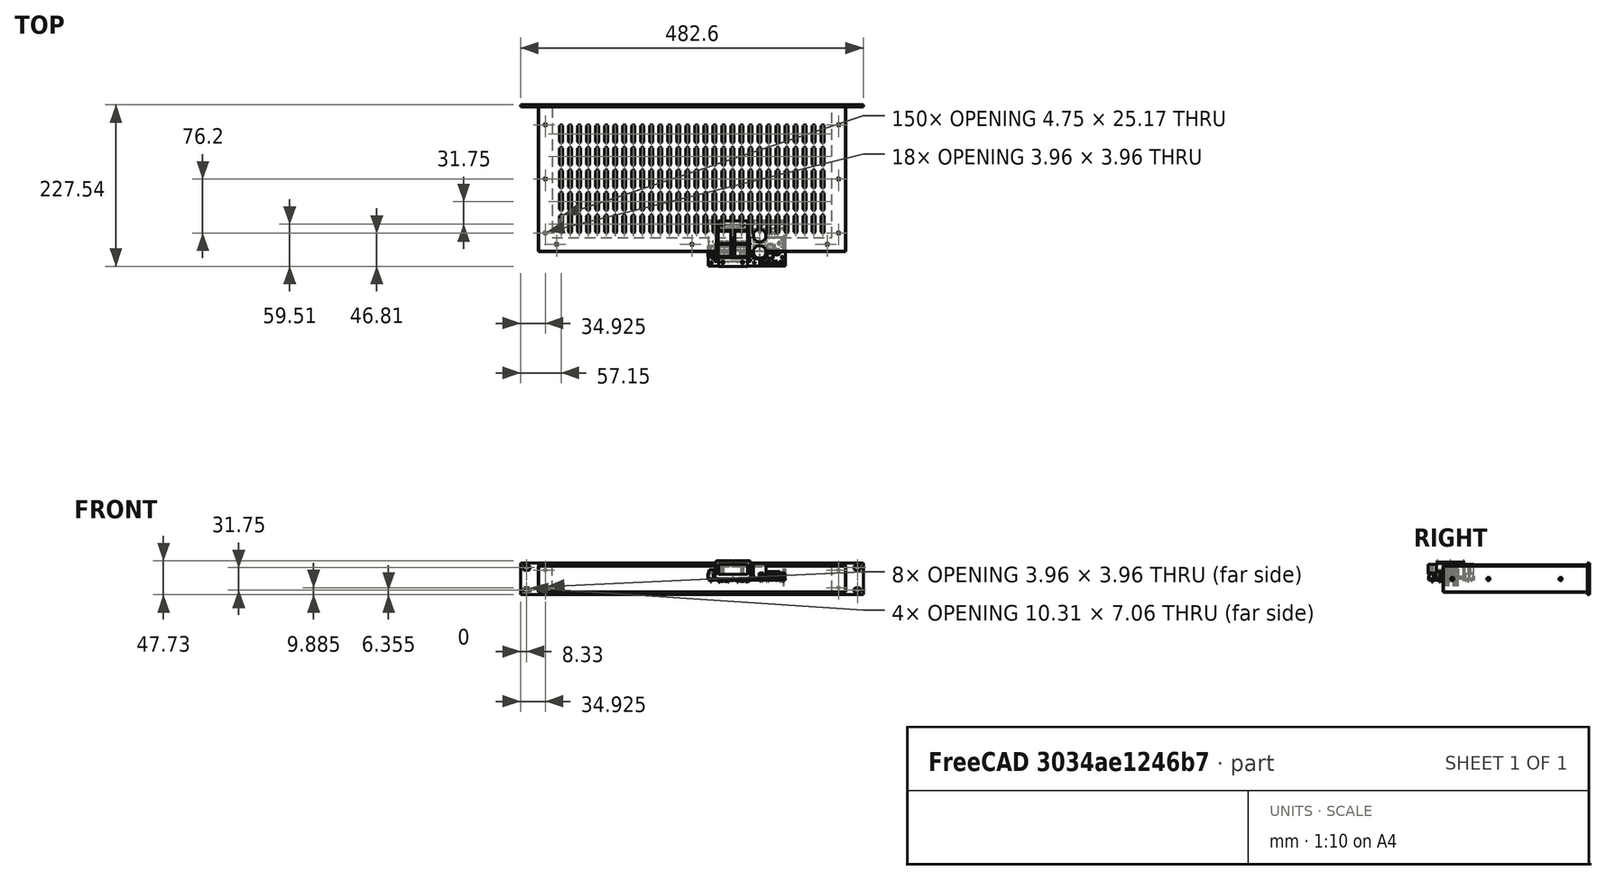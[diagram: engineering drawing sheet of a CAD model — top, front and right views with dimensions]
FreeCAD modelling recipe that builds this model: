
FCSTD DOCUMENT  (FreeCAD 0.19R23074 (Git))
Label: chassis design
License: All rights reserved
LicenseURL: http://en.wikipedia.org/wiki/All_rights_reserved
objects: Part::Prism×340, Part::MultiFuse×164, Part::Box×162, Part::Feature×75, App::Part×5, Part::Cut×3, PartDesign::FeatureBase×3, PartDesign::Body×3, App::DocumentObjectGroup×2, Part::FeaturePython×1, Part::Extrusion×1, Sketcher::SketchObject×1, PartDesign::CoordinateSystem×1
note: 754 computed .brp shape members not serialized (recipe doc carries the construction recipe); baked Part::Feature solids carry a one-line shape summary decoded from their .brp

FEATURE [Part::Box] cube
  AttacherType = Attacher::AttachEngine3D
  Height = 1.27
  Length = 431.8
  Placement = pos=(-215.9,-101.6,-0.635) rot=(0,0,1;0rad)
  Width = 203.2
FEATURE [Part::Prism] prism
  AttacherType = Attacher::AttachEngine3D
  Circumradius = 1.98
  FirstAngle = 0
  Height = 1.29
  Placement = pos=(0,-92.07,-0.645) rot=(0,0,1;0rad)
  Polygon = 20
  SecondAngle = 0
FEATURE [Part::Prism] prism001
  AttacherType = Attacher::AttachEngine3D
  Circumradius = 1.98
  FirstAngle = 0
  Height = 1.29
  Placement = pos=(-190.5,-92.07,-0.645) rot=(0,0,1;0rad)
  Polygon = 20
  SecondAngle = 0
FEATURE [Part::Prism] prism002
  AttacherType = Attacher::AttachEngine3D
  Circumradius = 1.98
  FirstAngle = 0
  Height = 1.29
  Placement = pos=(190.5,-92.07,-0.645) rot=(0,0,1;0rad)
  Polygon = 20
  SecondAngle = 0
FEATURE [Part::Prism] prism003
  AttacherType = Attacher::AttachEngine3D
  Circumradius = 1.98
  FirstAngle = 0
  Height = 1.29
  Placement = pos=(-206.37,0,-0.645) rot=(0,0,1;0rad)
  Polygon = 20
  SecondAngle = 0
FEATURE [Part::Prism] prism004
  AttacherType = Attacher::AttachEngine3D
  Circumradius = 1.98
  FirstAngle = 0
  Height = 1.29
  Placement = pos=(-206.37,-76.2,-0.645) rot=(0,0,1;0rad)
  Polygon = 20
  SecondAngle = 0
FEATURE [Part::Prism] prism005
  AttacherType = Attacher::AttachEngine3D
  Circumradius = 1.98
  FirstAngle = 0
  Height = 1.29
  Placement = pos=(-206.37,76.2,-0.645) rot=(0,0,1;0rad)
  Polygon = 20
  SecondAngle = 0
FEATURE [Part::Prism] prism006
  AttacherType = Attacher::AttachEngine3D
  Circumradius = 1.98
  FirstAngle = 0
  Height = 1.29
  Placement = pos=(206.37,0,-0.645) rot=(0,0,1;0rad)
  Polygon = 20
  SecondAngle = 0
FEATURE [Part::Prism] prism007
  AttacherType = Attacher::AttachEngine3D
  Circumradius = 1.98
  FirstAngle = 0
  Height = 1.29
  Placement = pos=(206.37,-76.2,-0.645) rot=(0,0,1;0rad)
  Polygon = 20
  SecondAngle = 0
FEATURE [Part::Prism] prism008
  AttacherType = Attacher::AttachEngine3D
  Circumradius = 1.98
  FirstAngle = 0
  Height = 1.29
  Placement = pos=(206.37,76.2,-0.645) rot=(0,0,1;0rad)
  Polygon = 20
  SecondAngle = 0
FEATURE [Part::Prism] prism009
  AttacherType = Attacher::AttachEngine3D
  Circumradius = 2.375
  FirstAngle = 0
  Height = 1.29
  Placement = pos=(0,10.325,-0.645) rot=(0,0,1;0rad)
  Polygon = 10
  SecondAngle = 0
FEATURE [Part::Prism] prism010
  AttacherType = Attacher::AttachEngine3D
  Circumradius = 2.375
  FirstAngle = 0
  Height = 1.29
  Placement = pos=(0,-10.325,-0.645) rot=(0,0,1;0rad)
  Polygon = 10
  SecondAngle = 0
FEATURE [Part::Box] cube001
  AttacherType = Attacher::AttachEngine3D
  Height = 1.29
  Length = 4.75
  Placement = pos=(-2.375,-10.325,-0.645) rot=(0,0,1;0rad)
  Width = 20.65
FEATURE [Part::MultiFuse] union
  Placement = pos=(-184.15,63.5,0) rot=(0,0,1;0rad)
  Shapes = -> [prism009,prism010,cube001]
FEATURE [Part::Prism] prism011
  AttacherType = Attacher::AttachEngine3D
  Circumradius = 2.375
  FirstAngle = 0
  Height = 1.29
  Placement = pos=(0,10.325,-0.645) rot=(0,0,1;0rad)
  Polygon = 10
  SecondAngle = 0
FEATURE [Part::Prism] prism012
  AttacherType = Attacher::AttachEngine3D
  Circumradius = 2.375
  FirstAngle = 0
  Height = 1.29
  Placement = pos=(0,-10.325,-0.645) rot=(0,0,1;0rad)
  Polygon = 10
  SecondAngle = 0
FEATURE [Part::Box] cube002
  AttacherType = Attacher::AttachEngine3D
  Height = 1.29
  Length = 4.75
  Placement = pos=(-2.375,-10.325,-0.645) rot=(0,0,1;0rad)
  Width = 20.65
FEATURE [Part::MultiFuse] union001
  Placement = pos=(-171.45,63.5,0) rot=(0,0,1;0rad)
  Shapes = -> [prism011,prism012,cube002]
FEATURE [Part::Prism] prism013
  AttacherType = Attacher::AttachEngine3D
  Circumradius = 2.375
  FirstAngle = 0
  Height = 1.29
  Placement = pos=(0,10.325,-0.645) rot=(0,0,1;0rad)
  Polygon = 10
  SecondAngle = 0
FEATURE [Part::Prism] prism014
  AttacherType = Attacher::AttachEngine3D
  Circumradius = 2.375
  FirstAngle = 0
  Height = 1.29
  Placement = pos=(0,-10.325,-0.645) rot=(0,0,1;0rad)
  Polygon = 10
  SecondAngle = 0
FEATURE [Part::Box] cube003
  AttacherType = Attacher::AttachEngine3D
  Height = 1.29
  Length = 4.75
  Placement = pos=(-2.375,-10.325,-0.645) rot=(0,0,1;0rad)
  Width = 20.65
FEATURE [Part::MultiFuse] union002
  Placement = pos=(-158.75,63.5,0) rot=(0,0,1;0rad)
  Shapes = -> [prism013,prism014,cube003]
FEATURE [Part::Prism] prism015
  AttacherType = Attacher::AttachEngine3D
  Circumradius = 2.375
  FirstAngle = 0
  Height = 1.29
  Placement = pos=(0,10.325,-0.645) rot=(0,0,1;0rad)
  Polygon = 10
  SecondAngle = 0
FEATURE [Part::Prism] prism016
  AttacherType = Attacher::AttachEngine3D
  Circumradius = 2.375
  FirstAngle = 0
  Height = 1.29
  Placement = pos=(0,-10.325,-0.645) rot=(0,0,1;0rad)
  Polygon = 10
  SecondAngle = 0
FEATURE [Part::Box] cube004
  AttacherType = Attacher::AttachEngine3D
  Height = 1.29
  Length = 4.75
  Placement = pos=(-2.375,-10.325,-0.645) rot=(0,0,1;0rad)
  Width = 20.65
FEATURE [Part::MultiFuse] union003
  Placement = pos=(-146.05,63.5,0) rot=(0,0,1;0rad)
  Shapes = -> [prism015,prism016,cube004]
FEATURE [Part::Prism] prism017
  AttacherType = Attacher::AttachEngine3D
  Circumradius = 2.375
  FirstAngle = 0
  Height = 1.29
  Placement = pos=(0,10.325,-0.645) rot=(0,0,1;0rad)
  Polygon = 10
  SecondAngle = 0
FEATURE [Part::Prism] prism018
  AttacherType = Attacher::AttachEngine3D
  Circumradius = 2.375
  FirstAngle = 0
  Height = 1.29
  Placement = pos=(0,-10.325,-0.645) rot=(0,0,1;0rad)
  Polygon = 10
  SecondAngle = 0
FEATURE [Part::Box] cube005
  AttacherType = Attacher::AttachEngine3D
  Height = 1.29
  Length = 4.75
  Placement = pos=(-2.375,-10.325,-0.645) rot=(0,0,1;0rad)
  Width = 20.65
FEATURE [Part::MultiFuse] union004
  Placement = pos=(-133.35,63.5,0) rot=(0,0,1;0rad)
  Shapes = -> [prism017,prism018,cube005]
FEATURE [Part::Prism] prism019
  AttacherType = Attacher::AttachEngine3D
  Circumradius = 2.375
  FirstAngle = 0
  Height = 1.29
  Placement = pos=(0,10.325,-0.645) rot=(0,0,1;0rad)
  Polygon = 10
  SecondAngle = 0
FEATURE [Part::Prism] prism020
  AttacherType = Attacher::AttachEngine3D
  Circumradius = 2.375
  FirstAngle = 0
  Height = 1.29
  Placement = pos=(0,-10.325,-0.645) rot=(0,0,1;0rad)
  Polygon = 10
  SecondAngle = 0
FEATURE [Part::Box] cube006
  AttacherType = Attacher::AttachEngine3D
  Height = 1.29
  Length = 4.75
  Placement = pos=(-2.375,-10.325,-0.645) rot=(0,0,1;0rad)
  Width = 20.65
FEATURE [Part::MultiFuse] union005
  Placement = pos=(-120.65,63.5,0) rot=(0,0,1;0rad)
  Shapes = -> [prism019,prism020,cube006]
FEATURE [Part::Prism] prism021
  AttacherType = Attacher::AttachEngine3D
  Circumradius = 2.375
  FirstAngle = 0
  Height = 1.29
  Placement = pos=(0,10.325,-0.645) rot=(0,0,1;0rad)
  Polygon = 10
  SecondAngle = 0
FEATURE [Part::Prism] prism022
  AttacherType = Attacher::AttachEngine3D
  Circumradius = 2.375
  FirstAngle = 0
  Height = 1.29
  Placement = pos=(0,-10.325,-0.645) rot=(0,0,1;0rad)
  Polygon = 10
  SecondAngle = 0
FEATURE [Part::Box] cube007
  AttacherType = Attacher::AttachEngine3D
  Height = 1.29
  Length = 4.75
  Placement = pos=(-2.375,-10.325,-0.645) rot=(0,0,1;0rad)
  Width = 20.65
FEATURE [Part::MultiFuse] union006
  Placement = pos=(-107.95,63.5,0) rot=(0,0,1;0rad)
  Shapes = -> [prism021,prism022,cube007]
FEATURE [Part::Prism] prism023
  AttacherType = Attacher::AttachEngine3D
  Circumradius = 2.375
  FirstAngle = 0
  Height = 1.29
  Placement = pos=(0,10.325,-0.645) rot=(0,0,1;0rad)
  Polygon = 10
  SecondAngle = 0
FEATURE [Part::Prism] prism024
  AttacherType = Attacher::AttachEngine3D
  Circumradius = 2.375
  FirstAngle = 0
  Height = 1.29
  Placement = pos=(0,-10.325,-0.645) rot=(0,0,1;0rad)
  Polygon = 10
  SecondAngle = 0
FEATURE [Part::Box] cube008
  AttacherType = Attacher::AttachEngine3D
  Height = 1.29
  Length = 4.75
  Placement = pos=(-2.375,-10.325,-0.645) rot=(0,0,1;0rad)
  Width = 20.65
FEATURE [Part::MultiFuse] union007
  Placement = pos=(-95.25,63.5,0) rot=(0,0,1;0rad)
  Shapes = -> [prism023,prism024,cube008]
FEATURE [Part::Prism] prism025
  AttacherType = Attacher::AttachEngine3D
  Circumradius = 2.375
  FirstAngle = 0
  Height = 1.29
  Placement = pos=(0,10.325,-0.645) rot=(0,0,1;0rad)
  Polygon = 10
  SecondAngle = 0
FEATURE [Part::Prism] prism026
  AttacherType = Attacher::AttachEngine3D
  Circumradius = 2.375
  FirstAngle = 0
  Height = 1.29
  Placement = pos=(0,-10.325,-0.645) rot=(0,0,1;0rad)
  Polygon = 10
  SecondAngle = 0
FEATURE [Part::Box] cube009
  AttacherType = Attacher::AttachEngine3D
  Height = 1.29
  Length = 4.75
  Placement = pos=(-2.375,-10.325,-0.645) rot=(0,0,1;0rad)
  Width = 20.65
FEATURE [Part::MultiFuse] union008
  Placement = pos=(-82.55,63.5,0) rot=(0,0,1;0rad)
  Shapes = -> [prism025,prism026,cube009]
FEATURE [Part::Prism] prism027
  AttacherType = Attacher::AttachEngine3D
  Circumradius = 2.375
  FirstAngle = 0
  Height = 1.29
  Placement = pos=(0,10.325,-0.645) rot=(0,0,1;0rad)
  Polygon = 10
  SecondAngle = 0
FEATURE [Part::Prism] prism028
  AttacherType = Attacher::AttachEngine3D
  Circumradius = 2.375
  FirstAngle = 0
  Height = 1.29
  Placement = pos=(0,-10.325,-0.645) rot=(0,0,1;0rad)
  Polygon = 10
  SecondAngle = 0
FEATURE [Part::Box] cube010
  AttacherType = Attacher::AttachEngine3D
  Height = 1.29
  Length = 4.75
  Placement = pos=(-2.375,-10.325,-0.645) rot=(0,0,1;0rad)
  Width = 20.65
FEATURE [Part::MultiFuse] union009
  Placement = pos=(-69.85,63.5,0) rot=(0,0,1;0rad)
  Shapes = -> [prism027,prism028,cube010]
FEATURE [Part::Prism] prism029
  AttacherType = Attacher::AttachEngine3D
  Circumradius = 2.375
  FirstAngle = 0
  Height = 1.29
  Placement = pos=(0,10.325,-0.645) rot=(0,0,1;0rad)
  Polygon = 10
  SecondAngle = 0
FEATURE [Part::Prism] prism030
  AttacherType = Attacher::AttachEngine3D
  Circumradius = 2.375
  FirstAngle = 0
  Height = 1.29
  Placement = pos=(0,-10.325,-0.645) rot=(0,0,1;0rad)
  Polygon = 10
  SecondAngle = 0
FEATURE [Part::Box] cube011
  AttacherType = Attacher::AttachEngine3D
  Height = 1.29
  Length = 4.75
  Placement = pos=(-2.375,-10.325,-0.645) rot=(0,0,1;0rad)
  Width = 20.65
FEATURE [Part::MultiFuse] union010
  Placement = pos=(-57.15,63.5,0) rot=(0,0,1;0rad)
  Shapes = -> [prism029,prism030,cube011]
FEATURE [Part::Prism] prism031
  AttacherType = Attacher::AttachEngine3D
  Circumradius = 2.375
  FirstAngle = 0
  Height = 1.29
  Placement = pos=(0,10.325,-0.645) rot=(0,0,1;0rad)
  Polygon = 10
  SecondAngle = 0
FEATURE [Part::Prism] prism032
  AttacherType = Attacher::AttachEngine3D
  Circumradius = 2.375
  FirstAngle = 0
  Height = 1.29
  Placement = pos=(0,-10.325,-0.645) rot=(0,0,1;0rad)
  Polygon = 10
  SecondAngle = 0
FEATURE [Part::Box] cube012
  AttacherType = Attacher::AttachEngine3D
  Height = 1.29
  Length = 4.75
  Placement = pos=(-2.375,-10.325,-0.645) rot=(0,0,1;0rad)
  Width = 20.65
FEATURE [Part::MultiFuse] union011
  Placement = pos=(-44.45,63.5,0) rot=(0,0,1;0rad)
  Shapes = -> [prism031,prism032,cube012]
FEATURE [Part::Prism] prism033
  AttacherType = Attacher::AttachEngine3D
  Circumradius = 2.375
  FirstAngle = 0
  Height = 1.29
  Placement = pos=(0,10.325,-0.645) rot=(0,0,1;0rad)
  Polygon = 10
  SecondAngle = 0
FEATURE [Part::Prism] prism034
  AttacherType = Attacher::AttachEngine3D
  Circumradius = 2.375
  FirstAngle = 0
  Height = 1.29
  Placement = pos=(0,-10.325,-0.645) rot=(0,0,1;0rad)
  Polygon = 10
  SecondAngle = 0
FEATURE [Part::Box] cube013
  AttacherType = Attacher::AttachEngine3D
  Height = 1.29
  Length = 4.75
  Placement = pos=(-2.375,-10.325,-0.645) rot=(0,0,1;0rad)
  Width = 20.65
FEATURE [Part::MultiFuse] union012
  Placement = pos=(-31.75,63.5,0) rot=(0,0,1;0rad)
  Shapes = -> [prism033,prism034,cube013]
FEATURE [Part::Prism] prism035
  AttacherType = Attacher::AttachEngine3D
  Circumradius = 2.375
  FirstAngle = 0
  Height = 1.29
  Placement = pos=(0,10.325,-0.645) rot=(0,0,1;0rad)
  Polygon = 10
  SecondAngle = 0
FEATURE [Part::Prism] prism036
  AttacherType = Attacher::AttachEngine3D
  Circumradius = 2.375
  FirstAngle = 0
  Height = 1.29
  Placement = pos=(0,-10.325,-0.645) rot=(0,0,1;0rad)
  Polygon = 10
  SecondAngle = 0
FEATURE [Part::Box] cube014
  AttacherType = Attacher::AttachEngine3D
  Height = 1.29
  Length = 4.75
  Placement = pos=(-2.375,-10.325,-0.645) rot=(0,0,1;0rad)
  Width = 20.65
FEATURE [Part::MultiFuse] union013
  Placement = pos=(-19.05,63.5,0) rot=(0,0,1;0rad)
  Shapes = -> [prism035,prism036,cube014]
FEATURE [Part::Prism] prism037
  AttacherType = Attacher::AttachEngine3D
  Circumradius = 2.375
  FirstAngle = 0
  Height = 1.29
  Placement = pos=(0,10.325,-0.645) rot=(0,0,1;0rad)
  Polygon = 10
  SecondAngle = 0
FEATURE [Part::Prism] prism038
  AttacherType = Attacher::AttachEngine3D
  Circumradius = 2.375
  FirstAngle = 0
  Height = 1.29
  Placement = pos=(0,-10.325,-0.645) rot=(0,0,1;0rad)
  Polygon = 10
  SecondAngle = 0
FEATURE [Part::Box] cube015
  AttacherType = Attacher::AttachEngine3D
  Height = 1.29
  Length = 4.75
  Placement = pos=(-2.375,-10.325,-0.645) rot=(0,0,1;0rad)
  Width = 20.65
FEATURE [Part::MultiFuse] union014
  Placement = pos=(-6.35,63.5,0) rot=(0,0,1;0rad)
  Shapes = -> [prism037,prism038,cube015]
FEATURE [Part::Prism] prism039
  AttacherType = Attacher::AttachEngine3D
  Circumradius = 2.375
  FirstAngle = 0
  Height = 1.29
  Placement = pos=(0,10.325,-0.645) rot=(0,0,1;0rad)
  Polygon = 10
  SecondAngle = 0
FEATURE [Part::Prism] prism040
  AttacherType = Attacher::AttachEngine3D
  Circumradius = 2.375
  FirstAngle = 0
  Height = 1.29
  Placement = pos=(0,-10.325,-0.645) rot=(0,0,1;0rad)
  Polygon = 10
  SecondAngle = 0
FEATURE [Part::Box] cube016
  AttacherType = Attacher::AttachEngine3D
  Height = 1.29
  Length = 4.75
  Placement = pos=(-2.375,-10.325,-0.645) rot=(0,0,1;0rad)
  Width = 20.65
FEATURE [Part::MultiFuse] union015
  Placement = pos=(6.35,63.5,0) rot=(0,0,1;0rad)
  Shapes = -> [prism039,prism040,cube016]
FEATURE [Part::Prism] prism041
  AttacherType = Attacher::AttachEngine3D
  Circumradius = 2.375
  FirstAngle = 0
  Height = 1.29
  Placement = pos=(0,10.325,-0.645) rot=(0,0,1;0rad)
  Polygon = 10
  SecondAngle = 0
FEATURE [Part::Prism] prism042
  AttacherType = Attacher::AttachEngine3D
  Circumradius = 2.375
  FirstAngle = 0
  Height = 1.29
  Placement = pos=(0,-10.325,-0.645) rot=(0,0,1;0rad)
  Polygon = 10
  SecondAngle = 0
FEATURE [Part::Box] cube017
  AttacherType = Attacher::AttachEngine3D
  Height = 1.29
  Length = 4.75
  Placement = pos=(-2.375,-10.325,-0.645) rot=(0,0,1;0rad)
  Width = 20.65
FEATURE [Part::MultiFuse] union016
  Placement = pos=(19.05,63.5,0) rot=(0,0,1;0rad)
  Shapes = -> [prism041,prism042,cube017]
FEATURE [Part::Prism] prism043
  AttacherType = Attacher::AttachEngine3D
  Circumradius = 2.375
  FirstAngle = 0
  Height = 1.29
  Placement = pos=(0,10.325,-0.645) rot=(0,0,1;0rad)
  Polygon = 10
  SecondAngle = 0
FEATURE [Part::Prism] prism044
  AttacherType = Attacher::AttachEngine3D
  Circumradius = 2.375
  FirstAngle = 0
  Height = 1.29
  Placement = pos=(0,-10.325,-0.645) rot=(0,0,1;0rad)
  Polygon = 10
  SecondAngle = 0
FEATURE [Part::Box] cube018
  AttacherType = Attacher::AttachEngine3D
  Height = 1.29
  Length = 4.75
  Placement = pos=(-2.375,-10.325,-0.645) rot=(0,0,1;0rad)
  Width = 20.65
FEATURE [Part::MultiFuse] union017
  Placement = pos=(31.75,63.5,0) rot=(0,0,1;0rad)
  Shapes = -> [prism043,prism044,cube018]
FEATURE [Part::Prism] prism045
  AttacherType = Attacher::AttachEngine3D
  Circumradius = 2.375
  FirstAngle = 0
  Height = 1.29
  Placement = pos=(0,10.325,-0.645) rot=(0,0,1;0rad)
  Polygon = 10
  SecondAngle = 0
FEATURE [Part::Prism] prism046
  AttacherType = Attacher::AttachEngine3D
  Circumradius = 2.375
  FirstAngle = 0
  Height = 1.29
  Placement = pos=(0,-10.325,-0.645) rot=(0,0,1;0rad)
  Polygon = 10
  SecondAngle = 0
FEATURE [Part::Box] cube019
  AttacherType = Attacher::AttachEngine3D
  Height = 1.29
  Length = 4.75
  Placement = pos=(-2.375,-10.325,-0.645) rot=(0,0,1;0rad)
  Width = 20.65
FEATURE [Part::MultiFuse] union018
  Placement = pos=(44.45,63.5,0) rot=(0,0,1;0rad)
  Shapes = -> [prism045,prism046,cube019]
FEATURE [Part::Prism] prism047
  AttacherType = Attacher::AttachEngine3D
  Circumradius = 2.375
  FirstAngle = 0
  Height = 1.29
  Placement = pos=(0,10.325,-0.645) rot=(0,0,1;0rad)
  Polygon = 10
  SecondAngle = 0
FEATURE [Part::Prism] prism048
  AttacherType = Attacher::AttachEngine3D
  Circumradius = 2.375
  FirstAngle = 0
  Height = 1.29
  Placement = pos=(0,-10.325,-0.645) rot=(0,0,1;0rad)
  Polygon = 10
  SecondAngle = 0
FEATURE [Part::Box] cube020
  AttacherType = Attacher::AttachEngine3D
  Height = 1.29
  Length = 4.75
  Placement = pos=(-2.375,-10.325,-0.645) rot=(0,0,1;0rad)
  Width = 20.65
FEATURE [Part::MultiFuse] union019
  Placement = pos=(57.15,63.5,0) rot=(0,0,1;0rad)
  Shapes = -> [prism047,prism048,cube020]
FEATURE [Part::Prism] prism049
  AttacherType = Attacher::AttachEngine3D
  Circumradius = 2.375
  FirstAngle = 0
  Height = 1.29
  Placement = pos=(0,10.325,-0.645) rot=(0,0,1;0rad)
  Polygon = 10
  SecondAngle = 0
FEATURE [Part::Prism] prism050
  AttacherType = Attacher::AttachEngine3D
  Circumradius = 2.375
  FirstAngle = 0
  Height = 1.29
  Placement = pos=(0,-10.325,-0.645) rot=(0,0,1;0rad)
  Polygon = 10
  SecondAngle = 0
FEATURE [Part::Box] cube021
  AttacherType = Attacher::AttachEngine3D
  Height = 1.29
  Length = 4.75
  Placement = pos=(-2.375,-10.325,-0.645) rot=(0,0,1;0rad)
  Width = 20.65
FEATURE [Part::MultiFuse] union020
  Placement = pos=(69.85,63.5,0) rot=(0,0,1;0rad)
  Shapes = -> [prism049,prism050,cube021]
FEATURE [Part::Prism] prism051
  AttacherType = Attacher::AttachEngine3D
  Circumradius = 2.375
  FirstAngle = 0
  Height = 1.29
  Placement = pos=(0,10.325,-0.645) rot=(0,0,1;0rad)
  Polygon = 10
  SecondAngle = 0
FEATURE [Part::Prism] prism052
  AttacherType = Attacher::AttachEngine3D
  Circumradius = 2.375
  FirstAngle = 0
  Height = 1.29
  Placement = pos=(0,-10.325,-0.645) rot=(0,0,1;0rad)
  Polygon = 10
  SecondAngle = 0
FEATURE [Part::Box] cube022
  AttacherType = Attacher::AttachEngine3D
  Height = 1.29
  Length = 4.75
  Placement = pos=(-2.375,-10.325,-0.645) rot=(0,0,1;0rad)
  Width = 20.65
FEATURE [Part::MultiFuse] union021
  Placement = pos=(82.55,63.5,0) rot=(0,0,1;0rad)
  Shapes = -> [prism051,prism052,cube022]
FEATURE [Part::Prism] prism053
  AttacherType = Attacher::AttachEngine3D
  Circumradius = 2.375
  FirstAngle = 0
  Height = 1.29
  Placement = pos=(0,10.325,-0.645) rot=(0,0,1;0rad)
  Polygon = 10
  SecondAngle = 0
FEATURE [Part::Prism] prism054
  AttacherType = Attacher::AttachEngine3D
  Circumradius = 2.375
  FirstAngle = 0
  Height = 1.29
  Placement = pos=(0,-10.325,-0.645) rot=(0,0,1;0rad)
  Polygon = 10
  SecondAngle = 0
FEATURE [Part::Box] cube023
  AttacherType = Attacher::AttachEngine3D
  Height = 1.29
  Length = 4.75
  Placement = pos=(-2.375,-10.325,-0.645) rot=(0,0,1;0rad)
  Width = 20.65
FEATURE [Part::MultiFuse] union022
  Placement = pos=(95.25,63.5,0) rot=(0,0,1;0rad)
  Shapes = -> [prism053,prism054,cube023]
FEATURE [Part::Prism] prism055
  AttacherType = Attacher::AttachEngine3D
  Circumradius = 2.375
  FirstAngle = 0
  Height = 1.29
  Placement = pos=(0,10.325,-0.645) rot=(0,0,1;0rad)
  Polygon = 10
  SecondAngle = 0
FEATURE [Part::Prism] prism056
  AttacherType = Attacher::AttachEngine3D
  Circumradius = 2.375
  FirstAngle = 0
  Height = 1.29
  Placement = pos=(0,-10.325,-0.645) rot=(0,0,1;0rad)
  Polygon = 10
  SecondAngle = 0
FEATURE [Part::Box] cube024
  AttacherType = Attacher::AttachEngine3D
  Height = 1.29
  Length = 4.75
  Placement = pos=(-2.375,-10.325,-0.645) rot=(0,0,1;0rad)
  Width = 20.65
FEATURE [Part::MultiFuse] union023
  Placement = pos=(107.95,63.5,0) rot=(0,0,1;0rad)
  Shapes = -> [prism055,prism056,cube024]
FEATURE [Part::Prism] prism057
  AttacherType = Attacher::AttachEngine3D
  Circumradius = 2.375
  FirstAngle = 0
  Height = 1.29
  Placement = pos=(0,10.325,-0.645) rot=(0,0,1;0rad)
  Polygon = 10
  SecondAngle = 0
FEATURE [Part::Prism] prism058
  AttacherType = Attacher::AttachEngine3D
  Circumradius = 2.375
  FirstAngle = 0
  Height = 1.29
  Placement = pos=(0,-10.325,-0.645) rot=(0,0,1;0rad)
  Polygon = 10
  SecondAngle = 0
FEATURE [Part::Box] cube025
  AttacherType = Attacher::AttachEngine3D
  Height = 1.29
  Length = 4.75
  Placement = pos=(-2.375,-10.325,-0.645) rot=(0,0,1;0rad)
  Width = 20.65
FEATURE [Part::MultiFuse] union024
  Placement = pos=(120.65,63.5,0) rot=(0,0,1;0rad)
  Shapes = -> [prism057,prism058,cube025]
FEATURE [Part::Prism] prism059
  AttacherType = Attacher::AttachEngine3D
  Circumradius = 2.375
  FirstAngle = 0
  Height = 1.29
  Placement = pos=(0,10.325,-0.645) rot=(0,0,1;0rad)
  Polygon = 10
  SecondAngle = 0
FEATURE [Part::Prism] prism060
  AttacherType = Attacher::AttachEngine3D
  Circumradius = 2.375
  FirstAngle = 0
  Height = 1.29
  Placement = pos=(0,-10.325,-0.645) rot=(0,0,1;0rad)
  Polygon = 10
  SecondAngle = 0
FEATURE [Part::Box] cube026
  AttacherType = Attacher::AttachEngine3D
  Height = 1.29
  Length = 4.75
  Placement = pos=(-2.375,-10.325,-0.645) rot=(0,0,1;0rad)
  Width = 20.65
FEATURE [Part::MultiFuse] union025
  Placement = pos=(133.35,63.5,0) rot=(0,0,1;0rad)
  Shapes = -> [prism059,prism060,cube026]
FEATURE [Part::Prism] prism061
  AttacherType = Attacher::AttachEngine3D
  Circumradius = 2.375
  FirstAngle = 0
  Height = 1.29
  Placement = pos=(0,10.325,-0.645) rot=(0,0,1;0rad)
  Polygon = 10
  SecondAngle = 0
FEATURE [Part::Prism] prism062
  AttacherType = Attacher::AttachEngine3D
  Circumradius = 2.375
  FirstAngle = 0
  Height = 1.29
  Placement = pos=(0,-10.325,-0.645) rot=(0,0,1;0rad)
  Polygon = 10
  SecondAngle = 0
FEATURE [Part::Box] cube027
  AttacherType = Attacher::AttachEngine3D
  Height = 1.29
  Length = 4.75
  Placement = pos=(-2.375,-10.325,-0.645) rot=(0,0,1;0rad)
  Width = 20.65
FEATURE [Part::MultiFuse] union026
  Placement = pos=(146.05,63.5,0) rot=(0,0,1;0rad)
  Shapes = -> [prism061,prism062,cube027]
FEATURE [Part::Prism] prism063
  AttacherType = Attacher::AttachEngine3D
  Circumradius = 2.375
  FirstAngle = 0
  Height = 1.29
  Placement = pos=(0,10.325,-0.645) rot=(0,0,1;0rad)
  Polygon = 10
  SecondAngle = 0
FEATURE [Part::Prism] prism064
  AttacherType = Attacher::AttachEngine3D
  Circumradius = 2.375
  FirstAngle = 0
  Height = 1.29
  Placement = pos=(0,-10.325,-0.645) rot=(0,0,1;0rad)
  Polygon = 10
  SecondAngle = 0
FEATURE [Part::Box] cube028
  AttacherType = Attacher::AttachEngine3D
  Height = 1.29
  Length = 4.75
  Placement = pos=(-2.375,-10.325,-0.645) rot=(0,0,1;0rad)
  Width = 20.65
FEATURE [Part::MultiFuse] union027
  Placement = pos=(158.75,63.5,0) rot=(0,0,1;0rad)
  Shapes = -> [prism063,prism064,cube028]
FEATURE [Part::Prism] prism065
  AttacherType = Attacher::AttachEngine3D
  Circumradius = 2.375
  FirstAngle = 0
  Height = 1.29
  Placement = pos=(0,10.325,-0.645) rot=(0,0,1;0rad)
  Polygon = 10
  SecondAngle = 0
FEATURE [Part::Prism] prism066
  AttacherType = Attacher::AttachEngine3D
  Circumradius = 2.375
  FirstAngle = 0
  Height = 1.29
  Placement = pos=(0,-10.325,-0.645) rot=(0,0,1;0rad)
  Polygon = 10
  SecondAngle = 0
FEATURE [Part::Box] cube029
  AttacherType = Attacher::AttachEngine3D
  Height = 1.29
  Length = 4.75
  Placement = pos=(-2.375,-10.325,-0.645) rot=(0,0,1;0rad)
  Width = 20.65
FEATURE [Part::MultiFuse] union028
  Placement = pos=(171.45,63.5,0) rot=(0,0,1;0rad)
  Shapes = -> [prism065,prism066,cube029]
FEATURE [Part::Prism] prism067
  AttacherType = Attacher::AttachEngine3D
  Circumradius = 2.375
  FirstAngle = 0
  Height = 1.29
  Placement = pos=(0,10.325,-0.645) rot=(0,0,1;0rad)
  Polygon = 10
  SecondAngle = 0
FEATURE [Part::Prism] prism068
  AttacherType = Attacher::AttachEngine3D
  Circumradius = 2.375
  FirstAngle = 0
  Height = 1.29
  Placement = pos=(0,-10.325,-0.645) rot=(0,0,1;0rad)
  Polygon = 10
  SecondAngle = 0
FEATURE [Part::Box] cube030
  AttacherType = Attacher::AttachEngine3D
  Height = 1.29
  Length = 4.75
  Placement = pos=(-2.375,-10.325,-0.645) rot=(0,0,1;0rad)
  Width = 20.65
FEATURE [Part::MultiFuse] union029
  Placement = pos=(184.15,63.5,0) rot=(0,0,1;0rad)
  Shapes = -> [prism067,prism068,cube030]
FEATURE [Part::MultiFuse] Group
  Shapes = -> [union,union001,union002,union003,union004,union005,union006,union007,union008,union009,union010,union011,union012,union013,union014,union015,union016,union017,union018,union019,union020,union021,union022,union023,union024,union025,union026,union027,union028,union029]
FEATURE [Part::Prism] prism069
  AttacherType = Attacher::AttachEngine3D
  Circumradius = 2.375
  FirstAngle = 0
  Height = 1.29
  Placement = pos=(0,10.325,-0.645) rot=(0,0,1;0rad)
  Polygon = 10
  SecondAngle = 0
FEATURE [Part::Prism] prism070
  AttacherType = Attacher::AttachEngine3D
  Circumradius = 2.375
  FirstAngle = 0
  Height = 1.29
  Placement = pos=(0,-10.325,-0.645) rot=(0,0,1;0rad)
  Polygon = 10
  SecondAngle = 0
FEATURE [Part::Box] cube031
  AttacherType = Attacher::AttachEngine3D
  Height = 1.29
  Length = 4.75
  Placement = pos=(-2.375,-10.325,-0.645) rot=(0,0,1;0rad)
  Width = 20.65
FEATURE [Part::MultiFuse] union030
  Placement = pos=(-184.15,31.75,0) rot=(0,0,1;0rad)
  Shapes = -> [prism069,prism070,cube031]
FEATURE [Part::Prism] prism071
  AttacherType = Attacher::AttachEngine3D
  Circumradius = 2.375
  FirstAngle = 0
  Height = 1.29
  Placement = pos=(0,10.325,-0.645) rot=(0,0,1;0rad)
  Polygon = 10
  SecondAngle = 0
FEATURE [Part::Prism] prism072
  AttacherType = Attacher::AttachEngine3D
  Circumradius = 2.375
  FirstAngle = 0
  Height = 1.29
  Placement = pos=(0,-10.325,-0.645) rot=(0,0,1;0rad)
  Polygon = 10
  SecondAngle = 0
FEATURE [Part::Box] cube032
  AttacherType = Attacher::AttachEngine3D
  Height = 1.29
  Length = 4.75
  Placement = pos=(-2.375,-10.325,-0.645) rot=(0,0,1;0rad)
  Width = 20.65
FEATURE [Part::MultiFuse] union031
  Placement = pos=(-171.45,31.75,0) rot=(0,0,1;0rad)
  Shapes = -> [prism071,prism072,cube032]
FEATURE [Part::Prism] prism073
  AttacherType = Attacher::AttachEngine3D
  Circumradius = 2.375
  FirstAngle = 0
  Height = 1.29
  Placement = pos=(0,10.325,-0.645) rot=(0,0,1;0rad)
  Polygon = 10
  SecondAngle = 0
FEATURE [Part::Prism] prism074
  AttacherType = Attacher::AttachEngine3D
  Circumradius = 2.375
  FirstAngle = 0
  Height = 1.29
  Placement = pos=(0,-10.325,-0.645) rot=(0,0,1;0rad)
  Polygon = 10
  SecondAngle = 0
FEATURE [Part::Box] cube033
  AttacherType = Attacher::AttachEngine3D
  Height = 1.29
  Length = 4.75
  Placement = pos=(-2.375,-10.325,-0.645) rot=(0,0,1;0rad)
  Width = 20.65
FEATURE [Part::MultiFuse] union032
  Placement = pos=(-158.75,31.75,0) rot=(0,0,1;0rad)
  Shapes = -> [prism073,prism074,cube033]
FEATURE [Part::Prism] prism075
  AttacherType = Attacher::AttachEngine3D
  Circumradius = 2.375
  FirstAngle = 0
  Height = 1.29
  Placement = pos=(0,10.325,-0.645) rot=(0,0,1;0rad)
  Polygon = 10
  SecondAngle = 0
FEATURE [Part::Prism] prism076
  AttacherType = Attacher::AttachEngine3D
  Circumradius = 2.375
  FirstAngle = 0
  Height = 1.29
  Placement = pos=(0,-10.325,-0.645) rot=(0,0,1;0rad)
  Polygon = 10
  SecondAngle = 0
FEATURE [Part::Box] cube034
  AttacherType = Attacher::AttachEngine3D
  Height = 1.29
  Length = 4.75
  Placement = pos=(-2.375,-10.325,-0.645) rot=(0,0,1;0rad)
  Width = 20.65
FEATURE [Part::MultiFuse] union033
  Placement = pos=(-146.05,31.75,0) rot=(0,0,1;0rad)
  Shapes = -> [prism075,prism076,cube034]
FEATURE [Part::Prism] prism077
  AttacherType = Attacher::AttachEngine3D
  Circumradius = 2.375
  FirstAngle = 0
  Height = 1.29
  Placement = pos=(0,10.325,-0.645) rot=(0,0,1;0rad)
  Polygon = 10
  SecondAngle = 0
FEATURE [Part::Prism] prism078
  AttacherType = Attacher::AttachEngine3D
  Circumradius = 2.375
  FirstAngle = 0
  Height = 1.29
  Placement = pos=(0,-10.325,-0.645) rot=(0,0,1;0rad)
  Polygon = 10
  SecondAngle = 0
FEATURE [Part::Box] cube035
  AttacherType = Attacher::AttachEngine3D
  Height = 1.29
  Length = 4.75
  Placement = pos=(-2.375,-10.325,-0.645) rot=(0,0,1;0rad)
  Width = 20.65
FEATURE [Part::MultiFuse] union034
  Placement = pos=(-133.35,31.75,0) rot=(0,0,1;0rad)
  Shapes = -> [prism077,prism078,cube035]
FEATURE [Part::Prism] prism079
  AttacherType = Attacher::AttachEngine3D
  Circumradius = 2.375
  FirstAngle = 0
  Height = 1.29
  Placement = pos=(0,10.325,-0.645) rot=(0,0,1;0rad)
  Polygon = 10
  SecondAngle = 0
FEATURE [Part::Prism] prism080
  AttacherType = Attacher::AttachEngine3D
  Circumradius = 2.375
  FirstAngle = 0
  Height = 1.29
  Placement = pos=(0,-10.325,-0.645) rot=(0,0,1;0rad)
  Polygon = 10
  SecondAngle = 0
FEATURE [Part::Box] cube036
  AttacherType = Attacher::AttachEngine3D
  Height = 1.29
  Length = 4.75
  Placement = pos=(-2.375,-10.325,-0.645) rot=(0,0,1;0rad)
  Width = 20.65
FEATURE [Part::MultiFuse] union035
  Placement = pos=(-120.65,31.75,0) rot=(0,0,1;0rad)
  Shapes = -> [prism079,prism080,cube036]
FEATURE [Part::Prism] prism081
  AttacherType = Attacher::AttachEngine3D
  Circumradius = 2.375
  FirstAngle = 0
  Height = 1.29
  Placement = pos=(0,10.325,-0.645) rot=(0,0,1;0rad)
  Polygon = 10
  SecondAngle = 0
FEATURE [Part::Prism] prism082
  AttacherType = Attacher::AttachEngine3D
  Circumradius = 2.375
  FirstAngle = 0
  Height = 1.29
  Placement = pos=(0,-10.325,-0.645) rot=(0,0,1;0rad)
  Polygon = 10
  SecondAngle = 0
FEATURE [Part::Box] cube037
  AttacherType = Attacher::AttachEngine3D
  Height = 1.29
  Length = 4.75
  Placement = pos=(-2.375,-10.325,-0.645) rot=(0,0,1;0rad)
  Width = 20.65
FEATURE [Part::MultiFuse] union036
  Placement = pos=(-107.95,31.75,0) rot=(0,0,1;0rad)
  Shapes = -> [prism081,prism082,cube037]
FEATURE [Part::Prism] prism083
  AttacherType = Attacher::AttachEngine3D
  Circumradius = 2.375
  FirstAngle = 0
  Height = 1.29
  Placement = pos=(0,10.325,-0.645) rot=(0,0,1;0rad)
  Polygon = 10
  SecondAngle = 0
FEATURE [Part::Prism] prism084
  AttacherType = Attacher::AttachEngine3D
  Circumradius = 2.375
  FirstAngle = 0
  Height = 1.29
  Placement = pos=(0,-10.325,-0.645) rot=(0,0,1;0rad)
  Polygon = 10
  SecondAngle = 0
FEATURE [Part::Box] cube038
  AttacherType = Attacher::AttachEngine3D
  Height = 1.29
  Length = 4.75
  Placement = pos=(-2.375,-10.325,-0.645) rot=(0,0,1;0rad)
  Width = 20.65
FEATURE [Part::MultiFuse] union037
  Placement = pos=(-95.25,31.75,0) rot=(0,0,1;0rad)
  Shapes = -> [prism083,prism084,cube038]
FEATURE [Part::Prism] prism085
  AttacherType = Attacher::AttachEngine3D
  Circumradius = 2.375
  FirstAngle = 0
  Height = 1.29
  Placement = pos=(0,10.325,-0.645) rot=(0,0,1;0rad)
  Polygon = 10
  SecondAngle = 0
FEATURE [Part::Prism] prism086
  AttacherType = Attacher::AttachEngine3D
  Circumradius = 2.375
  FirstAngle = 0
  Height = 1.29
  Placement = pos=(0,-10.325,-0.645) rot=(0,0,1;0rad)
  Polygon = 10
  SecondAngle = 0
FEATURE [Part::Box] cube039
  AttacherType = Attacher::AttachEngine3D
  Height = 1.29
  Length = 4.75
  Placement = pos=(-2.375,-10.325,-0.645) rot=(0,0,1;0rad)
  Width = 20.65
FEATURE [Part::MultiFuse] union038
  Placement = pos=(-82.55,31.75,0) rot=(0,0,1;0rad)
  Shapes = -> [prism085,prism086,cube039]
FEATURE [Part::Prism] prism087
  AttacherType = Attacher::AttachEngine3D
  Circumradius = 2.375
  FirstAngle = 0
  Height = 1.29
  Placement = pos=(0,10.325,-0.645) rot=(0,0,1;0rad)
  Polygon = 10
  SecondAngle = 0
FEATURE [Part::Prism] prism088
  AttacherType = Attacher::AttachEngine3D
  Circumradius = 2.375
  FirstAngle = 0
  Height = 1.29
  Placement = pos=(0,-10.325,-0.645) rot=(0,0,1;0rad)
  Polygon = 10
  SecondAngle = 0
FEATURE [Part::Box] cube040
  AttacherType = Attacher::AttachEngine3D
  Height = 1.29
  Length = 4.75
  Placement = pos=(-2.375,-10.325,-0.645) rot=(0,0,1;0rad)
  Width = 20.65
FEATURE [Part::MultiFuse] union039
  Placement = pos=(-69.85,31.75,0) rot=(0,0,1;0rad)
  Shapes = -> [prism087,prism088,cube040]
FEATURE [Part::Prism] prism089
  AttacherType = Attacher::AttachEngine3D
  Circumradius = 2.375
  FirstAngle = 0
  Height = 1.29
  Placement = pos=(0,10.325,-0.645) rot=(0,0,1;0rad)
  Polygon = 10
  SecondAngle = 0
FEATURE [Part::Prism] prism090
  AttacherType = Attacher::AttachEngine3D
  Circumradius = 2.375
  FirstAngle = 0
  Height = 1.29
  Placement = pos=(0,-10.325,-0.645) rot=(0,0,1;0rad)
  Polygon = 10
  SecondAngle = 0
FEATURE [Part::Box] cube041
  AttacherType = Attacher::AttachEngine3D
  Height = 1.29
  Length = 4.75
  Placement = pos=(-2.375,-10.325,-0.645) rot=(0,0,1;0rad)
  Width = 20.65
FEATURE [Part::MultiFuse] union040
  Placement = pos=(-57.15,31.75,0) rot=(0,0,1;0rad)
  Shapes = -> [prism089,prism090,cube041]
FEATURE [Part::Prism] prism091
  AttacherType = Attacher::AttachEngine3D
  Circumradius = 2.375
  FirstAngle = 0
  Height = 1.29
  Placement = pos=(0,10.325,-0.645) rot=(0,0,1;0rad)
  Polygon = 10
  SecondAngle = 0
FEATURE [Part::Prism] prism092
  AttacherType = Attacher::AttachEngine3D
  Circumradius = 2.375
  FirstAngle = 0
  Height = 1.29
  Placement = pos=(0,-10.325,-0.645) rot=(0,0,1;0rad)
  Polygon = 10
  SecondAngle = 0
FEATURE [Part::Box] cube042
  AttacherType = Attacher::AttachEngine3D
  Height = 1.29
  Length = 4.75
  Placement = pos=(-2.375,-10.325,-0.645) rot=(0,0,1;0rad)
  Width = 20.65
FEATURE [Part::MultiFuse] union041
  Placement = pos=(-44.45,31.75,0) rot=(0,0,1;0rad)
  Shapes = -> [prism091,prism092,cube042]
FEATURE [Part::Prism] prism093
  AttacherType = Attacher::AttachEngine3D
  Circumradius = 2.375
  FirstAngle = 0
  Height = 1.29
  Placement = pos=(0,10.325,-0.645) rot=(0,0,1;0rad)
  Polygon = 10
  SecondAngle = 0
FEATURE [Part::Prism] prism094
  AttacherType = Attacher::AttachEngine3D
  Circumradius = 2.375
  FirstAngle = 0
  Height = 1.29
  Placement = pos=(0,-10.325,-0.645) rot=(0,0,1;0rad)
  Polygon = 10
  SecondAngle = 0
FEATURE [Part::Box] cube043
  AttacherType = Attacher::AttachEngine3D
  Height = 1.29
  Length = 4.75
  Placement = pos=(-2.375,-10.325,-0.645) rot=(0,0,1;0rad)
  Width = 20.65
FEATURE [Part::MultiFuse] union042
  Placement = pos=(-31.75,31.75,0) rot=(0,0,1;0rad)
  Shapes = -> [prism093,prism094,cube043]
FEATURE [Part::Prism] prism095
  AttacherType = Attacher::AttachEngine3D
  Circumradius = 2.375
  FirstAngle = 0
  Height = 1.29
  Placement = pos=(0,10.325,-0.645) rot=(0,0,1;0rad)
  Polygon = 10
  SecondAngle = 0
FEATURE [Part::Prism] prism096
  AttacherType = Attacher::AttachEngine3D
  Circumradius = 2.375
  FirstAngle = 0
  Height = 1.29
  Placement = pos=(0,-10.325,-0.645) rot=(0,0,1;0rad)
  Polygon = 10
  SecondAngle = 0
FEATURE [Part::Box] cube044
  AttacherType = Attacher::AttachEngine3D
  Height = 1.29
  Length = 4.75
  Placement = pos=(-2.375,-10.325,-0.645) rot=(0,0,1;0rad)
  Width = 20.65
FEATURE [Part::MultiFuse] union043
  Placement = pos=(-19.05,31.75,0) rot=(0,0,1;0rad)
  Shapes = -> [prism095,prism096,cube044]
FEATURE [Part::Prism] prism097
  AttacherType = Attacher::AttachEngine3D
  Circumradius = 2.375
  FirstAngle = 0
  Height = 1.29
  Placement = pos=(0,10.325,-0.645) rot=(0,0,1;0rad)
  Polygon = 10
  SecondAngle = 0
FEATURE [Part::Prism] prism098
  AttacherType = Attacher::AttachEngine3D
  Circumradius = 2.375
  FirstAngle = 0
  Height = 1.29
  Placement = pos=(0,-10.325,-0.645) rot=(0,0,1;0rad)
  Polygon = 10
  SecondAngle = 0
FEATURE [Part::Box] cube045
  AttacherType = Attacher::AttachEngine3D
  Height = 1.29
  Length = 4.75
  Placement = pos=(-2.375,-10.325,-0.645) rot=(0,0,1;0rad)
  Width = 20.65
FEATURE [Part::MultiFuse] union044
  Placement = pos=(-6.35,31.75,0) rot=(0,0,1;0rad)
  Shapes = -> [prism097,prism098,cube045]
FEATURE [Part::Prism] prism099
  AttacherType = Attacher::AttachEngine3D
  Circumradius = 2.375
  FirstAngle = 0
  Height = 1.29
  Placement = pos=(0,10.325,-0.645) rot=(0,0,1;0rad)
  Polygon = 10
  SecondAngle = 0
FEATURE [Part::Prism] prism100
  AttacherType = Attacher::AttachEngine3D
  Circumradius = 2.375
  FirstAngle = 0
  Height = 1.29
  Placement = pos=(0,-10.325,-0.645) rot=(0,0,1;0rad)
  Polygon = 10
  SecondAngle = 0
FEATURE [Part::Box] cube046
  AttacherType = Attacher::AttachEngine3D
  Height = 1.29
  Length = 4.75
  Placement = pos=(-2.375,-10.325,-0.645) rot=(0,0,1;0rad)
  Width = 20.65
FEATURE [Part::MultiFuse] union045
  Placement = pos=(6.35,31.75,0) rot=(0,0,1;0rad)
  Shapes = -> [prism099,prism100,cube046]
FEATURE [Part::Prism] prism101
  AttacherType = Attacher::AttachEngine3D
  Circumradius = 2.375
  FirstAngle = 0
  Height = 1.29
  Placement = pos=(0,10.325,-0.645) rot=(0,0,1;0rad)
  Polygon = 10
  SecondAngle = 0
FEATURE [Part::Prism] prism102
  AttacherType = Attacher::AttachEngine3D
  Circumradius = 2.375
  FirstAngle = 0
  Height = 1.29
  Placement = pos=(0,-10.325,-0.645) rot=(0,0,1;0rad)
  Polygon = 10
  SecondAngle = 0
FEATURE [Part::Box] cube047
  AttacherType = Attacher::AttachEngine3D
  Height = 1.29
  Length = 4.75
  Placement = pos=(-2.375,-10.325,-0.645) rot=(0,0,1;0rad)
  Width = 20.65
FEATURE [Part::MultiFuse] union046
  Placement = pos=(19.05,31.75,0) rot=(0,0,1;0rad)
  Shapes = -> [prism101,prism102,cube047]
FEATURE [Part::Prism] prism103
  AttacherType = Attacher::AttachEngine3D
  Circumradius = 2.375
  FirstAngle = 0
  Height = 1.29
  Placement = pos=(0,10.325,-0.645) rot=(0,0,1;0rad)
  Polygon = 10
  SecondAngle = 0
FEATURE [Part::Prism] prism104
  AttacherType = Attacher::AttachEngine3D
  Circumradius = 2.375
  FirstAngle = 0
  Height = 1.29
  Placement = pos=(0,-10.325,-0.645) rot=(0,0,1;0rad)
  Polygon = 10
  SecondAngle = 0
FEATURE [Part::Box] cube048
  AttacherType = Attacher::AttachEngine3D
  Height = 1.29
  Length = 4.75
  Placement = pos=(-2.375,-10.325,-0.645) rot=(0,0,1;0rad)
  Width = 20.65
FEATURE [Part::MultiFuse] union047
  Placement = pos=(31.75,31.75,0) rot=(0,0,1;0rad)
  Shapes = -> [prism103,prism104,cube048]
FEATURE [Part::Prism] prism105
  AttacherType = Attacher::AttachEngine3D
  Circumradius = 2.375
  FirstAngle = 0
  Height = 1.29
  Placement = pos=(0,10.325,-0.645) rot=(0,0,1;0rad)
  Polygon = 10
  SecondAngle = 0
FEATURE [Part::Prism] prism106
  AttacherType = Attacher::AttachEngine3D
  Circumradius = 2.375
  FirstAngle = 0
  Height = 1.29
  Placement = pos=(0,-10.325,-0.645) rot=(0,0,1;0rad)
  Polygon = 10
  SecondAngle = 0
FEATURE [Part::Box] cube049
  AttacherType = Attacher::AttachEngine3D
  Height = 1.29
  Length = 4.75
  Placement = pos=(-2.375,-10.325,-0.645) rot=(0,0,1;0rad)
  Width = 20.65
FEATURE [Part::MultiFuse] union048
  Placement = pos=(44.45,31.75,0) rot=(0,0,1;0rad)
  Shapes = -> [prism105,prism106,cube049]
FEATURE [Part::Prism] prism107
  AttacherType = Attacher::AttachEngine3D
  Circumradius = 2.375
  FirstAngle = 0
  Height = 1.29
  Placement = pos=(0,10.325,-0.645) rot=(0,0,1;0rad)
  Polygon = 10
  SecondAngle = 0
FEATURE [Part::Prism] prism108
  AttacherType = Attacher::AttachEngine3D
  Circumradius = 2.375
  FirstAngle = 0
  Height = 1.29
  Placement = pos=(0,-10.325,-0.645) rot=(0,0,1;0rad)
  Polygon = 10
  SecondAngle = 0
FEATURE [Part::Box] cube050
  AttacherType = Attacher::AttachEngine3D
  Height = 1.29
  Length = 4.75
  Placement = pos=(-2.375,-10.325,-0.645) rot=(0,0,1;0rad)
  Width = 20.65
FEATURE [Part::MultiFuse] union049
  Placement = pos=(57.15,31.75,0) rot=(0,0,1;0rad)
  Shapes = -> [prism107,prism108,cube050]
FEATURE [Part::Prism] prism109
  AttacherType = Attacher::AttachEngine3D
  Circumradius = 2.375
  FirstAngle = 0
  Height = 1.29
  Placement = pos=(0,10.325,-0.645) rot=(0,0,1;0rad)
  Polygon = 10
  SecondAngle = 0
FEATURE [Part::Prism] prism110
  AttacherType = Attacher::AttachEngine3D
  Circumradius = 2.375
  FirstAngle = 0
  Height = 1.29
  Placement = pos=(0,-10.325,-0.645) rot=(0,0,1;0rad)
  Polygon = 10
  SecondAngle = 0
FEATURE [Part::Box] cube051
  AttacherType = Attacher::AttachEngine3D
  Height = 1.29
  Length = 4.75
  Placement = pos=(-2.375,-10.325,-0.645) rot=(0,0,1;0rad)
  Width = 20.65
FEATURE [Part::MultiFuse] union050
  Placement = pos=(69.85,31.75,0) rot=(0,0,1;0rad)
  Shapes = -> [prism109,prism110,cube051]
FEATURE [Part::Prism] prism111
  AttacherType = Attacher::AttachEngine3D
  Circumradius = 2.375
  FirstAngle = 0
  Height = 1.29
  Placement = pos=(0,10.325,-0.645) rot=(0,0,1;0rad)
  Polygon = 10
  SecondAngle = 0
FEATURE [Part::Prism] prism112
  AttacherType = Attacher::AttachEngine3D
  Circumradius = 2.375
  FirstAngle = 0
  Height = 1.29
  Placement = pos=(0,-10.325,-0.645) rot=(0,0,1;0rad)
  Polygon = 10
  SecondAngle = 0
FEATURE [Part::Box] cube052
  AttacherType = Attacher::AttachEngine3D
  Height = 1.29
  Length = 4.75
  Placement = pos=(-2.375,-10.325,-0.645) rot=(0,0,1;0rad)
  Width = 20.65
FEATURE [Part::MultiFuse] union051
  Placement = pos=(82.55,31.75,0) rot=(0,0,1;0rad)
  Shapes = -> [prism111,prism112,cube052]
FEATURE [Part::Prism] prism113
  AttacherType = Attacher::AttachEngine3D
  Circumradius = 2.375
  FirstAngle = 0
  Height = 1.29
  Placement = pos=(0,10.325,-0.645) rot=(0,0,1;0rad)
  Polygon = 10
  SecondAngle = 0
FEATURE [Part::Prism] prism114
  AttacherType = Attacher::AttachEngine3D
  Circumradius = 2.375
  FirstAngle = 0
  Height = 1.29
  Placement = pos=(0,-10.325,-0.645) rot=(0,0,1;0rad)
  Polygon = 10
  SecondAngle = 0
FEATURE [Part::Box] cube053
  AttacherType = Attacher::AttachEngine3D
  Height = 1.29
  Length = 4.75
  Placement = pos=(-2.375,-10.325,-0.645) rot=(0,0,1;0rad)
  Width = 20.65
FEATURE [Part::MultiFuse] union052
  Placement = pos=(95.25,31.75,0) rot=(0,0,1;0rad)
  Shapes = -> [prism113,prism114,cube053]
FEATURE [Part::Prism] prism115
  AttacherType = Attacher::AttachEngine3D
  Circumradius = 2.375
  FirstAngle = 0
  Height = 1.29
  Placement = pos=(0,10.325,-0.645) rot=(0,0,1;0rad)
  Polygon = 10
  SecondAngle = 0
FEATURE [Part::Prism] prism116
  AttacherType = Attacher::AttachEngine3D
  Circumradius = 2.375
  FirstAngle = 0
  Height = 1.29
  Placement = pos=(0,-10.325,-0.645) rot=(0,0,1;0rad)
  Polygon = 10
  SecondAngle = 0
FEATURE [Part::Box] cube054
  AttacherType = Attacher::AttachEngine3D
  Height = 1.29
  Length = 4.75
  Placement = pos=(-2.375,-10.325,-0.645) rot=(0,0,1;0rad)
  Width = 20.65
FEATURE [Part::MultiFuse] union053
  Placement = pos=(107.95,31.75,0) rot=(0,0,1;0rad)
  Shapes = -> [prism115,prism116,cube054]
FEATURE [Part::Prism] prism117
  AttacherType = Attacher::AttachEngine3D
  Circumradius = 2.375
  FirstAngle = 0
  Height = 1.29
  Placement = pos=(0,10.325,-0.645) rot=(0,0,1;0rad)
  Polygon = 10
  SecondAngle = 0
FEATURE [Part::Prism] prism118
  AttacherType = Attacher::AttachEngine3D
  Circumradius = 2.375
  FirstAngle = 0
  Height = 1.29
  Placement = pos=(0,-10.325,-0.645) rot=(0,0,1;0rad)
  Polygon = 10
  SecondAngle = 0
FEATURE [Part::Box] cube055
  AttacherType = Attacher::AttachEngine3D
  Height = 1.29
  Length = 4.75
  Placement = pos=(-2.375,-10.325,-0.645) rot=(0,0,1;0rad)
  Width = 20.65
FEATURE [Part::MultiFuse] union054
  Placement = pos=(120.65,31.75,0) rot=(0,0,1;0rad)
  Shapes = -> [prism117,prism118,cube055]
FEATURE [Part::Prism] prism119
  AttacherType = Attacher::AttachEngine3D
  Circumradius = 2.375
  FirstAngle = 0
  Height = 1.29
  Placement = pos=(0,10.325,-0.645) rot=(0,0,1;0rad)
  Polygon = 10
  SecondAngle = 0
FEATURE [Part::Prism] prism120
  AttacherType = Attacher::AttachEngine3D
  Circumradius = 2.375
  FirstAngle = 0
  Height = 1.29
  Placement = pos=(0,-10.325,-0.645) rot=(0,0,1;0rad)
  Polygon = 10
  SecondAngle = 0
FEATURE [Part::Box] cube056
  AttacherType = Attacher::AttachEngine3D
  Height = 1.29
  Length = 4.75
  Placement = pos=(-2.375,-10.325,-0.645) rot=(0,0,1;0rad)
  Width = 20.65
FEATURE [Part::MultiFuse] union055
  Placement = pos=(133.35,31.75,0) rot=(0,0,1;0rad)
  Shapes = -> [prism119,prism120,cube056]
FEATURE [Part::Prism] prism121
  AttacherType = Attacher::AttachEngine3D
  Circumradius = 2.375
  FirstAngle = 0
  Height = 1.29
  Placement = pos=(0,10.325,-0.645) rot=(0,0,1;0rad)
  Polygon = 10
  SecondAngle = 0
FEATURE [Part::Prism] prism122
  AttacherType = Attacher::AttachEngine3D
  Circumradius = 2.375
  FirstAngle = 0
  Height = 1.29
  Placement = pos=(0,-10.325,-0.645) rot=(0,0,1;0rad)
  Polygon = 10
  SecondAngle = 0
FEATURE [Part::Box] cube057
  AttacherType = Attacher::AttachEngine3D
  Height = 1.29
  Length = 4.75
  Placement = pos=(-2.375,-10.325,-0.645) rot=(0,0,1;0rad)
  Width = 20.65
FEATURE [Part::MultiFuse] union056
  Placement = pos=(146.05,31.75,0) rot=(0,0,1;0rad)
  Shapes = -> [prism121,prism122,cube057]
FEATURE [Part::Prism] prism123
  AttacherType = Attacher::AttachEngine3D
  Circumradius = 2.375
  FirstAngle = 0
  Height = 1.29
  Placement = pos=(0,10.325,-0.645) rot=(0,0,1;0rad)
  Polygon = 10
  SecondAngle = 0
FEATURE [Part::Prism] prism124
  AttacherType = Attacher::AttachEngine3D
  Circumradius = 2.375
  FirstAngle = 0
  Height = 1.29
  Placement = pos=(0,-10.325,-0.645) rot=(0,0,1;0rad)
  Polygon = 10
  SecondAngle = 0
FEATURE [Part::Box] cube058
  AttacherType = Attacher::AttachEngine3D
  Height = 1.29
  Length = 4.75
  Placement = pos=(-2.375,-10.325,-0.645) rot=(0,0,1;0rad)
  Width = 20.65
FEATURE [Part::MultiFuse] union057
  Placement = pos=(158.75,31.75,0) rot=(0,0,1;0rad)
  Shapes = -> [prism123,prism124,cube058]
FEATURE [Part::Prism] prism125
  AttacherType = Attacher::AttachEngine3D
  Circumradius = 2.375
  FirstAngle = 0
  Height = 1.29
  Placement = pos=(0,10.325,-0.645) rot=(0,0,1;0rad)
  Polygon = 10
  SecondAngle = 0
FEATURE [Part::Prism] prism126
  AttacherType = Attacher::AttachEngine3D
  Circumradius = 2.375
  FirstAngle = 0
  Height = 1.29
  Placement = pos=(0,-10.325,-0.645) rot=(0,0,1;0rad)
  Polygon = 10
  SecondAngle = 0
FEATURE [Part::Box] cube059
  AttacherType = Attacher::AttachEngine3D
  Height = 1.29
  Length = 4.75
  Placement = pos=(-2.375,-10.325,-0.645) rot=(0,0,1;0rad)
  Width = 20.65
FEATURE [Part::MultiFuse] union058
  Placement = pos=(171.45,31.75,0) rot=(0,0,1;0rad)
  Shapes = -> [prism125,prism126,cube059]
FEATURE [Part::Prism] prism127
  AttacherType = Attacher::AttachEngine3D
  Circumradius = 2.375
  FirstAngle = 0
  Height = 1.29
  Placement = pos=(0,10.325,-0.645) rot=(0,0,1;0rad)
  Polygon = 10
  SecondAngle = 0
FEATURE [Part::Prism] prism128
  AttacherType = Attacher::AttachEngine3D
  Circumradius = 2.375
  FirstAngle = 0
  Height = 1.29
  Placement = pos=(0,-10.325,-0.645) rot=(0,0,1;0rad)
  Polygon = 10
  SecondAngle = 0
FEATURE [Part::Box] cube060
  AttacherType = Attacher::AttachEngine3D
  Height = 1.29
  Length = 4.75
  Placement = pos=(-2.375,-10.325,-0.645) rot=(0,0,1;0rad)
  Width = 20.65
FEATURE [Part::MultiFuse] union059
  Placement = pos=(184.15,31.75,0) rot=(0,0,1;0rad)
  Shapes = -> [prism127,prism128,cube060]
FEATURE [Part::MultiFuse] Group001
  Shapes = -> [union030,union031,union032,union033,union034,union035,union036,union037,union038,union039,union040,union041,union042,union043,union044,union045,union046,union047,union048,union049,union050,union051,union052,union053,union054,union055,union056,union057,union058,union059]
FEATURE [Part::Prism] prism129
  AttacherType = Attacher::AttachEngine3D
  Circumradius = 2.375
  FirstAngle = 0
  Height = 1.29
  Placement = pos=(0,10.325,-0.645) rot=(0,0,1;0rad)
  Polygon = 10
  SecondAngle = 0
FEATURE [Part::Prism] prism130
  AttacherType = Attacher::AttachEngine3D
  Circumradius = 2.375
  FirstAngle = 0
  Height = 1.29
  Placement = pos=(0,-10.325,-0.645) rot=(0,0,1;0rad)
  Polygon = 10
  SecondAngle = 0
FEATURE [Part::Box] cube061
  AttacherType = Attacher::AttachEngine3D
  Height = 1.29
  Length = 4.75
  Placement = pos=(-2.375,-10.325,-0.645) rot=(0,0,1;0rad)
  Width = 20.65
FEATURE [Part::MultiFuse] union060
  Placement = pos=(-184.15,0,0) rot=(0,0,1;0rad)
  Shapes = -> [prism129,prism130,cube061]
FEATURE [Part::Prism] prism131
  AttacherType = Attacher::AttachEngine3D
  Circumradius = 2.375
  FirstAngle = 0
  Height = 1.29
  Placement = pos=(0,10.325,-0.645) rot=(0,0,1;0rad)
  Polygon = 10
  SecondAngle = 0
FEATURE [Part::Prism] prism132
  AttacherType = Attacher::AttachEngine3D
  Circumradius = 2.375
  FirstAngle = 0
  Height = 1.29
  Placement = pos=(0,-10.325,-0.645) rot=(0,0,1;0rad)
  Polygon = 10
  SecondAngle = 0
FEATURE [Part::Box] cube062
  AttacherType = Attacher::AttachEngine3D
  Height = 1.29
  Length = 4.75
  Placement = pos=(-2.375,-10.325,-0.645) rot=(0,0,1;0rad)
  Width = 20.65
FEATURE [Part::MultiFuse] union061
  Placement = pos=(-171.45,0,0) rot=(0,0,1;0rad)
  Shapes = -> [prism131,prism132,cube062]
FEATURE [Part::Prism] prism133
  AttacherType = Attacher::AttachEngine3D
  Circumradius = 2.375
  FirstAngle = 0
  Height = 1.29
  Placement = pos=(0,10.325,-0.645) rot=(0,0,1;0rad)
  Polygon = 10
  SecondAngle = 0
FEATURE [Part::Prism] prism134
  AttacherType = Attacher::AttachEngine3D
  Circumradius = 2.375
  FirstAngle = 0
  Height = 1.29
  Placement = pos=(0,-10.325,-0.645) rot=(0,0,1;0rad)
  Polygon = 10
  SecondAngle = 0
FEATURE [Part::Box] cube063
  AttacherType = Attacher::AttachEngine3D
  Height = 1.29
  Length = 4.75
  Placement = pos=(-2.375,-10.325,-0.645) rot=(0,0,1;0rad)
  Width = 20.65
FEATURE [Part::MultiFuse] union062
  Placement = pos=(-158.75,0,0) rot=(0,0,1;0rad)
  Shapes = -> [prism133,prism134,cube063]
FEATURE [Part::Prism] prism135
  AttacherType = Attacher::AttachEngine3D
  Circumradius = 2.375
  FirstAngle = 0
  Height = 1.29
  Placement = pos=(0,10.325,-0.645) rot=(0,0,1;0rad)
  Polygon = 10
  SecondAngle = 0
FEATURE [Part::Prism] prism136
  AttacherType = Attacher::AttachEngine3D
  Circumradius = 2.375
  FirstAngle = 0
  Height = 1.29
  Placement = pos=(0,-10.325,-0.645) rot=(0,0,1;0rad)
  Polygon = 10
  SecondAngle = 0
FEATURE [Part::Box] cube064
  AttacherType = Attacher::AttachEngine3D
  Height = 1.29
  Length = 4.75
  Placement = pos=(-2.375,-10.325,-0.645) rot=(0,0,1;0rad)
  Width = 20.65
FEATURE [Part::MultiFuse] union063
  Placement = pos=(-146.05,0,0) rot=(0,0,1;0rad)
  Shapes = -> [prism135,prism136,cube064]
FEATURE [Part::Prism] prism137
  AttacherType = Attacher::AttachEngine3D
  Circumradius = 2.375
  FirstAngle = 0
  Height = 1.29
  Placement = pos=(0,10.325,-0.645) rot=(0,0,1;0rad)
  Polygon = 10
  SecondAngle = 0
FEATURE [Part::Prism] prism138
  AttacherType = Attacher::AttachEngine3D
  Circumradius = 2.375
  FirstAngle = 0
  Height = 1.29
  Placement = pos=(0,-10.325,-0.645) rot=(0,0,1;0rad)
  Polygon = 10
  SecondAngle = 0
FEATURE [Part::Box] cube065
  AttacherType = Attacher::AttachEngine3D
  Height = 1.29
  Length = 4.75
  Placement = pos=(-2.375,-10.325,-0.645) rot=(0,0,1;0rad)
  Width = 20.65
FEATURE [Part::MultiFuse] union064
  Placement = pos=(-133.35,0,0) rot=(0,0,1;0rad)
  Shapes = -> [prism137,prism138,cube065]
FEATURE [Part::Prism] prism139
  AttacherType = Attacher::AttachEngine3D
  Circumradius = 2.375
  FirstAngle = 0
  Height = 1.29
  Placement = pos=(0,10.325,-0.645) rot=(0,0,1;0rad)
  Polygon = 10
  SecondAngle = 0
FEATURE [Part::Prism] prism140
  AttacherType = Attacher::AttachEngine3D
  Circumradius = 2.375
  FirstAngle = 0
  Height = 1.29
  Placement = pos=(0,-10.325,-0.645) rot=(0,0,1;0rad)
  Polygon = 10
  SecondAngle = 0
FEATURE [Part::Box] cube066
  AttacherType = Attacher::AttachEngine3D
  Height = 1.29
  Length = 4.75
  Placement = pos=(-2.375,-10.325,-0.645) rot=(0,0,1;0rad)
  Width = 20.65
FEATURE [Part::MultiFuse] union065
  Placement = pos=(-120.65,0,0) rot=(0,0,1;0rad)
  Shapes = -> [prism139,prism140,cube066]
FEATURE [Part::Prism] prism141
  AttacherType = Attacher::AttachEngine3D
  Circumradius = 2.375
  FirstAngle = 0
  Height = 1.29
  Placement = pos=(0,10.325,-0.645) rot=(0,0,1;0rad)
  Polygon = 10
  SecondAngle = 0
FEATURE [Part::Prism] prism142
  AttacherType = Attacher::AttachEngine3D
  Circumradius = 2.375
  FirstAngle = 0
  Height = 1.29
  Placement = pos=(0,-10.325,-0.645) rot=(0,0,1;0rad)
  Polygon = 10
  SecondAngle = 0
FEATURE [Part::Box] cube067
  AttacherType = Attacher::AttachEngine3D
  Height = 1.29
  Length = 4.75
  Placement = pos=(-2.375,-10.325,-0.645) rot=(0,0,1;0rad)
  Width = 20.65
FEATURE [Part::MultiFuse] union066
  Placement = pos=(-107.95,0,0) rot=(0,0,1;0rad)
  Shapes = -> [prism141,prism142,cube067]
FEATURE [Part::Prism] prism143
  AttacherType = Attacher::AttachEngine3D
  Circumradius = 2.375
  FirstAngle = 0
  Height = 1.29
  Placement = pos=(0,10.325,-0.645) rot=(0,0,1;0rad)
  Polygon = 10
  SecondAngle = 0
FEATURE [Part::Prism] prism144
  AttacherType = Attacher::AttachEngine3D
  Circumradius = 2.375
  FirstAngle = 0
  Height = 1.29
  Placement = pos=(0,-10.325,-0.645) rot=(0,0,1;0rad)
  Polygon = 10
  SecondAngle = 0
FEATURE [Part::Box] cube068
  AttacherType = Attacher::AttachEngine3D
  Height = 1.29
  Length = 4.75
  Placement = pos=(-2.375,-10.325,-0.645) rot=(0,0,1;0rad)
  Width = 20.65
FEATURE [Part::MultiFuse] union067
  Placement = pos=(-95.25,0,0) rot=(0,0,1;0rad)
  Shapes = -> [prism143,prism144,cube068]
FEATURE [Part::Prism] prism145
  AttacherType = Attacher::AttachEngine3D
  Circumradius = 2.375
  FirstAngle = 0
  Height = 1.29
  Placement = pos=(0,10.325,-0.645) rot=(0,0,1;0rad)
  Polygon = 10
  SecondAngle = 0
FEATURE [Part::Prism] prism146
  AttacherType = Attacher::AttachEngine3D
  Circumradius = 2.375
  FirstAngle = 0
  Height = 1.29
  Placement = pos=(0,-10.325,-0.645) rot=(0,0,1;0rad)
  Polygon = 10
  SecondAngle = 0
FEATURE [Part::Box] cube069
  AttacherType = Attacher::AttachEngine3D
  Height = 1.29
  Length = 4.75
  Placement = pos=(-2.375,-10.325,-0.645) rot=(0,0,1;0rad)
  Width = 20.65
FEATURE [Part::MultiFuse] union068
  Placement = pos=(-82.55,0,0) rot=(0,0,1;0rad)
  Shapes = -> [prism145,prism146,cube069]
FEATURE [Part::Prism] prism147
  AttacherType = Attacher::AttachEngine3D
  Circumradius = 2.375
  FirstAngle = 0
  Height = 1.29
  Placement = pos=(0,10.325,-0.645) rot=(0,0,1;0rad)
  Polygon = 10
  SecondAngle = 0
FEATURE [Part::Prism] prism148
  AttacherType = Attacher::AttachEngine3D
  Circumradius = 2.375
  FirstAngle = 0
  Height = 1.29
  Placement = pos=(0,-10.325,-0.645) rot=(0,0,1;0rad)
  Polygon = 10
  SecondAngle = 0
FEATURE [Part::Box] cube070
  AttacherType = Attacher::AttachEngine3D
  Height = 1.29
  Length = 4.75
  Placement = pos=(-2.375,-10.325,-0.645) rot=(0,0,1;0rad)
  Width = 20.65
FEATURE [Part::MultiFuse] union069
  Placement = pos=(-69.85,0,0) rot=(0,0,1;0rad)
  Shapes = -> [prism147,prism148,cube070]
FEATURE [Part::Prism] prism149
  AttacherType = Attacher::AttachEngine3D
  Circumradius = 2.375
  FirstAngle = 0
  Height = 1.29
  Placement = pos=(0,10.325,-0.645) rot=(0,0,1;0rad)
  Polygon = 10
  SecondAngle = 0
FEATURE [Part::Prism] prism150
  AttacherType = Attacher::AttachEngine3D
  Circumradius = 2.375
  FirstAngle = 0
  Height = 1.29
  Placement = pos=(0,-10.325,-0.645) rot=(0,0,1;0rad)
  Polygon = 10
  SecondAngle = 0
FEATURE [Part::Box] cube071
  AttacherType = Attacher::AttachEngine3D
  Height = 1.29
  Length = 4.75
  Placement = pos=(-2.375,-10.325,-0.645) rot=(0,0,1;0rad)
  Width = 20.65
FEATURE [Part::MultiFuse] union070
  Placement = pos=(-57.15,0,0) rot=(0,0,1;0rad)
  Shapes = -> [prism149,prism150,cube071]
FEATURE [Part::Prism] prism151
  AttacherType = Attacher::AttachEngine3D
  Circumradius = 2.375
  FirstAngle = 0
  Height = 1.29
  Placement = pos=(0,10.325,-0.645) rot=(0,0,1;0rad)
  Polygon = 10
  SecondAngle = 0
FEATURE [Part::Prism] prism152
  AttacherType = Attacher::AttachEngine3D
  Circumradius = 2.375
  FirstAngle = 0
  Height = 1.29
  Placement = pos=(0,-10.325,-0.645) rot=(0,0,1;0rad)
  Polygon = 10
  SecondAngle = 0
FEATURE [Part::Box] cube072
  AttacherType = Attacher::AttachEngine3D
  Height = 1.29
  Length = 4.75
  Placement = pos=(-2.375,-10.325,-0.645) rot=(0,0,1;0rad)
  Width = 20.65
FEATURE [Part::MultiFuse] union071
  Placement = pos=(-44.45,0,0) rot=(0,0,1;0rad)
  Shapes = -> [prism151,prism152,cube072]
FEATURE [Part::Prism] prism153
  AttacherType = Attacher::AttachEngine3D
  Circumradius = 2.375
  FirstAngle = 0
  Height = 1.29
  Placement = pos=(0,10.325,-0.645) rot=(0,0,1;0rad)
  Polygon = 10
  SecondAngle = 0
FEATURE [Part::Prism] prism154
  AttacherType = Attacher::AttachEngine3D
  Circumradius = 2.375
  FirstAngle = 0
  Height = 1.29
  Placement = pos=(0,-10.325,-0.645) rot=(0,0,1;0rad)
  Polygon = 10
  SecondAngle = 0
FEATURE [Part::Box] cube073
  AttacherType = Attacher::AttachEngine3D
  Height = 1.29
  Length = 4.75
  Placement = pos=(-2.375,-10.325,-0.645) rot=(0,0,1;0rad)
  Width = 20.65
FEATURE [Part::MultiFuse] union072
  Placement = pos=(-31.75,0,0) rot=(0,0,1;0rad)
  Shapes = -> [prism153,prism154,cube073]
FEATURE [Part::Prism] prism155
  AttacherType = Attacher::AttachEngine3D
  Circumradius = 2.375
  FirstAngle = 0
  Height = 1.29
  Placement = pos=(0,10.325,-0.645) rot=(0,0,1;0rad)
  Polygon = 10
  SecondAngle = 0
FEATURE [Part::Prism] prism156
  AttacherType = Attacher::AttachEngine3D
  Circumradius = 2.375
  FirstAngle = 0
  Height = 1.29
  Placement = pos=(0,-10.325,-0.645) rot=(0,0,1;0rad)
  Polygon = 10
  SecondAngle = 0
FEATURE [Part::Box] cube074
  AttacherType = Attacher::AttachEngine3D
  Height = 1.29
  Length = 4.75
  Placement = pos=(-2.375,-10.325,-0.645) rot=(0,0,1;0rad)
  Width = 20.65
FEATURE [Part::MultiFuse] union073
  Placement = pos=(-19.05,0,0) rot=(0,0,1;0rad)
  Shapes = -> [prism155,prism156,cube074]
FEATURE [Part::Prism] prism157
  AttacherType = Attacher::AttachEngine3D
  Circumradius = 2.375
  FirstAngle = 0
  Height = 1.29
  Placement = pos=(0,10.325,-0.645) rot=(0,0,1;0rad)
  Polygon = 10
  SecondAngle = 0
FEATURE [Part::Prism] prism158
  AttacherType = Attacher::AttachEngine3D
  Circumradius = 2.375
  FirstAngle = 0
  Height = 1.29
  Placement = pos=(0,-10.325,-0.645) rot=(0,0,1;0rad)
  Polygon = 10
  SecondAngle = 0
FEATURE [Part::Box] cube075
  AttacherType = Attacher::AttachEngine3D
  Height = 1.29
  Length = 4.75
  Placement = pos=(-2.375,-10.325,-0.645) rot=(0,0,1;0rad)
  Width = 20.65
FEATURE [Part::MultiFuse] union074
  Placement = pos=(-6.35,0,0) rot=(0,0,1;0rad)
  Shapes = -> [prism157,prism158,cube075]
FEATURE [Part::Prism] prism159
  AttacherType = Attacher::AttachEngine3D
  Circumradius = 2.375
  FirstAngle = 0
  Height = 1.29
  Placement = pos=(0,10.325,-0.645) rot=(0,0,1;0rad)
  Polygon = 10
  SecondAngle = 0
FEATURE [Part::Prism] prism160
  AttacherType = Attacher::AttachEngine3D
  Circumradius = 2.375
  FirstAngle = 0
  Height = 1.29
  Placement = pos=(0,-10.325,-0.645) rot=(0,0,1;0rad)
  Polygon = 10
  SecondAngle = 0
FEATURE [Part::Box] cube076
  AttacherType = Attacher::AttachEngine3D
  Height = 1.29
  Length = 4.75
  Placement = pos=(-2.375,-10.325,-0.645) rot=(0,0,1;0rad)
  Width = 20.65
FEATURE [Part::MultiFuse] union075
  Placement = pos=(6.35,0,0) rot=(0,0,1;0rad)
  Shapes = -> [prism159,prism160,cube076]
FEATURE [Part::Prism] prism161
  AttacherType = Attacher::AttachEngine3D
  Circumradius = 2.375
  FirstAngle = 0
  Height = 1.29
  Placement = pos=(0,10.325,-0.645) rot=(0,0,1;0rad)
  Polygon = 10
  SecondAngle = 0
FEATURE [Part::Prism] prism162
  AttacherType = Attacher::AttachEngine3D
  Circumradius = 2.375
  FirstAngle = 0
  Height = 1.29
  Placement = pos=(0,-10.325,-0.645) rot=(0,0,1;0rad)
  Polygon = 10
  SecondAngle = 0
FEATURE [Part::Box] cube077
  AttacherType = Attacher::AttachEngine3D
  Height = 1.29
  Length = 4.75
  Placement = pos=(-2.375,-10.325,-0.645) rot=(0,0,1;0rad)
  Width = 20.65
FEATURE [Part::MultiFuse] union076
  Placement = pos=(19.05,0,0) rot=(0,0,1;0rad)
  Shapes = -> [prism161,prism162,cube077]
FEATURE [Part::Prism] prism163
  AttacherType = Attacher::AttachEngine3D
  Circumradius = 2.375
  FirstAngle = 0
  Height = 1.29
  Placement = pos=(0,10.325,-0.645) rot=(0,0,1;0rad)
  Polygon = 10
  SecondAngle = 0
FEATURE [Part::Prism] prism164
  AttacherType = Attacher::AttachEngine3D
  Circumradius = 2.375
  FirstAngle = 0
  Height = 1.29
  Placement = pos=(0,-10.325,-0.645) rot=(0,0,1;0rad)
  Polygon = 10
  SecondAngle = 0
FEATURE [Part::Box] cube078
  AttacherType = Attacher::AttachEngine3D
  Height = 1.29
  Length = 4.75
  Placement = pos=(-2.375,-10.325,-0.645) rot=(0,0,1;0rad)
  Width = 20.65
FEATURE [Part::MultiFuse] union077
  Placement = pos=(31.75,0,0) rot=(0,0,1;0rad)
  Shapes = -> [prism163,prism164,cube078]
FEATURE [Part::Prism] prism165
  AttacherType = Attacher::AttachEngine3D
  Circumradius = 2.375
  FirstAngle = 0
  Height = 1.29
  Placement = pos=(0,10.325,-0.645) rot=(0,0,1;0rad)
  Polygon = 10
  SecondAngle = 0
FEATURE [Part::Prism] prism166
  AttacherType = Attacher::AttachEngine3D
  Circumradius = 2.375
  FirstAngle = 0
  Height = 1.29
  Placement = pos=(0,-10.325,-0.645) rot=(0,0,1;0rad)
  Polygon = 10
  SecondAngle = 0
FEATURE [Part::Box] cube079
  AttacherType = Attacher::AttachEngine3D
  Height = 1.29
  Length = 4.75
  Placement = pos=(-2.375,-10.325,-0.645) rot=(0,0,1;0rad)
  Width = 20.65
FEATURE [Part::MultiFuse] union078
  Placement = pos=(44.45,0,0) rot=(0,0,1;0rad)
  Shapes = -> [prism165,prism166,cube079]
FEATURE [Part::Prism] prism167
  AttacherType = Attacher::AttachEngine3D
  Circumradius = 2.375
  FirstAngle = 0
  Height = 1.29
  Placement = pos=(0,10.325,-0.645) rot=(0,0,1;0rad)
  Polygon = 10
  SecondAngle = 0
FEATURE [Part::Prism] prism168
  AttacherType = Attacher::AttachEngine3D
  Circumradius = 2.375
  FirstAngle = 0
  Height = 1.29
  Placement = pos=(0,-10.325,-0.645) rot=(0,0,1;0rad)
  Polygon = 10
  SecondAngle = 0
FEATURE [Part::Box] cube080
  AttacherType = Attacher::AttachEngine3D
  Height = 1.29
  Length = 4.75
  Placement = pos=(-2.375,-10.325,-0.645) rot=(0,0,1;0rad)
  Width = 20.65
FEATURE [Part::MultiFuse] union079
  Placement = pos=(57.15,0,0) rot=(0,0,1;0rad)
  Shapes = -> [prism167,prism168,cube080]
FEATURE [Part::Prism] prism169
  AttacherType = Attacher::AttachEngine3D
  Circumradius = 2.375
  FirstAngle = 0
  Height = 1.29
  Placement = pos=(0,10.325,-0.645) rot=(0,0,1;0rad)
  Polygon = 10
  SecondAngle = 0
FEATURE [Part::Prism] prism170
  AttacherType = Attacher::AttachEngine3D
  Circumradius = 2.375
  FirstAngle = 0
  Height = 1.29
  Placement = pos=(0,-10.325,-0.645) rot=(0,0,1;0rad)
  Polygon = 10
  SecondAngle = 0
FEATURE [Part::Box] cube081
  AttacherType = Attacher::AttachEngine3D
  Height = 1.29
  Length = 4.75
  Placement = pos=(-2.375,-10.325,-0.645) rot=(0,0,1;0rad)
  Width = 20.65
FEATURE [Part::MultiFuse] union080
  Placement = pos=(69.85,0,0) rot=(0,0,1;0rad)
  Shapes = -> [prism169,prism170,cube081]
FEATURE [Part::Prism] prism171
  AttacherType = Attacher::AttachEngine3D
  Circumradius = 2.375
  FirstAngle = 0
  Height = 1.29
  Placement = pos=(0,10.325,-0.645) rot=(0,0,1;0rad)
  Polygon = 10
  SecondAngle = 0
FEATURE [Part::Prism] prism172
  AttacherType = Attacher::AttachEngine3D
  Circumradius = 2.375
  FirstAngle = 0
  Height = 1.29
  Placement = pos=(0,-10.325,-0.645) rot=(0,0,1;0rad)
  Polygon = 10
  SecondAngle = 0
FEATURE [Part::Box] cube082
  AttacherType = Attacher::AttachEngine3D
  Height = 1.29
  Length = 4.75
  Placement = pos=(-2.375,-10.325,-0.645) rot=(0,0,1;0rad)
  Width = 20.65
FEATURE [Part::MultiFuse] union081
  Placement = pos=(82.55,0,0) rot=(0,0,1;0rad)
  Shapes = -> [prism171,prism172,cube082]
FEATURE [Part::Prism] prism173
  AttacherType = Attacher::AttachEngine3D
  Circumradius = 2.375
  FirstAngle = 0
  Height = 1.29
  Placement = pos=(0,10.325,-0.645) rot=(0,0,1;0rad)
  Polygon = 10
  SecondAngle = 0
FEATURE [Part::Prism] prism174
  AttacherType = Attacher::AttachEngine3D
  Circumradius = 2.375
  FirstAngle = 0
  Height = 1.29
  Placement = pos=(0,-10.325,-0.645) rot=(0,0,1;0rad)
  Polygon = 10
  SecondAngle = 0
FEATURE [Part::Box] cube083
  AttacherType = Attacher::AttachEngine3D
  Height = 1.29
  Length = 4.75
  Placement = pos=(-2.375,-10.325,-0.645) rot=(0,0,1;0rad)
  Width = 20.65
FEATURE [Part::MultiFuse] union082
  Placement = pos=(95.25,0,0) rot=(0,0,1;0rad)
  Shapes = -> [prism173,prism174,cube083]
FEATURE [Part::Prism] prism175
  AttacherType = Attacher::AttachEngine3D
  Circumradius = 2.375
  FirstAngle = 0
  Height = 1.29
  Placement = pos=(0,10.325,-0.645) rot=(0,0,1;0rad)
  Polygon = 10
  SecondAngle = 0
FEATURE [Part::Prism] prism176
  AttacherType = Attacher::AttachEngine3D
  Circumradius = 2.375
  FirstAngle = 0
  Height = 1.29
  Placement = pos=(0,-10.325,-0.645) rot=(0,0,1;0rad)
  Polygon = 10
  SecondAngle = 0
FEATURE [Part::Box] cube084
  AttacherType = Attacher::AttachEngine3D
  Height = 1.29
  Length = 4.75
  Placement = pos=(-2.375,-10.325,-0.645) rot=(0,0,1;0rad)
  Width = 20.65
FEATURE [Part::MultiFuse] union083
  Placement = pos=(107.95,0,0) rot=(0,0,1;0rad)
  Shapes = -> [prism175,prism176,cube084]
FEATURE [Part::Prism] prism177
  AttacherType = Attacher::AttachEngine3D
  Circumradius = 2.375
  FirstAngle = 0
  Height = 1.29
  Placement = pos=(0,10.325,-0.645) rot=(0,0,1;0rad)
  Polygon = 10
  SecondAngle = 0
FEATURE [Part::Prism] prism178
  AttacherType = Attacher::AttachEngine3D
  Circumradius = 2.375
  FirstAngle = 0
  Height = 1.29
  Placement = pos=(0,-10.325,-0.645) rot=(0,0,1;0rad)
  Polygon = 10
  SecondAngle = 0
FEATURE [Part::Box] cube085
  AttacherType = Attacher::AttachEngine3D
  Height = 1.29
  Length = 4.75
  Placement = pos=(-2.375,-10.325,-0.645) rot=(0,0,1;0rad)
  Width = 20.65
FEATURE [Part::MultiFuse] union084
  Placement = pos=(120.65,0,0) rot=(0,0,1;0rad)
  Shapes = -> [prism177,prism178,cube085]
FEATURE [Part::Prism] prism179
  AttacherType = Attacher::AttachEngine3D
  Circumradius = 2.375
  FirstAngle = 0
  Height = 1.29
  Placement = pos=(0,10.325,-0.645) rot=(0,0,1;0rad)
  Polygon = 10
  SecondAngle = 0
FEATURE [Part::Prism] prism180
  AttacherType = Attacher::AttachEngine3D
  Circumradius = 2.375
  FirstAngle = 0
  Height = 1.29
  Placement = pos=(0,-10.325,-0.645) rot=(0,0,1;0rad)
  Polygon = 10
  SecondAngle = 0
FEATURE [Part::Box] cube086
  AttacherType = Attacher::AttachEngine3D
  Height = 1.29
  Length = 4.75
  Placement = pos=(-2.375,-10.325,-0.645) rot=(0,0,1;0rad)
  Width = 20.65
FEATURE [Part::MultiFuse] union085
  Placement = pos=(133.35,0,0) rot=(0,0,1;0rad)
  Shapes = -> [prism179,prism180,cube086]
FEATURE [Part::Prism] prism181
  AttacherType = Attacher::AttachEngine3D
  Circumradius = 2.375
  FirstAngle = 0
  Height = 1.29
  Placement = pos=(0,10.325,-0.645) rot=(0,0,1;0rad)
  Polygon = 10
  SecondAngle = 0
FEATURE [Part::Prism] prism182
  AttacherType = Attacher::AttachEngine3D
  Circumradius = 2.375
  FirstAngle = 0
  Height = 1.29
  Placement = pos=(0,-10.325,-0.645) rot=(0,0,1;0rad)
  Polygon = 10
  SecondAngle = 0
FEATURE [Part::Box] cube087
  AttacherType = Attacher::AttachEngine3D
  Height = 1.29
  Length = 4.75
  Placement = pos=(-2.375,-10.325,-0.645) rot=(0,0,1;0rad)
  Width = 20.65
FEATURE [Part::MultiFuse] union086
  Placement = pos=(146.05,0,0) rot=(0,0,1;0rad)
  Shapes = -> [prism181,prism182,cube087]
FEATURE [Part::Prism] prism183
  AttacherType = Attacher::AttachEngine3D
  Circumradius = 2.375
  FirstAngle = 0
  Height = 1.29
  Placement = pos=(0,10.325,-0.645) rot=(0,0,1;0rad)
  Polygon = 10
  SecondAngle = 0
FEATURE [Part::Prism] prism184
  AttacherType = Attacher::AttachEngine3D
  Circumradius = 2.375
  FirstAngle = 0
  Height = 1.29
  Placement = pos=(0,-10.325,-0.645) rot=(0,0,1;0rad)
  Polygon = 10
  SecondAngle = 0
FEATURE [Part::Box] cube088
  AttacherType = Attacher::AttachEngine3D
  Height = 1.29
  Length = 4.75
  Placement = pos=(-2.375,-10.325,-0.645) rot=(0,0,1;0rad)
  Width = 20.65
FEATURE [Part::MultiFuse] union087
  Placement = pos=(158.75,0,0) rot=(0,0,1;0rad)
  Shapes = -> [prism183,prism184,cube088]
FEATURE [Part::Prism] prism185
  AttacherType = Attacher::AttachEngine3D
  Circumradius = 2.375
  FirstAngle = 0
  Height = 1.29
  Placement = pos=(0,10.325,-0.645) rot=(0,0,1;0rad)
  Polygon = 10
  SecondAngle = 0
FEATURE [Part::Prism] prism186
  AttacherType = Attacher::AttachEngine3D
  Circumradius = 2.375
  FirstAngle = 0
  Height = 1.29
  Placement = pos=(0,-10.325,-0.645) rot=(0,0,1;0rad)
  Polygon = 10
  SecondAngle = 0
FEATURE [Part::Box] cube089
  AttacherType = Attacher::AttachEngine3D
  Height = 1.29
  Length = 4.75
  Placement = pos=(-2.375,-10.325,-0.645) rot=(0,0,1;0rad)
  Width = 20.65
FEATURE [Part::MultiFuse] union088
  Placement = pos=(171.45,0,0) rot=(0,0,1;0rad)
  Shapes = -> [prism185,prism186,cube089]
FEATURE [Part::Prism] prism187
  AttacherType = Attacher::AttachEngine3D
  Circumradius = 2.375
  FirstAngle = 0
  Height = 1.29
  Placement = pos=(0,10.325,-0.645) rot=(0,0,1;0rad)
  Polygon = 10
  SecondAngle = 0
FEATURE [Part::Prism] prism188
  AttacherType = Attacher::AttachEngine3D
  Circumradius = 2.375
  FirstAngle = 0
  Height = 1.29
  Placement = pos=(0,-10.325,-0.645) rot=(0,0,1;0rad)
  Polygon = 10
  SecondAngle = 0
FEATURE [Part::Box] cube090
  AttacherType = Attacher::AttachEngine3D
  Height = 1.29
  Length = 4.75
  Placement = pos=(-2.375,-10.325,-0.645) rot=(0,0,1;0rad)
  Width = 20.65
FEATURE [Part::MultiFuse] union089
  Placement = pos=(184.15,0,0) rot=(0,0,1;0rad)
  Shapes = -> [prism187,prism188,cube090]
FEATURE [Part::MultiFuse] Group002
  Shapes = -> [union060,union061,union062,union063,union064,union065,union066,union067,union068,union069,union070,union071,union072,union073,union074,union075,union076,union077,union078,union079,union080,union081,union082,union083,union084,union085,union086,union087,union088,union089]
FEATURE [Part::Prism] prism189
  AttacherType = Attacher::AttachEngine3D
  Circumradius = 2.375
  FirstAngle = 0
  Height = 1.29
  Placement = pos=(0,10.325,-0.645) rot=(0,0,1;0rad)
  Polygon = 10
  SecondAngle = 0
FEATURE [Part::Prism] prism190
  AttacherType = Attacher::AttachEngine3D
  Circumradius = 2.375
  FirstAngle = 0
  Height = 1.29
  Placement = pos=(0,-10.325,-0.645) rot=(0,0,1;0rad)
  Polygon = 10
  SecondAngle = 0
FEATURE [Part::Box] cube091
  AttacherType = Attacher::AttachEngine3D
  Height = 1.29
  Length = 4.75
  Placement = pos=(-2.375,-10.325,-0.645) rot=(0,0,1;0rad)
  Width = 20.65
FEATURE [Part::MultiFuse] union090
  Placement = pos=(-184.15,-31.75,0) rot=(0,0,1;0rad)
  Shapes = -> [prism189,prism190,cube091]
FEATURE [Part::Prism] prism191
  AttacherType = Attacher::AttachEngine3D
  Circumradius = 2.375
  FirstAngle = 0
  Height = 1.29
  Placement = pos=(0,10.325,-0.645) rot=(0,0,1;0rad)
  Polygon = 10
  SecondAngle = 0
FEATURE [Part::Prism] prism192
  AttacherType = Attacher::AttachEngine3D
  Circumradius = 2.375
  FirstAngle = 0
  Height = 1.29
  Placement = pos=(0,-10.325,-0.645) rot=(0,0,1;0rad)
  Polygon = 10
  SecondAngle = 0
FEATURE [Part::Box] cube092
  AttacherType = Attacher::AttachEngine3D
  Height = 1.29
  Length = 4.75
  Placement = pos=(-2.375,-10.325,-0.645) rot=(0,0,1;0rad)
  Width = 20.65
FEATURE [Part::MultiFuse] union091
  Placement = pos=(-171.45,-31.75,0) rot=(0,0,1;0rad)
  Shapes = -> [prism191,prism192,cube092]
FEATURE [Part::Prism] prism193
  AttacherType = Attacher::AttachEngine3D
  Circumradius = 2.375
  FirstAngle = 0
  Height = 1.29
  Placement = pos=(0,10.325,-0.645) rot=(0,0,1;0rad)
  Polygon = 10
  SecondAngle = 0
FEATURE [Part::Prism] prism194
  AttacherType = Attacher::AttachEngine3D
  Circumradius = 2.375
  FirstAngle = 0
  Height = 1.29
  Placement = pos=(0,-10.325,-0.645) rot=(0,0,1;0rad)
  Polygon = 10
  SecondAngle = 0
FEATURE [Part::Box] cube093
  AttacherType = Attacher::AttachEngine3D
  Height = 1.29
  Length = 4.75
  Placement = pos=(-2.375,-10.325,-0.645) rot=(0,0,1;0rad)
  Width = 20.65
FEATURE [Part::MultiFuse] union092
  Placement = pos=(-158.75,-31.75,0) rot=(0,0,1;0rad)
  Shapes = -> [prism193,prism194,cube093]
FEATURE [Part::Prism] prism195
  AttacherType = Attacher::AttachEngine3D
  Circumradius = 2.375
  FirstAngle = 0
  Height = 1.29
  Placement = pos=(0,10.325,-0.645) rot=(0,0,1;0rad)
  Polygon = 10
  SecondAngle = 0
FEATURE [Part::Prism] prism196
  AttacherType = Attacher::AttachEngine3D
  Circumradius = 2.375
  FirstAngle = 0
  Height = 1.29
  Placement = pos=(0,-10.325,-0.645) rot=(0,0,1;0rad)
  Polygon = 10
  SecondAngle = 0
FEATURE [Part::Box] cube094
  AttacherType = Attacher::AttachEngine3D
  Height = 1.29
  Length = 4.75
  Placement = pos=(-2.375,-10.325,-0.645) rot=(0,0,1;0rad)
  Width = 20.65
FEATURE [Part::MultiFuse] union093
  Placement = pos=(-146.05,-31.75,0) rot=(0,0,1;0rad)
  Shapes = -> [prism195,prism196,cube094]
FEATURE [Part::Prism] prism197
  AttacherType = Attacher::AttachEngine3D
  Circumradius = 2.375
  FirstAngle = 0
  Height = 1.29
  Placement = pos=(0,10.325,-0.645) rot=(0,0,1;0rad)
  Polygon = 10
  SecondAngle = 0
FEATURE [Part::Prism] prism198
  AttacherType = Attacher::AttachEngine3D
  Circumradius = 2.375
  FirstAngle = 0
  Height = 1.29
  Placement = pos=(0,-10.325,-0.645) rot=(0,0,1;0rad)
  Polygon = 10
  SecondAngle = 0
FEATURE [Part::Box] cube095
  AttacherType = Attacher::AttachEngine3D
  Height = 1.29
  Length = 4.75
  Placement = pos=(-2.375,-10.325,-0.645) rot=(0,0,1;0rad)
  Width = 20.65
FEATURE [Part::MultiFuse] union094
  Placement = pos=(-133.35,-31.75,0) rot=(0,0,1;0rad)
  Shapes = -> [prism197,prism198,cube095]
FEATURE [Part::Prism] prism199
  AttacherType = Attacher::AttachEngine3D
  Circumradius = 2.375
  FirstAngle = 0
  Height = 1.29
  Placement = pos=(0,10.325,-0.645) rot=(0,0,1;0rad)
  Polygon = 10
  SecondAngle = 0
FEATURE [Part::Prism] prism200
  AttacherType = Attacher::AttachEngine3D
  Circumradius = 2.375
  FirstAngle = 0
  Height = 1.29
  Placement = pos=(0,-10.325,-0.645) rot=(0,0,1;0rad)
  Polygon = 10
  SecondAngle = 0
FEATURE [Part::Box] cube096
  AttacherType = Attacher::AttachEngine3D
  Height = 1.29
  Length = 4.75
  Placement = pos=(-2.375,-10.325,-0.645) rot=(0,0,1;0rad)
  Width = 20.65
FEATURE [Part::MultiFuse] union095
  Placement = pos=(-120.65,-31.75,0) rot=(0,0,1;0rad)
  Shapes = -> [prism199,prism200,cube096]
FEATURE [Part::Prism] prism201
  AttacherType = Attacher::AttachEngine3D
  Circumradius = 2.375
  FirstAngle = 0
  Height = 1.29
  Placement = pos=(0,10.325,-0.645) rot=(0,0,1;0rad)
  Polygon = 10
  SecondAngle = 0
FEATURE [Part::Prism] prism202
  AttacherType = Attacher::AttachEngine3D
  Circumradius = 2.375
  FirstAngle = 0
  Height = 1.29
  Placement = pos=(0,-10.325,-0.645) rot=(0,0,1;0rad)
  Polygon = 10
  SecondAngle = 0
FEATURE [Part::Box] cube097
  AttacherType = Attacher::AttachEngine3D
  Height = 1.29
  Length = 4.75
  Placement = pos=(-2.375,-10.325,-0.645) rot=(0,0,1;0rad)
  Width = 20.65
FEATURE [Part::MultiFuse] union096
  Placement = pos=(-107.95,-31.75,0) rot=(0,0,1;0rad)
  Shapes = -> [prism201,prism202,cube097]
FEATURE [Part::Prism] prism203
  AttacherType = Attacher::AttachEngine3D
  Circumradius = 2.375
  FirstAngle = 0
  Height = 1.29
  Placement = pos=(0,10.325,-0.645) rot=(0,0,1;0rad)
  Polygon = 10
  SecondAngle = 0
FEATURE [Part::Prism] prism204
  AttacherType = Attacher::AttachEngine3D
  Circumradius = 2.375
  FirstAngle = 0
  Height = 1.29
  Placement = pos=(0,-10.325,-0.645) rot=(0,0,1;0rad)
  Polygon = 10
  SecondAngle = 0
FEATURE [Part::Box] cube098
  AttacherType = Attacher::AttachEngine3D
  Height = 1.29
  Length = 4.75
  Placement = pos=(-2.375,-10.325,-0.645) rot=(0,0,1;0rad)
  Width = 20.65
FEATURE [Part::MultiFuse] union097
  Placement = pos=(-95.25,-31.75,0) rot=(0,0,1;0rad)
  Shapes = -> [prism203,prism204,cube098]
FEATURE [Part::Prism] prism205
  AttacherType = Attacher::AttachEngine3D
  Circumradius = 2.375
  FirstAngle = 0
  Height = 1.29
  Placement = pos=(0,10.325,-0.645) rot=(0,0,1;0rad)
  Polygon = 10
  SecondAngle = 0
FEATURE [Part::Prism] prism206
  AttacherType = Attacher::AttachEngine3D
  Circumradius = 2.375
  FirstAngle = 0
  Height = 1.29
  Placement = pos=(0,-10.325,-0.645) rot=(0,0,1;0rad)
  Polygon = 10
  SecondAngle = 0
FEATURE [Part::Box] cube099
  AttacherType = Attacher::AttachEngine3D
  Height = 1.29
  Length = 4.75
  Placement = pos=(-2.375,-10.325,-0.645) rot=(0,0,1;0rad)
  Width = 20.65
FEATURE [Part::MultiFuse] union098
  Placement = pos=(-82.55,-31.75,0) rot=(0,0,1;0rad)
  Shapes = -> [prism205,prism206,cube099]
FEATURE [Part::Prism] prism207
  AttacherType = Attacher::AttachEngine3D
  Circumradius = 2.375
  FirstAngle = 0
  Height = 1.29
  Placement = pos=(0,10.325,-0.645) rot=(0,0,1;0rad)
  Polygon = 10
  SecondAngle = 0
FEATURE [Part::Prism] prism208
  AttacherType = Attacher::AttachEngine3D
  Circumradius = 2.375
  FirstAngle = 0
  Height = 1.29
  Placement = pos=(0,-10.325,-0.645) rot=(0,0,1;0rad)
  Polygon = 10
  SecondAngle = 0
FEATURE [Part::Box] cube100
  AttacherType = Attacher::AttachEngine3D
  Height = 1.29
  Length = 4.75
  Placement = pos=(-2.375,-10.325,-0.645) rot=(0,0,1;0rad)
  Width = 20.65
FEATURE [Part::MultiFuse] union099
  Placement = pos=(-69.85,-31.75,0) rot=(0,0,1;0rad)
  Shapes = -> [prism207,prism208,cube100]
FEATURE [Part::Prism] prism209
  AttacherType = Attacher::AttachEngine3D
  Circumradius = 2.375
  FirstAngle = 0
  Height = 1.29
  Placement = pos=(0,10.325,-0.645) rot=(0,0,1;0rad)
  Polygon = 10
  SecondAngle = 0
FEATURE [Part::Prism] prism210
  AttacherType = Attacher::AttachEngine3D
  Circumradius = 2.375
  FirstAngle = 0
  Height = 1.29
  Placement = pos=(0,-10.325,-0.645) rot=(0,0,1;0rad)
  Polygon = 10
  SecondAngle = 0
FEATURE [Part::Box] cube101
  AttacherType = Attacher::AttachEngine3D
  Height = 1.29
  Length = 4.75
  Placement = pos=(-2.375,-10.325,-0.645) rot=(0,0,1;0rad)
  Width = 20.65
FEATURE [Part::MultiFuse] union100
  Placement = pos=(-57.15,-31.75,0) rot=(0,0,1;0rad)
  Shapes = -> [prism209,prism210,cube101]
FEATURE [Part::Prism] prism211
  AttacherType = Attacher::AttachEngine3D
  Circumradius = 2.375
  FirstAngle = 0
  Height = 1.29
  Placement = pos=(0,10.325,-0.645) rot=(0,0,1;0rad)
  Polygon = 10
  SecondAngle = 0
FEATURE [Part::Prism] prism212
  AttacherType = Attacher::AttachEngine3D
  Circumradius = 2.375
  FirstAngle = 0
  Height = 1.29
  Placement = pos=(0,-10.325,-0.645) rot=(0,0,1;0rad)
  Polygon = 10
  SecondAngle = 0
FEATURE [Part::Box] cube102
  AttacherType = Attacher::AttachEngine3D
  Height = 1.29
  Length = 4.75
  Placement = pos=(-2.375,-10.325,-0.645) rot=(0,0,1;0rad)
  Width = 20.65
FEATURE [Part::MultiFuse] union101
  Placement = pos=(-44.45,-31.75,0) rot=(0,0,1;0rad)
  Shapes = -> [prism211,prism212,cube102]
FEATURE [Part::Prism] prism213
  AttacherType = Attacher::AttachEngine3D
  Circumradius = 2.375
  FirstAngle = 0
  Height = 1.29
  Placement = pos=(0,10.325,-0.645) rot=(0,0,1;0rad)
  Polygon = 10
  SecondAngle = 0
FEATURE [Part::Prism] prism214
  AttacherType = Attacher::AttachEngine3D
  Circumradius = 2.375
  FirstAngle = 0
  Height = 1.29
  Placement = pos=(0,-10.325,-0.645) rot=(0,0,1;0rad)
  Polygon = 10
  SecondAngle = 0
FEATURE [Part::Box] cube103
  AttacherType = Attacher::AttachEngine3D
  Height = 1.29
  Length = 4.75
  Placement = pos=(-2.375,-10.325,-0.645) rot=(0,0,1;0rad)
  Width = 20.65
FEATURE [Part::MultiFuse] union102
  Placement = pos=(-31.75,-31.75,0) rot=(0,0,1;0rad)
  Shapes = -> [prism213,prism214,cube103]
FEATURE [Part::Prism] prism215
  AttacherType = Attacher::AttachEngine3D
  Circumradius = 2.375
  FirstAngle = 0
  Height = 1.29
  Placement = pos=(0,10.325,-0.645) rot=(0,0,1;0rad)
  Polygon = 10
  SecondAngle = 0
FEATURE [Part::Prism] prism216
  AttacherType = Attacher::AttachEngine3D
  Circumradius = 2.375
  FirstAngle = 0
  Height = 1.29
  Placement = pos=(0,-10.325,-0.645) rot=(0,0,1;0rad)
  Polygon = 10
  SecondAngle = 0
FEATURE [Part::Box] cube104
  AttacherType = Attacher::AttachEngine3D
  Height = 1.29
  Length = 4.75
  Placement = pos=(-2.375,-10.325,-0.645) rot=(0,0,1;0rad)
  Width = 20.65
FEATURE [Part::MultiFuse] union103
  Placement = pos=(-19.05,-31.75,0) rot=(0,0,1;0rad)
  Shapes = -> [prism215,prism216,cube104]
FEATURE [Part::Prism] prism217
  AttacherType = Attacher::AttachEngine3D
  Circumradius = 2.375
  FirstAngle = 0
  Height = 1.29
  Placement = pos=(0,10.325,-0.645) rot=(0,0,1;0rad)
  Polygon = 10
  SecondAngle = 0
FEATURE [Part::Prism] prism218
  AttacherType = Attacher::AttachEngine3D
  Circumradius = 2.375
  FirstAngle = 0
  Height = 1.29
  Placement = pos=(0,-10.325,-0.645) rot=(0,0,1;0rad)
  Polygon = 10
  SecondAngle = 0
FEATURE [Part::Box] cube105
  AttacherType = Attacher::AttachEngine3D
  Height = 1.29
  Length = 4.75
  Placement = pos=(-2.375,-10.325,-0.645) rot=(0,0,1;0rad)
  Width = 20.65
FEATURE [Part::MultiFuse] union104
  Placement = pos=(-6.35,-31.75,0) rot=(0,0,1;0rad)
  Shapes = -> [prism217,prism218,cube105]
FEATURE [Part::Prism] prism219
  AttacherType = Attacher::AttachEngine3D
  Circumradius = 2.375
  FirstAngle = 0
  Height = 1.29
  Placement = pos=(0,10.325,-0.645) rot=(0,0,1;0rad)
  Polygon = 10
  SecondAngle = 0
FEATURE [Part::Prism] prism220
  AttacherType = Attacher::AttachEngine3D
  Circumradius = 2.375
  FirstAngle = 0
  Height = 1.29
  Placement = pos=(0,-10.325,-0.645) rot=(0,0,1;0rad)
  Polygon = 10
  SecondAngle = 0
FEATURE [Part::Box] cube106
  AttacherType = Attacher::AttachEngine3D
  Height = 1.29
  Length = 4.75
  Placement = pos=(-2.375,-10.325,-0.645) rot=(0,0,1;0rad)
  Width = 20.65
FEATURE [Part::MultiFuse] union105
  Placement = pos=(6.35,-31.75,0) rot=(0,0,1;0rad)
  Shapes = -> [prism219,prism220,cube106]
FEATURE [Part::Prism] prism221
  AttacherType = Attacher::AttachEngine3D
  Circumradius = 2.375
  FirstAngle = 0
  Height = 1.29
  Placement = pos=(0,10.325,-0.645) rot=(0,0,1;0rad)
  Polygon = 10
  SecondAngle = 0
FEATURE [Part::Prism] prism222
  AttacherType = Attacher::AttachEngine3D
  Circumradius = 2.375
  FirstAngle = 0
  Height = 1.29
  Placement = pos=(0,-10.325,-0.645) rot=(0,0,1;0rad)
  Polygon = 10
  SecondAngle = 0
FEATURE [Part::Box] cube107
  AttacherType = Attacher::AttachEngine3D
  Height = 1.29
  Length = 4.75
  Placement = pos=(-2.375,-10.325,-0.645) rot=(0,0,1;0rad)
  Width = 20.65
FEATURE [Part::MultiFuse] union106
  Placement = pos=(19.05,-31.75,0) rot=(0,0,1;0rad)
  Shapes = -> [prism221,prism222,cube107]
FEATURE [Part::Prism] prism223
  AttacherType = Attacher::AttachEngine3D
  Circumradius = 2.375
  FirstAngle = 0
  Height = 1.29
  Placement = pos=(0,10.325,-0.645) rot=(0,0,1;0rad)
  Polygon = 10
  SecondAngle = 0
FEATURE [Part::Prism] prism224
  AttacherType = Attacher::AttachEngine3D
  Circumradius = 2.375
  FirstAngle = 0
  Height = 1.29
  Placement = pos=(0,-10.325,-0.645) rot=(0,0,1;0rad)
  Polygon = 10
  SecondAngle = 0
FEATURE [Part::Box] cube108
  AttacherType = Attacher::AttachEngine3D
  Height = 1.29
  Length = 4.75
  Placement = pos=(-2.375,-10.325,-0.645) rot=(0,0,1;0rad)
  Width = 20.65
FEATURE [Part::MultiFuse] union107
  Placement = pos=(31.75,-31.75,0) rot=(0,0,1;0rad)
  Shapes = -> [prism223,prism224,cube108]
FEATURE [Part::Prism] prism225
  AttacherType = Attacher::AttachEngine3D
  Circumradius = 2.375
  FirstAngle = 0
  Height = 1.29
  Placement = pos=(0,10.325,-0.645) rot=(0,0,1;0rad)
  Polygon = 10
  SecondAngle = 0
FEATURE [Part::Prism] prism226
  AttacherType = Attacher::AttachEngine3D
  Circumradius = 2.375
  FirstAngle = 0
  Height = 1.29
  Placement = pos=(0,-10.325,-0.645) rot=(0,0,1;0rad)
  Polygon = 10
  SecondAngle = 0
FEATURE [Part::Box] cube109
  AttacherType = Attacher::AttachEngine3D
  Height = 1.29
  Length = 4.75
  Placement = pos=(-2.375,-10.325,-0.645) rot=(0,0,1;0rad)
  Width = 20.65
FEATURE [Part::MultiFuse] union108
  Placement = pos=(44.45,-31.75,0) rot=(0,0,1;0rad)
  Shapes = -> [prism225,prism226,cube109]
FEATURE [Part::Prism] prism227
  AttacherType = Attacher::AttachEngine3D
  Circumradius = 2.375
  FirstAngle = 0
  Height = 1.29
  Placement = pos=(0,10.325,-0.645) rot=(0,0,1;0rad)
  Polygon = 10
  SecondAngle = 0
FEATURE [Part::Prism] prism228
  AttacherType = Attacher::AttachEngine3D
  Circumradius = 2.375
  FirstAngle = 0
  Height = 1.29
  Placement = pos=(0,-10.325,-0.645) rot=(0,0,1;0rad)
  Polygon = 10
  SecondAngle = 0
FEATURE [Part::Box] cube110
  AttacherType = Attacher::AttachEngine3D
  Height = 1.29
  Length = 4.75
  Placement = pos=(-2.375,-10.325,-0.645) rot=(0,0,1;0rad)
  Width = 20.65
FEATURE [Part::MultiFuse] union109
  Placement = pos=(57.15,-31.75,0) rot=(0,0,1;0rad)
  Shapes = -> [prism227,prism228,cube110]
FEATURE [Part::Prism] prism229
  AttacherType = Attacher::AttachEngine3D
  Circumradius = 2.375
  FirstAngle = 0
  Height = 1.29
  Placement = pos=(0,10.325,-0.645) rot=(0,0,1;0rad)
  Polygon = 10
  SecondAngle = 0
FEATURE [Part::Prism] prism230
  AttacherType = Attacher::AttachEngine3D
  Circumradius = 2.375
  FirstAngle = 0
  Height = 1.29
  Placement = pos=(0,-10.325,-0.645) rot=(0,0,1;0rad)
  Polygon = 10
  SecondAngle = 0
FEATURE [Part::Box] cube111
  AttacherType = Attacher::AttachEngine3D
  Height = 1.29
  Length = 4.75
  Placement = pos=(-2.375,-10.325,-0.645) rot=(0,0,1;0rad)
  Width = 20.65
FEATURE [Part::MultiFuse] union110
  Placement = pos=(69.85,-31.75,0) rot=(0,0,1;0rad)
  Shapes = -> [prism229,prism230,cube111]
FEATURE [Part::Prism] prism231
  AttacherType = Attacher::AttachEngine3D
  Circumradius = 2.375
  FirstAngle = 0
  Height = 1.29
  Placement = pos=(0,10.325,-0.645) rot=(0,0,1;0rad)
  Polygon = 10
  SecondAngle = 0
FEATURE [Part::Prism] prism232
  AttacherType = Attacher::AttachEngine3D
  Circumradius = 2.375
  FirstAngle = 0
  Height = 1.29
  Placement = pos=(0,-10.325,-0.645) rot=(0,0,1;0rad)
  Polygon = 10
  SecondAngle = 0
FEATURE [Part::Box] cube112
  AttacherType = Attacher::AttachEngine3D
  Height = 1.29
  Length = 4.75
  Placement = pos=(-2.375,-10.325,-0.645) rot=(0,0,1;0rad)
  Width = 20.65
FEATURE [Part::MultiFuse] union111
  Placement = pos=(82.55,-31.75,0) rot=(0,0,1;0rad)
  Shapes = -> [prism231,prism232,cube112]
FEATURE [Part::Prism] prism233
  AttacherType = Attacher::AttachEngine3D
  Circumradius = 2.375
  FirstAngle = 0
  Height = 1.29
  Placement = pos=(0,10.325,-0.645) rot=(0,0,1;0rad)
  Polygon = 10
  SecondAngle = 0
FEATURE [Part::Prism] prism234
  AttacherType = Attacher::AttachEngine3D
  Circumradius = 2.375
  FirstAngle = 0
  Height = 1.29
  Placement = pos=(0,-10.325,-0.645) rot=(0,0,1;0rad)
  Polygon = 10
  SecondAngle = 0
FEATURE [Part::Box] cube113
  AttacherType = Attacher::AttachEngine3D
  Height = 1.29
  Length = 4.75
  Placement = pos=(-2.375,-10.325,-0.645) rot=(0,0,1;0rad)
  Width = 20.65
FEATURE [Part::MultiFuse] union112
  Placement = pos=(95.25,-31.75,0) rot=(0,0,1;0rad)
  Shapes = -> [prism233,prism234,cube113]
FEATURE [Part::Prism] prism235
  AttacherType = Attacher::AttachEngine3D
  Circumradius = 2.375
  FirstAngle = 0
  Height = 1.29
  Placement = pos=(0,10.325,-0.645) rot=(0,0,1;0rad)
  Polygon = 10
  SecondAngle = 0
FEATURE [Part::Prism] prism236
  AttacherType = Attacher::AttachEngine3D
  Circumradius = 2.375
  FirstAngle = 0
  Height = 1.29
  Placement = pos=(0,-10.325,-0.645) rot=(0,0,1;0rad)
  Polygon = 10
  SecondAngle = 0
FEATURE [Part::Box] cube114
  AttacherType = Attacher::AttachEngine3D
  Height = 1.29
  Length = 4.75
  Placement = pos=(-2.375,-10.325,-0.645) rot=(0,0,1;0rad)
  Width = 20.65
FEATURE [Part::MultiFuse] union113
  Placement = pos=(107.95,-31.75,0) rot=(0,0,1;0rad)
  Shapes = -> [prism235,prism236,cube114]
FEATURE [Part::Prism] prism237
  AttacherType = Attacher::AttachEngine3D
  Circumradius = 2.375
  FirstAngle = 0
  Height = 1.29
  Placement = pos=(0,10.325,-0.645) rot=(0,0,1;0rad)
  Polygon = 10
  SecondAngle = 0
FEATURE [Part::Prism] prism238
  AttacherType = Attacher::AttachEngine3D
  Circumradius = 2.375
  FirstAngle = 0
  Height = 1.29
  Placement = pos=(0,-10.325,-0.645) rot=(0,0,1;0rad)
  Polygon = 10
  SecondAngle = 0
FEATURE [Part::Box] cube115
  AttacherType = Attacher::AttachEngine3D
  Height = 1.29
  Length = 4.75
  Placement = pos=(-2.375,-10.325,-0.645) rot=(0,0,1;0rad)
  Width = 20.65
FEATURE [Part::MultiFuse] union114
  Placement = pos=(120.65,-31.75,0) rot=(0,0,1;0rad)
  Shapes = -> [prism237,prism238,cube115]
FEATURE [Part::Prism] prism239
  AttacherType = Attacher::AttachEngine3D
  Circumradius = 2.375
  FirstAngle = 0
  Height = 1.29
  Placement = pos=(0,10.325,-0.645) rot=(0,0,1;0rad)
  Polygon = 10
  SecondAngle = 0
FEATURE [Part::Prism] prism240
  AttacherType = Attacher::AttachEngine3D
  Circumradius = 2.375
  FirstAngle = 0
  Height = 1.29
  Placement = pos=(0,-10.325,-0.645) rot=(0,0,1;0rad)
  Polygon = 10
  SecondAngle = 0
FEATURE [Part::Box] cube116
  AttacherType = Attacher::AttachEngine3D
  Height = 1.29
  Length = 4.75
  Placement = pos=(-2.375,-10.325,-0.645) rot=(0,0,1;0rad)
  Width = 20.65
FEATURE [Part::MultiFuse] union115
  Placement = pos=(133.35,-31.75,0) rot=(0,0,1;0rad)
  Shapes = -> [prism239,prism240,cube116]
FEATURE [Part::Prism] prism241
  AttacherType = Attacher::AttachEngine3D
  Circumradius = 2.375
  FirstAngle = 0
  Height = 1.29
  Placement = pos=(0,10.325,-0.645) rot=(0,0,1;0rad)
  Polygon = 10
  SecondAngle = 0
FEATURE [Part::Prism] prism242
  AttacherType = Attacher::AttachEngine3D
  Circumradius = 2.375
  FirstAngle = 0
  Height = 1.29
  Placement = pos=(0,-10.325,-0.645) rot=(0,0,1;0rad)
  Polygon = 10
  SecondAngle = 0
FEATURE [Part::Box] cube117
  AttacherType = Attacher::AttachEngine3D
  Height = 1.29
  Length = 4.75
  Placement = pos=(-2.375,-10.325,-0.645) rot=(0,0,1;0rad)
  Width = 20.65
FEATURE [Part::MultiFuse] union116
  Placement = pos=(146.05,-31.75,0) rot=(0,0,1;0rad)
  Shapes = -> [prism241,prism242,cube117]
FEATURE [Part::Prism] prism243
  AttacherType = Attacher::AttachEngine3D
  Circumradius = 2.375
  FirstAngle = 0
  Height = 1.29
  Placement = pos=(0,10.325,-0.645) rot=(0,0,1;0rad)
  Polygon = 10
  SecondAngle = 0
FEATURE [Part::Prism] prism244
  AttacherType = Attacher::AttachEngine3D
  Circumradius = 2.375
  FirstAngle = 0
  Height = 1.29
  Placement = pos=(0,-10.325,-0.645) rot=(0,0,1;0rad)
  Polygon = 10
  SecondAngle = 0
FEATURE [Part::Box] cube118
  AttacherType = Attacher::AttachEngine3D
  Height = 1.29
  Length = 4.75
  Placement = pos=(-2.375,-10.325,-0.645) rot=(0,0,1;0rad)
  Width = 20.65
FEATURE [Part::MultiFuse] union117
  Placement = pos=(158.75,-31.75,0) rot=(0,0,1;0rad)
  Shapes = -> [prism243,prism244,cube118]
FEATURE [Part::Prism] prism245
  AttacherType = Attacher::AttachEngine3D
  Circumradius = 2.375
  FirstAngle = 0
  Height = 1.29
  Placement = pos=(0,10.325,-0.645) rot=(0,0,1;0rad)
  Polygon = 10
  SecondAngle = 0
FEATURE [Part::Prism] prism246
  AttacherType = Attacher::AttachEngine3D
  Circumradius = 2.375
  FirstAngle = 0
  Height = 1.29
  Placement = pos=(0,-10.325,-0.645) rot=(0,0,1;0rad)
  Polygon = 10
  SecondAngle = 0
FEATURE [Part::Box] cube119
  AttacherType = Attacher::AttachEngine3D
  Height = 1.29
  Length = 4.75
  Placement = pos=(-2.375,-10.325,-0.645) rot=(0,0,1;0rad)
  Width = 20.65
FEATURE [Part::MultiFuse] union118
  Placement = pos=(171.45,-31.75,0) rot=(0,0,1;0rad)
  Shapes = -> [prism245,prism246,cube119]
FEATURE [Part::Prism] prism247
  AttacherType = Attacher::AttachEngine3D
  Circumradius = 2.375
  FirstAngle = 0
  Height = 1.29
  Placement = pos=(0,10.325,-0.645) rot=(0,0,1;0rad)
  Polygon = 10
  SecondAngle = 0
FEATURE [Part::Prism] prism248
  AttacherType = Attacher::AttachEngine3D
  Circumradius = 2.375
  FirstAngle = 0
  Height = 1.29
  Placement = pos=(0,-10.325,-0.645) rot=(0,0,1;0rad)
  Polygon = 10
  SecondAngle = 0
FEATURE [Part::Box] cube120
  AttacherType = Attacher::AttachEngine3D
  Height = 1.29
  Length = 4.75
  Placement = pos=(-2.375,-10.325,-0.645) rot=(0,0,1;0rad)
  Width = 20.65
FEATURE [Part::MultiFuse] union119
  Placement = pos=(184.15,-31.75,0) rot=(0,0,1;0rad)
  Shapes = -> [prism247,prism248,cube120]
FEATURE [Part::MultiFuse] Group003
  Shapes = -> [union090,union091,union092,union093,union094,union095,union096,union097,union098,union099,union100,union101,union102,union103,union104,union105,union106,union107,union108,union109,union110,union111,union112,union113,union114,union115,union116,union117,union118,union119]
FEATURE [Part::Prism] prism249
  AttacherType = Attacher::AttachEngine3D
  Circumradius = 2.375
  FirstAngle = 0
  Height = 1.29
  Placement = pos=(0,10.325,-0.645) rot=(0,0,1;0rad)
  Polygon = 10
  SecondAngle = 0
FEATURE [Part::Prism] prism250
  AttacherType = Attacher::AttachEngine3D
  Circumradius = 2.375
  FirstAngle = 0
  Height = 1.29
  Placement = pos=(0,-10.325,-0.645) rot=(0,0,1;0rad)
  Polygon = 10
  SecondAngle = 0
FEATURE [Part::Box] cube121
  AttacherType = Attacher::AttachEngine3D
  Height = 1.29
  Length = 4.75
  Placement = pos=(-2.375,-10.325,-0.645) rot=(0,0,1;0rad)
  Width = 20.65
FEATURE [Part::MultiFuse] union120
  Placement = pos=(-184.15,-63.5,0) rot=(0,0,1;0rad)
  Shapes = -> [prism249,prism250,cube121]
FEATURE [Part::Prism] prism251
  AttacherType = Attacher::AttachEngine3D
  Circumradius = 2.375
  FirstAngle = 0
  Height = 1.29
  Placement = pos=(0,10.325,-0.645) rot=(0,0,1;0rad)
  Polygon = 10
  SecondAngle = 0
FEATURE [Part::Prism] prism252
  AttacherType = Attacher::AttachEngine3D
  Circumradius = 2.375
  FirstAngle = 0
  Height = 1.29
  Placement = pos=(0,-10.325,-0.645) rot=(0,0,1;0rad)
  Polygon = 10
  SecondAngle = 0
FEATURE [Part::Box] cube122
  AttacherType = Attacher::AttachEngine3D
  Height = 1.29
  Length = 4.75
  Placement = pos=(-2.375,-10.325,-0.645) rot=(0,0,1;0rad)
  Width = 20.65
FEATURE [Part::MultiFuse] union121
  Placement = pos=(-171.45,-63.5,0) rot=(0,0,1;0rad)
  Shapes = -> [prism251,prism252,cube122]
FEATURE [Part::Prism] prism253
  AttacherType = Attacher::AttachEngine3D
  Circumradius = 2.375
  FirstAngle = 0
  Height = 1.29
  Placement = pos=(0,10.325,-0.645) rot=(0,0,1;0rad)
  Polygon = 10
  SecondAngle = 0
FEATURE [Part::Prism] prism254
  AttacherType = Attacher::AttachEngine3D
  Circumradius = 2.375
  FirstAngle = 0
  Height = 1.29
  Placement = pos=(0,-10.325,-0.645) rot=(0,0,1;0rad)
  Polygon = 10
  SecondAngle = 0
FEATURE [Part::Box] cube123
  AttacherType = Attacher::AttachEngine3D
  Height = 1.29
  Length = 4.75
  Placement = pos=(-2.375,-10.325,-0.645) rot=(0,0,1;0rad)
  Width = 20.65
FEATURE [Part::MultiFuse] union122
  Placement = pos=(-158.75,-63.5,0) rot=(0,0,1;0rad)
  Shapes = -> [prism253,prism254,cube123]
FEATURE [Part::Prism] prism255
  AttacherType = Attacher::AttachEngine3D
  Circumradius = 2.375
  FirstAngle = 0
  Height = 1.29
  Placement = pos=(0,10.325,-0.645) rot=(0,0,1;0rad)
  Polygon = 10
  SecondAngle = 0
FEATURE [Part::Prism] prism256
  AttacherType = Attacher::AttachEngine3D
  Circumradius = 2.375
  FirstAngle = 0
  Height = 1.29
  Placement = pos=(0,-10.325,-0.645) rot=(0,0,1;0rad)
  Polygon = 10
  SecondAngle = 0
FEATURE [Part::Box] cube124
  AttacherType = Attacher::AttachEngine3D
  Height = 1.29
  Length = 4.75
  Placement = pos=(-2.375,-10.325,-0.645) rot=(0,0,1;0rad)
  Width = 20.65
FEATURE [Part::MultiFuse] union123
  Placement = pos=(-146.05,-63.5,0) rot=(0,0,1;0rad)
  Shapes = -> [prism255,prism256,cube124]
FEATURE [Part::Prism] prism257
  AttacherType = Attacher::AttachEngine3D
  Circumradius = 2.375
  FirstAngle = 0
  Height = 1.29
  Placement = pos=(0,10.325,-0.645) rot=(0,0,1;0rad)
  Polygon = 10
  SecondAngle = 0
FEATURE [Part::Prism] prism258
  AttacherType = Attacher::AttachEngine3D
  Circumradius = 2.375
  FirstAngle = 0
  Height = 1.29
  Placement = pos=(0,-10.325,-0.645) rot=(0,0,1;0rad)
  Polygon = 10
  SecondAngle = 0
FEATURE [Part::Box] cube125
  AttacherType = Attacher::AttachEngine3D
  Height = 1.29
  Length = 4.75
  Placement = pos=(-2.375,-10.325,-0.645) rot=(0,0,1;0rad)
  Width = 20.65
FEATURE [Part::MultiFuse] union124
  Placement = pos=(-133.35,-63.5,0) rot=(0,0,1;0rad)
  Shapes = -> [prism257,prism258,cube125]
FEATURE [Part::Prism] prism259
  AttacherType = Attacher::AttachEngine3D
  Circumradius = 2.375
  FirstAngle = 0
  Height = 1.29
  Placement = pos=(0,10.325,-0.645) rot=(0,0,1;0rad)
  Polygon = 10
  SecondAngle = 0
FEATURE [Part::Prism] prism260
  AttacherType = Attacher::AttachEngine3D
  Circumradius = 2.375
  FirstAngle = 0
  Height = 1.29
  Placement = pos=(0,-10.325,-0.645) rot=(0,0,1;0rad)
  Polygon = 10
  SecondAngle = 0
FEATURE [Part::Box] cube126
  AttacherType = Attacher::AttachEngine3D
  Height = 1.29
  Length = 4.75
  Placement = pos=(-2.375,-10.325,-0.645) rot=(0,0,1;0rad)
  Width = 20.65
FEATURE [Part::MultiFuse] union125
  Placement = pos=(-120.65,-63.5,0) rot=(0,0,1;0rad)
  Shapes = -> [prism259,prism260,cube126]
FEATURE [Part::Prism] prism261
  AttacherType = Attacher::AttachEngine3D
  Circumradius = 2.375
  FirstAngle = 0
  Height = 1.29
  Placement = pos=(0,10.325,-0.645) rot=(0,0,1;0rad)
  Polygon = 10
  SecondAngle = 0
FEATURE [Part::Prism] prism262
  AttacherType = Attacher::AttachEngine3D
  Circumradius = 2.375
  FirstAngle = 0
  Height = 1.29
  Placement = pos=(0,-10.325,-0.645) rot=(0,0,1;0rad)
  Polygon = 10
  SecondAngle = 0
FEATURE [Part::Box] cube127
  AttacherType = Attacher::AttachEngine3D
  Height = 1.29
  Length = 4.75
  Placement = pos=(-2.375,-10.325,-0.645) rot=(0,0,1;0rad)
  Width = 20.65
FEATURE [Part::MultiFuse] union126
  Placement = pos=(-107.95,-63.5,0) rot=(0,0,1;0rad)
  Shapes = -> [prism261,prism262,cube127]
FEATURE [Part::Prism] prism263
  AttacherType = Attacher::AttachEngine3D
  Circumradius = 2.375
  FirstAngle = 0
  Height = 1.29
  Placement = pos=(0,10.325,-0.645) rot=(0,0,1;0rad)
  Polygon = 10
  SecondAngle = 0
FEATURE [Part::Prism] prism264
  AttacherType = Attacher::AttachEngine3D
  Circumradius = 2.375
  FirstAngle = 0
  Height = 1.29
  Placement = pos=(0,-10.325,-0.645) rot=(0,0,1;0rad)
  Polygon = 10
  SecondAngle = 0
FEATURE [Part::Box] cube128
  AttacherType = Attacher::AttachEngine3D
  Height = 1.29
  Length = 4.75
  Placement = pos=(-2.375,-10.325,-0.645) rot=(0,0,1;0rad)
  Width = 20.65
FEATURE [Part::MultiFuse] union127
  Placement = pos=(-95.25,-63.5,0) rot=(0,0,1;0rad)
  Shapes = -> [prism263,prism264,cube128]
FEATURE [Part::Prism] prism265
  AttacherType = Attacher::AttachEngine3D
  Circumradius = 2.375
  FirstAngle = 0
  Height = 1.29
  Placement = pos=(0,10.325,-0.645) rot=(0,0,1;0rad)
  Polygon = 10
  SecondAngle = 0
FEATURE [Part::Prism] prism266
  AttacherType = Attacher::AttachEngine3D
  Circumradius = 2.375
  FirstAngle = 0
  Height = 1.29
  Placement = pos=(0,-10.325,-0.645) rot=(0,0,1;0rad)
  Polygon = 10
  SecondAngle = 0
FEATURE [Part::Box] cube129
  AttacherType = Attacher::AttachEngine3D
  Height = 1.29
  Length = 4.75
  Placement = pos=(-2.375,-10.325,-0.645) rot=(0,0,1;0rad)
  Width = 20.65
FEATURE [Part::MultiFuse] union128
  Placement = pos=(-82.55,-63.5,0) rot=(0,0,1;0rad)
  Shapes = -> [prism265,prism266,cube129]
FEATURE [Part::Prism] prism267
  AttacherType = Attacher::AttachEngine3D
  Circumradius = 2.375
  FirstAngle = 0
  Height = 1.29
  Placement = pos=(0,10.325,-0.645) rot=(0,0,1;0rad)
  Polygon = 10
  SecondAngle = 0
FEATURE [Part::Prism] prism268
  AttacherType = Attacher::AttachEngine3D
  Circumradius = 2.375
  FirstAngle = 0
  Height = 1.29
  Placement = pos=(0,-10.325,-0.645) rot=(0,0,1;0rad)
  Polygon = 10
  SecondAngle = 0
FEATURE [Part::Box] cube130
  AttacherType = Attacher::AttachEngine3D
  Height = 1.29
  Length = 4.75
  Placement = pos=(-2.375,-10.325,-0.645) rot=(0,0,1;0rad)
  Width = 20.65
FEATURE [Part::MultiFuse] union129
  Placement = pos=(-69.85,-63.5,0) rot=(0,0,1;0rad)
  Shapes = -> [prism267,prism268,cube130]
FEATURE [Part::Prism] prism269
  AttacherType = Attacher::AttachEngine3D
  Circumradius = 2.375
  FirstAngle = 0
  Height = 1.29
  Placement = pos=(0,10.325,-0.645) rot=(0,0,1;0rad)
  Polygon = 10
  SecondAngle = 0
FEATURE [Part::Prism] prism270
  AttacherType = Attacher::AttachEngine3D
  Circumradius = 2.375
  FirstAngle = 0
  Height = 1.29
  Placement = pos=(0,-10.325,-0.645) rot=(0,0,1;0rad)
  Polygon = 10
  SecondAngle = 0
FEATURE [Part::Box] cube131
  AttacherType = Attacher::AttachEngine3D
  Height = 1.29
  Length = 4.75
  Placement = pos=(-2.375,-10.325,-0.645) rot=(0,0,1;0rad)
  Width = 20.65
FEATURE [Part::MultiFuse] union130
  Placement = pos=(-57.15,-63.5,0) rot=(0,0,1;0rad)
  Shapes = -> [prism269,prism270,cube131]
FEATURE [Part::Prism] prism271
  AttacherType = Attacher::AttachEngine3D
  Circumradius = 2.375
  FirstAngle = 0
  Height = 1.29
  Placement = pos=(0,10.325,-0.645) rot=(0,0,1;0rad)
  Polygon = 10
  SecondAngle = 0
FEATURE [Part::Prism] prism272
  AttacherType = Attacher::AttachEngine3D
  Circumradius = 2.375
  FirstAngle = 0
  Height = 1.29
  Placement = pos=(0,-10.325,-0.645) rot=(0,0,1;0rad)
  Polygon = 10
  SecondAngle = 0
FEATURE [Part::Box] cube132
  AttacherType = Attacher::AttachEngine3D
  Height = 1.29
  Length = 4.75
  Placement = pos=(-2.375,-10.325,-0.645) rot=(0,0,1;0rad)
  Width = 20.65
FEATURE [Part::MultiFuse] union131
  Placement = pos=(-44.45,-63.5,0) rot=(0,0,1;0rad)
  Shapes = -> [prism271,prism272,cube132]
FEATURE [Part::Prism] prism273
  AttacherType = Attacher::AttachEngine3D
  Circumradius = 2.375
  FirstAngle = 0
  Height = 1.29
  Placement = pos=(0,10.325,-0.645) rot=(0,0,1;0rad)
  Polygon = 10
  SecondAngle = 0
FEATURE [Part::Prism] prism274
  AttacherType = Attacher::AttachEngine3D
  Circumradius = 2.375
  FirstAngle = 0
  Height = 1.29
  Placement = pos=(0,-10.325,-0.645) rot=(0,0,1;0rad)
  Polygon = 10
  SecondAngle = 0
FEATURE [Part::Box] cube133
  AttacherType = Attacher::AttachEngine3D
  Height = 1.29
  Length = 4.75
  Placement = pos=(-2.375,-10.325,-0.645) rot=(0,0,1;0rad)
  Width = 20.65
FEATURE [Part::MultiFuse] union132
  Placement = pos=(-31.75,-63.5,0) rot=(0,0,1;0rad)
  Shapes = -> [prism273,prism274,cube133]
FEATURE [Part::Prism] prism275
  AttacherType = Attacher::AttachEngine3D
  Circumradius = 2.375
  FirstAngle = 0
  Height = 1.29
  Placement = pos=(0,10.325,-0.645) rot=(0,0,1;0rad)
  Polygon = 10
  SecondAngle = 0
FEATURE [Part::Prism] prism276
  AttacherType = Attacher::AttachEngine3D
  Circumradius = 2.375
  FirstAngle = 0
  Height = 1.29
  Placement = pos=(0,-10.325,-0.645) rot=(0,0,1;0rad)
  Polygon = 10
  SecondAngle = 0
FEATURE [Part::Box] cube134
  AttacherType = Attacher::AttachEngine3D
  Height = 1.29
  Length = 4.75
  Placement = pos=(-2.375,-10.325,-0.645) rot=(0,0,1;0rad)
  Width = 20.65
FEATURE [Part::MultiFuse] union133
  Placement = pos=(-19.05,-63.5,0) rot=(0,0,1;0rad)
  Shapes = -> [prism275,prism276,cube134]
FEATURE [Part::Prism] prism277
  AttacherType = Attacher::AttachEngine3D
  Circumradius = 2.375
  FirstAngle = 0
  Height = 1.29
  Placement = pos=(0,10.325,-0.645) rot=(0,0,1;0rad)
  Polygon = 10
  SecondAngle = 0
FEATURE [Part::Prism] prism278
  AttacherType = Attacher::AttachEngine3D
  Circumradius = 2.375
  FirstAngle = 0
  Height = 1.29
  Placement = pos=(0,-10.325,-0.645) rot=(0,0,1;0rad)
  Polygon = 10
  SecondAngle = 0
FEATURE [Part::Box] cube135
  AttacherType = Attacher::AttachEngine3D
  Height = 1.29
  Length = 4.75
  Placement = pos=(-2.375,-10.325,-0.645) rot=(0,0,1;0rad)
  Width = 20.65
FEATURE [Part::MultiFuse] union134
  Placement = pos=(-6.35,-63.5,0) rot=(0,0,1;0rad)
  Shapes = -> [prism277,prism278,cube135]
FEATURE [Part::Prism] prism279
  AttacherType = Attacher::AttachEngine3D
  Circumradius = 2.375
  FirstAngle = 0
  Height = 1.29
  Placement = pos=(0,10.325,-0.645) rot=(0,0,1;0rad)
  Polygon = 10
  SecondAngle = 0
FEATURE [Part::Prism] prism280
  AttacherType = Attacher::AttachEngine3D
  Circumradius = 2.375
  FirstAngle = 0
  Height = 1.29
  Placement = pos=(0,-10.325,-0.645) rot=(0,0,1;0rad)
  Polygon = 10
  SecondAngle = 0
FEATURE [Part::Box] cube136
  AttacherType = Attacher::AttachEngine3D
  Height = 1.29
  Length = 4.75
  Placement = pos=(-2.375,-10.325,-0.645) rot=(0,0,1;0rad)
  Width = 20.65
FEATURE [Part::MultiFuse] union135
  Placement = pos=(6.35,-63.5,0) rot=(0,0,1;0rad)
  Shapes = -> [prism279,prism280,cube136]
FEATURE [Part::Prism] prism281
  AttacherType = Attacher::AttachEngine3D
  Circumradius = 2.375
  FirstAngle = 0
  Height = 1.29
  Placement = pos=(0,10.325,-0.645) rot=(0,0,1;0rad)
  Polygon = 10
  SecondAngle = 0
FEATURE [Part::Prism] prism282
  AttacherType = Attacher::AttachEngine3D
  Circumradius = 2.375
  FirstAngle = 0
  Height = 1.29
  Placement = pos=(0,-10.325,-0.645) rot=(0,0,1;0rad)
  Polygon = 10
  SecondAngle = 0
FEATURE [Part::Box] cube137
  AttacherType = Attacher::AttachEngine3D
  Height = 1.29
  Length = 4.75
  Placement = pos=(-2.375,-10.325,-0.645) rot=(0,0,1;0rad)
  Width = 20.65
FEATURE [Part::MultiFuse] union136
  Placement = pos=(19.05,-63.5,0) rot=(0,0,1;0rad)
  Shapes = -> [prism281,prism282,cube137]
FEATURE [Part::Prism] prism283
  AttacherType = Attacher::AttachEngine3D
  Circumradius = 2.375
  FirstAngle = 0
  Height = 1.29
  Placement = pos=(0,10.325,-0.645) rot=(0,0,1;0rad)
  Polygon = 10
  SecondAngle = 0
FEATURE [Part::Prism] prism284
  AttacherType = Attacher::AttachEngine3D
  Circumradius = 2.375
  FirstAngle = 0
  Height = 1.29
  Placement = pos=(0,-10.325,-0.645) rot=(0,0,1;0rad)
  Polygon = 10
  SecondAngle = 0
FEATURE [Part::Box] cube138
  AttacherType = Attacher::AttachEngine3D
  Height = 1.29
  Length = 4.75
  Placement = pos=(-2.375,-10.325,-0.645) rot=(0,0,1;0rad)
  Width = 20.65
FEATURE [Part::MultiFuse] union137
  Placement = pos=(31.75,-63.5,0) rot=(0,0,1;0rad)
  Shapes = -> [prism283,prism284,cube138]
FEATURE [Part::Prism] prism285
  AttacherType = Attacher::AttachEngine3D
  Circumradius = 2.375
  FirstAngle = 0
  Height = 1.29
  Placement = pos=(0,10.325,-0.645) rot=(0,0,1;0rad)
  Polygon = 10
  SecondAngle = 0
FEATURE [Part::Prism] prism286
  AttacherType = Attacher::AttachEngine3D
  Circumradius = 2.375
  FirstAngle = 0
  Height = 1.29
  Placement = pos=(0,-10.325,-0.645) rot=(0,0,1;0rad)
  Polygon = 10
  SecondAngle = 0
FEATURE [Part::Box] cube139
  AttacherType = Attacher::AttachEngine3D
  Height = 1.29
  Length = 4.75
  Placement = pos=(-2.375,-10.325,-0.645) rot=(0,0,1;0rad)
  Width = 20.65
FEATURE [Part::MultiFuse] union138
  Placement = pos=(44.45,-63.5,0) rot=(0,0,1;0rad)
  Shapes = -> [prism285,prism286,cube139]
FEATURE [Part::Prism] prism287
  AttacherType = Attacher::AttachEngine3D
  Circumradius = 2.375
  FirstAngle = 0
  Height = 1.29
  Placement = pos=(0,10.325,-0.645) rot=(0,0,1;0rad)
  Polygon = 10
  SecondAngle = 0
FEATURE [Part::Prism] prism288
  AttacherType = Attacher::AttachEngine3D
  Circumradius = 2.375
  FirstAngle = 0
  Height = 1.29
  Placement = pos=(0,-10.325,-0.645) rot=(0,0,1;0rad)
  Polygon = 10
  SecondAngle = 0
FEATURE [Part::Box] cube140
  AttacherType = Attacher::AttachEngine3D
  Height = 1.29
  Length = 4.75
  Placement = pos=(-2.375,-10.325,-0.645) rot=(0,0,1;0rad)
  Width = 20.65
FEATURE [Part::MultiFuse] union139
  Placement = pos=(57.15,-63.5,0) rot=(0,0,1;0rad)
  Shapes = -> [prism287,prism288,cube140]
FEATURE [Part::Prism] prism289
  AttacherType = Attacher::AttachEngine3D
  Circumradius = 2.375
  FirstAngle = 0
  Height = 1.29
  Placement = pos=(0,10.325,-0.645) rot=(0,0,1;0rad)
  Polygon = 10
  SecondAngle = 0
FEATURE [Part::Prism] prism290
  AttacherType = Attacher::AttachEngine3D
  Circumradius = 2.375
  FirstAngle = 0
  Height = 1.29
  Placement = pos=(0,-10.325,-0.645) rot=(0,0,1;0rad)
  Polygon = 10
  SecondAngle = 0
FEATURE [Part::Box] cube141
  AttacherType = Attacher::AttachEngine3D
  Height = 1.29
  Length = 4.75
  Placement = pos=(-2.375,-10.325,-0.645) rot=(0,0,1;0rad)
  Width = 20.65
FEATURE [Part::MultiFuse] union140
  Placement = pos=(69.85,-63.5,0) rot=(0,0,1;0rad)
  Shapes = -> [prism289,prism290,cube141]
FEATURE [Part::Prism] prism291
  AttacherType = Attacher::AttachEngine3D
  Circumradius = 2.375
  FirstAngle = 0
  Height = 1.29
  Placement = pos=(0,10.325,-0.645) rot=(0,0,1;0rad)
  Polygon = 10
  SecondAngle = 0
FEATURE [Part::Prism] prism292
  AttacherType = Attacher::AttachEngine3D
  Circumradius = 2.375
  FirstAngle = 0
  Height = 1.29
  Placement = pos=(0,-10.325,-0.645) rot=(0,0,1;0rad)
  Polygon = 10
  SecondAngle = 0
FEATURE [Part::Box] cube142
  AttacherType = Attacher::AttachEngine3D
  Height = 1.29
  Length = 4.75
  Placement = pos=(-2.375,-10.325,-0.645) rot=(0,0,1;0rad)
  Width = 20.65
FEATURE [Part::MultiFuse] union141
  Placement = pos=(82.55,-63.5,0) rot=(0,0,1;0rad)
  Shapes = -> [prism291,prism292,cube142]
FEATURE [Part::Prism] prism293
  AttacherType = Attacher::AttachEngine3D
  Circumradius = 2.375
  FirstAngle = 0
  Height = 1.29
  Placement = pos=(0,10.325,-0.645) rot=(0,0,1;0rad)
  Polygon = 10
  SecondAngle = 0
FEATURE [Part::Prism] prism294
  AttacherType = Attacher::AttachEngine3D
  Circumradius = 2.375
  FirstAngle = 0
  Height = 1.29
  Placement = pos=(0,-10.325,-0.645) rot=(0,0,1;0rad)
  Polygon = 10
  SecondAngle = 0
FEATURE [Part::Box] cube143
  AttacherType = Attacher::AttachEngine3D
  Height = 1.29
  Length = 4.75
  Placement = pos=(-2.375,-10.325,-0.645) rot=(0,0,1;0rad)
  Width = 20.65
FEATURE [Part::MultiFuse] union142
  Placement = pos=(95.25,-63.5,0) rot=(0,0,1;0rad)
  Shapes = -> [prism293,prism294,cube143]
FEATURE [Part::Prism] prism295
  AttacherType = Attacher::AttachEngine3D
  Circumradius = 2.375
  FirstAngle = 0
  Height = 1.29
  Placement = pos=(0,10.325,-0.645) rot=(0,0,1;0rad)
  Polygon = 10
  SecondAngle = 0
FEATURE [Part::Prism] prism296
  AttacherType = Attacher::AttachEngine3D
  Circumradius = 2.375
  FirstAngle = 0
  Height = 1.29
  Placement = pos=(0,-10.325,-0.645) rot=(0,0,1;0rad)
  Polygon = 10
  SecondAngle = 0
FEATURE [Part::Box] cube144
  AttacherType = Attacher::AttachEngine3D
  Height = 1.29
  Length = 4.75
  Placement = pos=(-2.375,-10.325,-0.645) rot=(0,0,1;0rad)
  Width = 20.65
FEATURE [Part::MultiFuse] union143
  Placement = pos=(107.95,-63.5,0) rot=(0,0,1;0rad)
  Shapes = -> [prism295,prism296,cube144]
FEATURE [Part::Prism] prism297
  AttacherType = Attacher::AttachEngine3D
  Circumradius = 2.375
  FirstAngle = 0
  Height = 1.29
  Placement = pos=(0,10.325,-0.645) rot=(0,0,1;0rad)
  Polygon = 10
  SecondAngle = 0
FEATURE [Part::Prism] prism298
  AttacherType = Attacher::AttachEngine3D
  Circumradius = 2.375
  FirstAngle = 0
  Height = 1.29
  Placement = pos=(0,-10.325,-0.645) rot=(0,0,1;0rad)
  Polygon = 10
  SecondAngle = 0
FEATURE [Part::Box] cube145
  AttacherType = Attacher::AttachEngine3D
  Height = 1.29
  Length = 4.75
  Placement = pos=(-2.375,-10.325,-0.645) rot=(0,0,1;0rad)
  Width = 20.65
FEATURE [Part::MultiFuse] union144
  Placement = pos=(120.65,-63.5,0) rot=(0,0,1;0rad)
  Shapes = -> [prism297,prism298,cube145]
FEATURE [Part::Prism] prism299
  AttacherType = Attacher::AttachEngine3D
  Circumradius = 2.375
  FirstAngle = 0
  Height = 1.29
  Placement = pos=(0,10.325,-0.645) rot=(0,0,1;0rad)
  Polygon = 10
  SecondAngle = 0
FEATURE [Part::Prism] prism300
  AttacherType = Attacher::AttachEngine3D
  Circumradius = 2.375
  FirstAngle = 0
  Height = 1.29
  Placement = pos=(0,-10.325,-0.645) rot=(0,0,1;0rad)
  Polygon = 10
  SecondAngle = 0
FEATURE [Part::Box] cube146
  AttacherType = Attacher::AttachEngine3D
  Height = 1.29
  Length = 4.75
  Placement = pos=(-2.375,-10.325,-0.645) rot=(0,0,1;0rad)
  Width = 20.65
FEATURE [Part::MultiFuse] union145
  Placement = pos=(133.35,-63.5,0) rot=(0,0,1;0rad)
  Shapes = -> [prism299,prism300,cube146]
FEATURE [Part::Prism] prism301
  AttacherType = Attacher::AttachEngine3D
  Circumradius = 2.375
  FirstAngle = 0
  Height = 1.29
  Placement = pos=(0,10.325,-0.645) rot=(0,0,1;0rad)
  Polygon = 10
  SecondAngle = 0
FEATURE [Part::Prism] prism302
  AttacherType = Attacher::AttachEngine3D
  Circumradius = 2.375
  FirstAngle = 0
  Height = 1.29
  Placement = pos=(0,-10.325,-0.645) rot=(0,0,1;0rad)
  Polygon = 10
  SecondAngle = 0
FEATURE [Part::Box] cube147
  AttacherType = Attacher::AttachEngine3D
  Height = 1.29
  Length = 4.75
  Placement = pos=(-2.375,-10.325,-0.645) rot=(0,0,1;0rad)
  Width = 20.65
FEATURE [Part::MultiFuse] union146
  Placement = pos=(146.05,-63.5,0) rot=(0,0,1;0rad)
  Shapes = -> [prism301,prism302,cube147]
FEATURE [Part::Prism] prism303
  AttacherType = Attacher::AttachEngine3D
  Circumradius = 2.375
  FirstAngle = 0
  Height = 1.29
  Placement = pos=(0,10.325,-0.645) rot=(0,0,1;0rad)
  Polygon = 10
  SecondAngle = 0
FEATURE [Part::Prism] prism304
  AttacherType = Attacher::AttachEngine3D
  Circumradius = 2.375
  FirstAngle = 0
  Height = 1.29
  Placement = pos=(0,-10.325,-0.645) rot=(0,0,1;0rad)
  Polygon = 10
  SecondAngle = 0
FEATURE [Part::Box] cube148
  AttacherType = Attacher::AttachEngine3D
  Height = 1.29
  Length = 4.75
  Placement = pos=(-2.375,-10.325,-0.645) rot=(0,0,1;0rad)
  Width = 20.65
FEATURE [Part::MultiFuse] union147
  Placement = pos=(158.75,-63.5,0) rot=(0,0,1;0rad)
  Shapes = -> [prism303,prism304,cube148]
FEATURE [Part::Prism] prism305
  AttacherType = Attacher::AttachEngine3D
  Circumradius = 2.375
  FirstAngle = 0
  Height = 1.29
  Placement = pos=(0,10.325,-0.645) rot=(0,0,1;0rad)
  Polygon = 10
  SecondAngle = 0
FEATURE [Part::Prism] prism306
  AttacherType = Attacher::AttachEngine3D
  Circumradius = 2.375
  FirstAngle = 0
  Height = 1.29
  Placement = pos=(0,-10.325,-0.645) rot=(0,0,1;0rad)
  Polygon = 10
  SecondAngle = 0
FEATURE [Part::Box] cube149
  AttacherType = Attacher::AttachEngine3D
  Height = 1.29
  Length = 4.75
  Placement = pos=(-2.375,-10.325,-0.645) rot=(0,0,1;0rad)
  Width = 20.65
FEATURE [Part::MultiFuse] union148
  Placement = pos=(171.45,-63.5,0) rot=(0,0,1;0rad)
  Shapes = -> [prism305,prism306,cube149]
FEATURE [Part::Prism] prism307
  AttacherType = Attacher::AttachEngine3D
  Circumradius = 2.375
  FirstAngle = 0
  Height = 1.29
  Placement = pos=(0,10.325,-0.645) rot=(0,0,1;0rad)
  Polygon = 10
  SecondAngle = 0
FEATURE [Part::Prism] prism308
  AttacherType = Attacher::AttachEngine3D
  Circumradius = 2.375
  FirstAngle = 0
  Height = 1.29
  Placement = pos=(0,-10.325,-0.645) rot=(0,0,1;0rad)
  Polygon = 10
  SecondAngle = 0
FEATURE [Part::Box] cube150
  AttacherType = Attacher::AttachEngine3D
  Height = 1.29
  Length = 4.75
  Placement = pos=(-2.375,-10.325,-0.645) rot=(0,0,1;0rad)
  Width = 20.65
FEATURE [Part::MultiFuse] union149
  Placement = pos=(184.15,-63.5,0) rot=(0,0,1;0rad)
  Shapes = -> [prism307,prism308,cube150]
FEATURE [Part::MultiFuse] Group004
  Shapes = -> [union120,union121,union122,union123,union124,union125,union126,union127,union128,union129,union130,union131,union132,union133,union134,union135,union136,union137,union138,union139,union140,union141,union142,union143,union144,union145,union146,union147,union148,union149]
FEATURE [Part::MultiFuse] Group005
  Shapes = -> [Group,Group001,Group002,Group003,Group004]
FEATURE [Part::MultiFuse] union150
  Shapes = -> [prism,prism001,prism002,prism003,prism004,prism005,prism006,prism007,prism008,Group005]
FEATURE [Part::Cut] difference  label="cover import"
  Base = -> cube
  Tool = -> union150
FEATURE [PartDesign::FeatureBase] BaseFeature
  BaseFeature = -> difference
FEATURE [PartDesign::Body] Body  label="Cover Body"
  BaseFeature = -> difference
  Group = -> [BaseFeature]
  Origin = -> Origin
  Placement = pos=(0,0,19) rot=(0,0,1;0rad)
  Tip = -> BaseFeature
FEATURE [Part::Box] cube151
  AttacherType = Attacher::AttachEngine3D
  Height = 44.45
  Length = 482.6
  Placement = pos=(-241.3,-1.525,-22.225) rot=(0,0,1;0rad)
  Width = 3.05
FEATURE [Part::Prism] prism309
  AttacherType = Attacher::AttachEngine3D
  Circumradius = 1.98
  FirstAngle = 0
  Height = 3.07
  Placement = pos=(-206.375,1.535,-12.345) rot=(1,0,0;1.5708rad)
  Polygon = 20
  SecondAngle = 0
FEATURE [Part::Prism] prism310
  AttacherType = Attacher::AttachEngine3D
  Circumradius = 1.98
  FirstAngle = 0
  Height = 3.07
  Placement = pos=(-206.375,1.535,12.345) rot=(1,0,0;1.5708rad)
  Polygon = 20
  SecondAngle = 0
FEATURE [Part::Prism] prism311
  AttacherType = Attacher::AttachEngine3D
  Circumradius = 1.98
  FirstAngle = 0
  Height = 3.07
  Placement = pos=(206.375,1.535,-12.345) rot=(1,0,0;1.5708rad)
  Polygon = 20
  SecondAngle = 0
FEATURE [Part::Prism] prism312
  AttacherType = Attacher::AttachEngine3D
  Circumradius = 1.98
  FirstAngle = 0
  Height = 3.07
  Placement = pos=(206.375,1.535,12.345) rot=(1,0,0;1.5708rad)
  Polygon = 20
  SecondAngle = 0
FEATURE [Part::Prism] prism313
  AttacherType = Attacher::AttachEngine3D
  Circumradius = 3.53
  FirstAngle = 0
  Height = 3.07
  Placement = pos=(-1.625,1.535,0) rot=(1,0,0;1.5708rad)
  Polygon = 20
  SecondAngle = 0
FEATURE [Part::Prism] prism314
  AttacherType = Attacher::AttachEngine3D
  Circumradius = 3.53
  FirstAngle = 0
  Height = 3.07
  Placement = pos=(1.625,1.535,0) rot=(1,0,0;1.5708rad)
  Polygon = 20
  SecondAngle = 0
FEATURE [Part::Box] cube152
  AttacherType = Attacher::AttachEngine3D
  Height = 7.06
  Length = 3.25
  Placement = pos=(-1.625,-1.535,-3.53) rot=(0,0,1;0rad)
  Width = 3.07
FEATURE [Part::MultiFuse] union151
  Placement = pos=(232.97,0,15.875) rot=(0,0,1;0rad)
  Shapes = -> [prism313,prism314,cube152]
FEATURE [Part::Prism] prism315
  AttacherType = Attacher::AttachEngine3D
  Circumradius = 3.53
  FirstAngle = 0
  Height = 3.07
  Placement = pos=(-1.625,1.535,0) rot=(1,0,0;1.5708rad)
  Polygon = 20
  SecondAngle = 0
FEATURE [Part::Prism] prism316
  AttacherType = Attacher::AttachEngine3D
  Circumradius = 3.53
  FirstAngle = 0
  Height = 3.07
  Placement = pos=(1.625,1.535,0) rot=(1,0,0;1.5708rad)
  Polygon = 20
  SecondAngle = 0
FEATURE [Part::Box] cube153
  AttacherType = Attacher::AttachEngine3D
  Height = 7.06
  Length = 3.25
  Placement = pos=(-1.625,-1.535,-3.53) rot=(0,0,1;0rad)
  Width = 3.07
FEATURE [Part::MultiFuse] union152
  Placement = pos=(232.97,0,-15.875) rot=(0,0,1;0rad)
  Shapes = -> [prism315,prism316,cube153]
FEATURE [Part::Prism] prism317
  AttacherType = Attacher::AttachEngine3D
  Circumradius = 3.53
  FirstAngle = 0
  Height = 3.07
  Placement = pos=(-1.625,1.535,0) rot=(1,0,0;1.5708rad)
  Polygon = 20
  SecondAngle = 0
FEATURE [Part::Prism] prism318
  AttacherType = Attacher::AttachEngine3D
  Circumradius = 3.53
  FirstAngle = 0
  Height = 3.07
  Placement = pos=(1.625,1.535,0) rot=(1,0,0;1.5708rad)
  Polygon = 20
  SecondAngle = 0
FEATURE [Part::Box] cube154
  AttacherType = Attacher::AttachEngine3D
  Height = 7.06
  Length = 3.25
  Placement = pos=(-1.625,-1.535,-3.53) rot=(0,0,1;0rad)
  Width = 3.07
FEATURE [Part::MultiFuse] union153
  Placement = pos=(-232.97,0,15.875) rot=(0,0,1;0rad)
  Shapes = -> [prism317,prism318,cube154]
FEATURE [Part::Prism] prism319
  AttacherType = Attacher::AttachEngine3D
  Circumradius = 3.53
  FirstAngle = 0
  Height = 3.07
  Placement = pos=(-1.625,1.535,0) rot=(1,0,0;1.5708rad)
  Polygon = 20
  SecondAngle = 0
FEATURE [Part::Prism] prism320
  AttacherType = Attacher::AttachEngine3D
  Circumradius = 3.53
  FirstAngle = 0
  Height = 3.07
  Placement = pos=(1.625,1.535,0) rot=(1,0,0;1.5708rad)
  Polygon = 20
  SecondAngle = 0
FEATURE [Part::Box] cube155
  AttacherType = Attacher::AttachEngine3D
  Height = 7.06
  Length = 3.25
  Placement = pos=(-1.625,-1.535,-3.53) rot=(0,0,1;0rad)
  Width = 3.07
FEATURE [Part::MultiFuse] union154
  Placement = pos=(-232.97,0,-15.875) rot=(0,0,1;0rad)
  Shapes = -> [prism319,prism320,cube155]
FEATURE [Part::MultiFuse] union155
  Shapes = -> [prism309,prism310,prism311,prism312,union151,union152,union153,union154]
FEATURE [Part::Cut] difference001  label="front plate import"
  Base = -> cube151
  Tool = -> union155
FEATURE [PartDesign::FeatureBase] BaseFeature001
  BaseFeature = -> difference001
FEATURE [PartDesign::Body] Body001  label="Front Plate Body"
  BaseFeature = -> difference001
  Group = -> [BaseFeature001]
  Origin = -> Origin001
  Placement = pos=(0,103,0) rot=(0,0,1;0rad)
  Tip = -> BaseFeature001
FEATURE [Part::Box] cube156
  AttacherType = Attacher::AttachEngine3D
  Height = 1.27
  Length = 431.8
  Placement = pos=(-215.9,-101.6,-18.885) rot=(0,0,1;0rad)
  Width = 203.2
FEATURE [Part::Box] cube157
  AttacherType = Attacher::AttachEngine3D
  Height = 36.5
  Length = 1.27
  Placement = pos=(215.265,-101.6,-18.25) rot=(0,0,1;0rad)
  Width = 203.2
FEATURE [Part::Box] cube158
  AttacherType = Attacher::AttachEngine3D
  Height = 36.5
  Length = 1.27
  Placement = pos=(-216.535,-101.6,-18.25) rot=(0,0,1;0rad)
  Width = 203.2
FEATURE [Part::Box] cube159
  AttacherType = Attacher::AttachEngine3D
  Height = 36.5
  Length = 431.8
  Placement = pos=(-215.9,100.965,-18.25) rot=(0,0,1;0rad)
  Width = 1.27
FEATURE [Part::Box] cube160
  AttacherType = Attacher::AttachEngine3D
  Height = 36.5
  Length = 19.05
  Placement = pos=(-215.9,-102.235,-18.25) rot=(0,0,1;0rad)
  Width = 1.27
FEATURE [Part::Box] cube161
  AttacherType = Attacher::AttachEngine3D
  Height = 36.5
  Length = 19.05
  Placement = pos=(196.85,-102.235,-18.25) rot=(0,0,1;0rad)
  Width = 1.27
FEATURE [Part::Feature] wire
  shape: bbox 431.8 x 203.2 x 2e-07 mm, 1 faces, 0 solids (baked)
FEATURE [Part::FeaturePython] RefineLinearExtrude  # WARN: FeaturePython — macro-defined, semantics opaque (R4)
  Base = -> wire
FEATURE [Part::Extrusion] LinearExtrude
  Base = -> RefineLinearExtrude
  Dir = (0,0,1.27)
  DirMode = 0
  FaceMakerClass = Part::FaceMakerBullseye
  LengthFwd = 0
  LengthRev = 0
  Placement = pos=(0,0,17.615) rot=(0,0,1;0rad)
  Solid = false
  Symmetric = false
FEATURE [Part::MultiFuse] union156
  Shapes = -> [cube156,cube157,cube158,cube159,cube160,cube161,LinearExtrude]
FEATURE [Part::Prism] prism321
  AttacherType = Attacher::AttachEngine3D
  Circumradius = 1.98
  FirstAngle = 0
  Height = 1.29
  Placement = pos=(206.375,-100.955,12.345) rot=(1,0,0;1.5708rad)
  Polygon = 20
  SecondAngle = 0
FEATURE [Part::Prism] prism322
  AttacherType = Attacher::AttachEngine3D
  Circumradius = 1.98
  FirstAngle = 0
  Height = 1.29
  Placement = pos=(206.375,-100.955,-12.345) rot=(1,0,0;1.5708rad)
  Polygon = 20
  SecondAngle = 0
FEATURE [Part::Prism] prism323
  AttacherType = Attacher::AttachEngine3D
  Circumradius = 1.98
  FirstAngle = 0
  Height = 1.29
  Placement = pos=(-206.375,-100.955,12.345) rot=(1,0,0;1.5708rad)
  Polygon = 20
  SecondAngle = 0
FEATURE [Part::Prism] prism324
  AttacherType = Attacher::AttachEngine3D
  Circumradius = 1.98
  FirstAngle = 0
  Height = 1.29
  Placement = pos=(-206.375,-100.955,-12.345) rot=(1,0,0;1.5708rad)
  Polygon = 20
  SecondAngle = 0
FEATURE [Part::Prism] prism325
  AttacherType = Attacher::AttachEngine3D
  Circumradius = 1.98
  FirstAngle = 0
  Height = 1.29
  Placement = pos=(-206.375,0,17.605) rot=(0,0,1;0rad)
  Polygon = 20
  SecondAngle = 0
FEATURE [Part::Prism] prism326
  AttacherType = Attacher::AttachEngine3D
  Circumradius = 1.98
  FirstAngle = 0
  Height = 1.29
  Placement = pos=(-206.375,76.2,17.605) rot=(0,0,1;0rad)
  Polygon = 20
  SecondAngle = 0
FEATURE [Part::Prism] prism327
  AttacherType = Attacher::AttachEngine3D
  Circumradius = 1.98
  FirstAngle = 0
  Height = 1.29
  Placement = pos=(-206.375,-76.2,17.605) rot=(0,0,1;0rad)
  Polygon = 20
  SecondAngle = 0
FEATURE [Part::Prism] prism328
  AttacherType = Attacher::AttachEngine3D
  Circumradius = 1.98
  FirstAngle = 0
  Height = 1.29
  Placement = pos=(206.375,0,17.605) rot=(0,0,1;0rad)
  Polygon = 20
  SecondAngle = 0
FEATURE [Part::Prism] prism329
  AttacherType = Attacher::AttachEngine3D
  Circumradius = 1.98
  FirstAngle = 0
  Height = 1.29
  Placement = pos=(206.375,76.2,17.605) rot=(0,0,1;0rad)
  Polygon = 20
  SecondAngle = 0
FEATURE [Part::Prism] prism330
  AttacherType = Attacher::AttachEngine3D
  Circumradius = 1.98
  FirstAngle = 0
  Height = 1.29
  Placement = pos=(206.375,-76.2,17.605) rot=(0,0,1;0rad)
  Polygon = 20
  SecondAngle = 0
FEATURE [Part::Prism] prism331
  AttacherType = Attacher::AttachEngine3D
  Circumradius = 1.98
  FirstAngle = 0
  Height = 1.29
  Placement = pos=(0,92.075,17.605) rot=(0,0,1;0rad)
  Polygon = 20
  SecondAngle = 0
FEATURE [Part::Prism] prism332
  AttacherType = Attacher::AttachEngine3D
  Circumradius = 1.98
  FirstAngle = 0
  Height = 1.29
  Placement = pos=(-190.5,92.075,17.605) rot=(0,0,1;0rad)
  Polygon = 20
  SecondAngle = 0
FEATURE [Part::Prism] prism333
  AttacherType = Attacher::AttachEngine3D
  Circumradius = 1.98
  FirstAngle = 0
  Height = 1.29
  Placement = pos=(190.5,92.075,17.605) rot=(0,0,1;0rad)
  Polygon = 20
  SecondAngle = 0
FEATURE [Part::Prism] prism334
  AttacherType = Attacher::AttachEngine3D
  Circumradius = 2.37
  FirstAngle = 0
  Height = 1.29
  Placement = pos=(215.255,-63.5,-1e-16) rot=(0,1,0;1.5708rad)
  Polygon = 20
  SecondAngle = 0
FEATURE [Part::Prism] prism335
  AttacherType = Attacher::AttachEngine3D
  Circumradius = 2.37
  FirstAngle = 0
  Height = 1.29
  Placement = pos=(215.255,38.1,-1e-16) rot=(0,1,0;1.5708rad)
  Polygon = 20
  SecondAngle = 0
FEATURE [Part::Prism] prism336
  AttacherType = Attacher::AttachEngine3D
  Circumradius = 2.37
  FirstAngle = 0
  Height = 1.29
  Placement = pos=(215.255,88.9,-1e-16) rot=(0,1,0;1.5708rad)
  Polygon = 20
  SecondAngle = 0
FEATURE [Part::Prism] prism337
  AttacherType = Attacher::AttachEngine3D
  Circumradius = 2.37
  FirstAngle = 0
  Height = 1.29
  Placement = pos=(-216.545,-63.5,-1e-16) rot=(0,1,0;1.5708rad)
  Polygon = 20
  SecondAngle = 0
FEATURE [Part::Prism] prism338
  AttacherType = Attacher::AttachEngine3D
  Circumradius = 2.37
  FirstAngle = 0
  Height = 1.29
  Placement = pos=(-216.545,38.1,-1e-16) rot=(0,1,0;1.5708rad)
  Polygon = 20
  SecondAngle = 0
FEATURE [Part::Prism] prism339
  AttacherType = Attacher::AttachEngine3D
  Circumradius = 2.37
  FirstAngle = 0
  Height = 1.29
  Placement = pos=(-216.545,88.9,-1e-16) rot=(0,1,0;1.5708rad)
  Polygon = 20
  SecondAngle = 0
FEATURE [Part::MultiFuse] union157
  Shapes = -> [prism321,prism322,prism323,prism324,prism325,prism326,prism327,prism328,prism329,prism330,prism331,prism332,prism333,prism334,prism335,prism336,prism337,prism338,prism339]
FEATURE [Part::Cut] difference002  label="chassis import"
  Base = -> union156
  Tool = -> union157
FEATURE [App::DocumentObjectGroup] Group008  label="Chassis"
  Group = -> [wire,difference002]
FEATURE [App::DocumentObjectGroup] Group006  label="Import"
  Group = -> [difference,difference001,Group008]
FEATURE [PartDesign::FeatureBase] BaseFeature002
  BaseFeature = -> difference002
FEATURE [PartDesign::Body] Body002  label="Chassis Body"
  BaseFeature = -> difference002
  Group = -> [BaseFeature002]
  Origin = -> Origin002
  Placement = pos=(0,0,0) rot=(0,0,1;3.14159rad)
  Tip = -> BaseFeature002
FEATURE [Part::Feature] Shape008  label="R20_R_0603_1608Metric_5FA65FDD"
  Placement = pos=(121.285,-82.55,-1.6) rot=(0.707107,-0.707107,0;3.14159rad)
  shape: bbox 0.8 x 1.6 x 0.45 mm, 26 faces (baked)
FEATURE [Part::Feature] Shape037  label="J2_TerminalBlock_1x02_P2_54mm_Horizontal_5FA65D49[2]"
  Placement = pos=(122.428,-61.722,0) rot=(0,0,1;3.14159rad)
  shape: bbox 5.08 x 6.5 x 12 mm, 313 faces, 5 solids (baked)
FEATURE [Part::Feature] Shape027  label="Q2_TO-126-3_Vertical_5FA65E89"
  Placement = pos=(129.54,-81.661,0) rot=(0,0,-1;1.5708rad)
  shape: bbox 3.25 x 8 x 23.75 mm, 66 faces (baked)
FEATURE [Part::Feature] Shape046  label="D4_TO_252_2_5FA7BC4F"
  Placement = pos=(41.864,-103.659,-1.6) rot=(0.707107,-0.707107,0;3.14159rad)
  shape: bbox 6.5 x 9.9 x 2.32 mm, 80 faces (baked)
FEATURE [Part::Feature] Shape064  label="C10_C_0805_2012Metric_5FA9033A"
  Placement = pos=(111.76,-70.104,-1.6) rot=(0.707107,0.707107,0;3.14159rad)
  shape: bbox 1.25 x 2 x 1.25 mm, 28 faces (baked)
FEATURE [Part::Feature] Shape062  label="C12_C_0603_1608Metric_5FA7BAAA"
  Placement = pos=(66.04,-100.089,-1.6) rot=(0.707107,0.707107,0;3.14159rad)
  shape: bbox 0.8 x 1.6 x 0.8 mm, 28 faces (baked)
FEATURE [Part::Feature] Shape068  label="C6_C_0603_1608Metric_5FA659BD"
  Placement = pos=(115.062,-69.85,-1.6) rot=(0.707107,-0.707107,0;3.14159rad)
  shape: bbox 0.8 x 1.6 x 0.8 mm, 28 faces (baked)
FEATURE [Part::Feature] Shape021  label="R6_R_0603_1608Metric_5FA65EEF"
  Placement = pos=(106.934,-82.55,-1.6) rot=(0.707107,0.707107,0;3.14159rad)
  shape: bbox 0.8 x 1.6 x 0.45 mm, 26 faces (baked)
FEATURE [Part::Feature] Shape066  label="C8_C_0805_2012Metric_5FA8F9C6"
  Placement = pos=(116.459,-82.677,-1.6) rot=(0.707107,-0.707107,0;3.14159rad)
  shape: bbox 1.25 x 2 x 1.25 mm, 28 faces (baked)
FEATURE [Part::Feature] Shape042  label="D8_TO_252_2_5FA7BCB8"
  Placement = pos=(48.958,-103.659,-1.6) rot=(0.707107,-0.707107,0;3.14159rad)
  shape: bbox 6.5 x 9.9 x 2.32 mm, 80 faces (baked)
FEATURE [Part::Feature] Shape052  label="C22_CP_Elec_8x105_5FA65B29"
  Placement = pos=(110.236,-95.504,0) rot=(0,0,1;1.5708rad)
  shape: bbox 10.92 x 10.73 x 10.5 mm, 41 faces (baked)
FEATURE [Part::Feature] Shape020  label="R7_R_0603_1608Metric_5FA65F00"
  Placement = pos=(111.633,-82.55,-1.6) rot=(0.707107,-0.707107,0;3.14159rad)
  shape: bbox 0.8 x 1.6 x 0.45 mm, 26 faces (baked)
FEATURE [Part::Feature] Shape041  label="D9_D_0603_5FA65C7E"
  Placement = pos=(28.702,-111.785,0) rot=(0,0,-1;1.5708rad)
  shape: bbox 0.87 x 1.6 x 0.66 mm, 39 faces (baked)
FEATURE [Part::Feature] Shape034  label="J5_TerminalBlock_1x02_P2_54mm_Horizontal_5FA65DAD[2]"
  Placement = pos=(96.266,-118.364,0) rot=(0,0,1;0rad)
  shape: bbox 5.08 x 6.5 x 12 mm, 313 faces, 5 solids (baked)
FEATURE [Part::Feature] Shape053  label="C21_CP_Elec_8x105_5FA65B01"
  Placement = pos=(110.236,-108.094,0) rot=(0,0,1;1.5708rad)
  shape: bbox 10.92 x 10.73 x 10.5 mm, 41 faces (baked)
FEATURE [Part::Feature] Shape072  label="C1_C_0603_1608Metric_5FA6593A"
  Placement = pos=(106.934,-69.863,-1.6) rot=(0.707107,0.707107,0;3.14159rad)
  shape: bbox 0.8 x 1.6 x 0.8 mm, 28 faces (baked)
FEATURE [Part::Feature] Shape054  label="C20_C_0805_2012Metric_5FA65AD9"
  Placement = pos=(124.587,-82.804,-1.6) rot=(0.707107,-0.707107,0;3.14159rad)
  shape: bbox 1.25 x 2 x 1.25 mm, 28 faces (baked)
FEATURE [Part::Feature] Shape006  label="U1_SOIC_8_39x49mm_P127mm_5FA8D475"
  Placement = pos=(110.236,-75.819,0) rot=(0,0,1;0rad)
  shape: bbox 6 x 4.9 x 1.75 mm, 156 faces (baked)
FEATURE [Part::Feature] Shape003  label="U4_TO_252_2_5FA7BD25"
  Placement = pos=(63.754,-92.524,-1.6) rot=(0.707107,0.707107,0;3.14159rad)
  shape: bbox 6.5 x 9.9 x 2.32 mm, 80 faces (baked)
FEATURE [Part::Feature] Shape058  label="C16_C_0603_1608Metric_5FA7BB3A"
  Placement = pos=(56.388,-100.089,-1.6) rot=(0.707107,-0.707107,0;3.14159rad)
  shape: bbox 0.8 x 1.6 x 0.8 mm, 28 faces (baked)
FEATURE [Part::Feature] Shape010  label="R17_R_1210_3225Metric_5FA9311C"
  Placement = pos=(125.984,-82.677,0) rot=(0,0,-1;1.5708rad)
  shape: bbox 2.5 x 3.2 x 0.55 mm, 26 faces (baked)
FEATURE [Part::Feature] Shape009  label="R19_R_0603_1608Metric_5FA65FCC"
  Placement = pos=(118.237,-82.55,-1.6) rot=(0.707107,-0.707107,0;3.14159rad)
  shape: bbox 0.8 x 1.6 x 0.45 mm, 26 faces (baked)
FEATURE [Sketcher::SketchObject] PCB_Sketch_132a
  sketch-geometry (4):
    g0: LineSegment StartX=131.826 StartY=-57.912 StartZ=0 EndX=131.826 EndY=-122.428 EndZ=0
    g1: LineSegment StartX=22.86 StartY=-57.912 StartZ=0 EndX=22.86 EndY=-122.428 EndZ=0
    g2: LineSegment StartX=22.86 StartY=-122.428 StartZ=0 EndX=131.826 EndY=-122.428 EndZ=0
    g3: LineSegment StartX=22.86 StartY=-57.912 StartZ=0 EndX=131.826 EndY=-57.912 EndZ=0
  constraints (4):
    c: Coincident(g1,g2)
    c: Coincident(g1,g3)
    c: Coincident(g0,g2)
    c: Coincident(g0,g3)
FEATURE [Part::Feature] Shape019  label="R8_R_0603_1608Metric_5FA8CC03"
  Placement = pos=(116.586,-69.85,-1.6) rot=(0.707107,0.707107,0;3.14159rad)
  shape: bbox 0.8 x 1.6 x 0.45 mm, 26 faces (baked)
FEATURE [Part::Feature] Shape036  label="J3_TerminalBlock_1x02_P2_54mm_Horizontal_5FA65D69[2]"
  Placement = pos=(107.696,-61.722,0) rot=(0,0,1;3.14159rad)
  shape: bbox 5.08 x 6.5 x 12 mm, 313 faces, 5 solids (baked)
FEATURE [PartDesign::CoordinateSystem] Local_CS_132a
  AttacherType = Attacher::AttachEngine3D
FEATURE [Part::Feature] Shape059  label="C15_C_0805_2012Metric_5FA7BB0A"
  Placement = pos=(61.468,-100.264,-1.6) rot=(0.707107,0.707107,0;3.14159rad)
  shape: bbox 1.25 x 2 x 1.25 mm, 28 faces (baked)
FEATURE [Part::Feature] Shape018  label="R9_R_0603_1608Metric_5FA7553F"
  Placement = pos=(30.48,-111.823,0) rot=(0,0,1;1.5708rad)
  shape: bbox 0.8 x 1.6 x 0.45 mm, 26 faces (baked)
FEATURE [Part::Feature] Shape038  label="J1_OSTTA03416_5FA65D29"
  Placement = pos=(26.864,-96.89,0) rot=(0,0,-1;1.5708rad)
  shape: bbox 9.1 x 15.94 x 17.5 mm, 576 faces (baked)
FEATURE [Part::Feature] Shape015  label="R12_R_0603_1608Metric_5FA65F55"
  Placement = pos=(113.157,-82.55,-1.6) rot=(0.707107,-0.707107,0;3.14159rad)
  shape: bbox 0.8 x 1.6 x 0.45 mm, 26 faces (baked)
FEATURE [Part::Feature] Shape016  label="R11_R_1210_3225Metric_5FA65F44"
  Placement = pos=(116.586,-94.234,0) rot=(0,0,1;1.5708rad)
  shape: bbox 2.5 x 3.2 x 0.55 mm, 26 faces (baked)
FEATURE [Part::Feature] Shape031  label="J8_TerminalBlock_1x03_P2_54mm_Horizontal_5FA65E15"
  Placement = pos=(100.33,-61.722,0) rot=(0,0,1;3.14159rad)
  shape: bbox 7.62 x 6.5 x 12 mm, 465 faces, 7 solids (baked)
FEATURE [Part::Feature] Shape001  label="R18_R_0603_1608Metric_5FA65FBB"
  Placement = pos=(119.761,-82.55,-1.6) rot=(0.707107,-0.707107,0;3.14159rad)
  shape: bbox 0.8 x 1.6 x 0.45 mm, 26 faces (baked)
FEATURE [Part::Feature] Shape056  label="C18_C_0603_1608Metric_5FA8EEAF"
  Placement = pos=(108.458,-69.85,-1.6) rot=(0.707107,0.707107,0;3.14159rad)
  shape: bbox 0.8 x 1.6 x 0.8 mm, 28 faces (baked)
FEATURE [Part::Feature] Shape011  label="R16_R_1210_3225Metric_5FA8AFC6"
  Placement = pos=(126.238,-101.407,0) rot=(0,0,-1;1.5708rad)
  shape: bbox 2.5 x 3.2 x 0.55 mm, 26 faces (baked)
FEATURE [Part::Feature] Shape002  label="C3_CP_Elec_18x22_5FA65973"
  Placement = pos=(95.404,-102.77,0) rot=(0,0,1;1.5708rad)
  shape: bbox 24.31 x 24.3 x 22 mm, 41 faces (baked)
FEATURE [Part::Feature] Shape044  label="D6_TO_252_2_5FA7BBE6"
  Placement = pos=(70.858,-103.659,-1.6) rot=(0.707107,-0.707107,0;3.14159rad)
  shape: bbox 6.5 x 9.9 x 2.32 mm, 80 faces (baked)
FEATURE [Part::Feature] Shape014  label="R13_R_0603_1608Metric_5FA65F66"
  Placement = pos=(109.982,-69.85,-1.6) rot=(0.707107,0.707107,0;3.14159rad)
  shape: bbox 0.8 x 1.6 x 0.45 mm, 26 faces (baked)
FEATURE [Part::Feature] Shape039  label="D11_D_MiniMELF_Standard_5FA89F90"
  Placement = pos=(129.159,-89.662,0) rot=(0,0,1;0rad)
  shape: bbox 3.6 x 1.4 x 1.4 mm, 13 faces (baked)
FEATURE [Part::Feature] Shape061  label="C13_CP_Elec_4x58_5FA65A62"
  Placement = pos=(122.809,-90.678,0) rot=(0,0,1;0rad)
  shape: bbox 5.738 x 5.462 x 5.8 mm, 41 faces (baked)
FEATURE [Part::Feature] Shape040  label="D10_D_MiniMELF_Standard_5FA65C97"
  Placement = pos=(129.159,-91.948,0) rot=(0,0,1;0rad)
  shape: bbox 3.6 x 1.4 x 1.4 mm, 13 faces (baked)
FEATURE [Part::Feature] Shape055  label="C19_C_0603_1608Metric_5FA65AC8"
  Placement = pos=(108.458,-82.55,-1.6) rot=(0.707107,0.707107,0;3.14159rad)
  shape: bbox 0.8 x 1.6 x 0.8 mm, 28 faces (baked)
FEATURE [Part::Feature] Shape005  label="U2_SOIC_8_39x49mm_P127mm_5FA8C6D7"
  Placement = pos=(118.618,-75.819,0) rot=(0,0,1;0rad)
  shape: bbox 6 x 4.9 x 1.75 mm, 156 faces (baked)
FEATURE [Part::Feature] Shape032  label="J7_TerminalBlock_1x03_P2_54mm_Horizontal_5FA65DF1"
  Placement = pos=(124.46,-118.618,0) rot=(0,0,1;0rad)
  shape: bbox 7.62 x 6.5 x 12 mm, 465 faces, 7 solids (baked)
FEATURE [Part::Feature] Shape025  label="R2_R_0603_1608Metric_5FA65EAB"
  Placement = pos=(105.41,-82.55,-1.6) rot=(0.707107,0.707107,0;3.14159rad)
  shape: bbox 0.8 x 1.6 x 0.45 mm, 26 faces (baked)
FEATURE [Part::Feature] Shape007  label="R21_R_0603_1608Metric_5FA8BFFB"
  Placement = pos=(122.809,-82.55,-1.6) rot=(0.707107,-0.707107,0;3.14159rad)
  shape: bbox 0.8 x 1.6 x 0.45 mm, 26 faces (baked)
FEATURE [Part::Feature] Shape013  label="R14_R_0603_1608Metric_5FA65F77"
  Placement = pos=(126.111,-95.631,0) rot=(0,0,1;0rad)
  shape: bbox 1.6 x 0.8 x 0.45 mm, 26 faces (baked)
FEATURE [Part::Feature] Shape012  label="R15_R_0603_1608Metric_5FA65F88"
  Placement = pos=(126.365,-85.725,0) rot=(0,0,1;3.14159rad)
  shape: bbox 1.6 x 0.8 x 0.45 mm, 26 faces (baked)
FEATURE [Part::Feature] Shape  label="T1_Transformer_Hammond_229B34_5FA7BDFB[2]"
  Placement = pos=(38.2778,-66.0146,0) rot=(0,0,-1;1.5708rad)
  shape: bbox 51 x 64 x 30.5 mm, 1304 faces, 5 solids (baked)
FEATURE [Part::Feature] Shape049  label="D1_TO_252_2_5FA7B8E9"
  Placement = pos=(77.9534,-103.659,-1.6) rot=(0.707107,-0.707107,0;3.14159rad)
  shape: bbox 6.5 x 9.9 x 2.32 mm, 80 faces (baked)
FEATURE [Part::Feature] Shape035  label="J4_TerminalBlock_1x03_P2_54mm_Horizontal_5FA65D8D"
  Placement = pos=(113.284,-118.618,0) rot=(0,0,1;0rad)
  shape: bbox 7.62 x 6.5 x 12 mm, 465 faces, 7 solids (baked)
FEATURE [Part::Feature] Shape004  label="U3_TO_252_2_5FA7BD9A"
  Placement = pos=(56.388,-92.524,-1.6) rot=(0.707107,0.707107,0;3.14159rad)
  shape: bbox 6.5 x 9.9 x 2.32 mm, 80 faces (baked)
FEATURE [Part::Feature] Shape023  label="R4_R_0603_1608Metric_5FA8FFBA"
  Placement = pos=(120.142,-69.85,-1.6) rot=(0.707107,0.707107,0;3.14159rad)
  shape: bbox 0.8 x 1.6 x 0.45 mm, 26 faces (baked)
FEATURE [Part::Feature] Shape017  label="R10_R_0603_1608Metric_5FA65F33"
  Placement = pos=(113.538,-69.85,-1.6) rot=(0.707107,0.707107,0;3.14159rad)
  shape: bbox 0.8 x 1.6 x 0.45 mm, 26 faces (baked)
FEATURE [Part::Feature] Shape048  label="D2_TO_252_2_5FA7B952"
  Placement = pos=(77.9534,-92.483,-1.6) rot=(0.707107,0.707107,0;3.14159rad)
  shape: bbox 6.5 x 9.9 x 2.32 mm, 80 faces (baked)
FEATURE [Part::Feature] Shape067  label="C7_C_0603_1608Metric_5FA659CE"
  Placement = pos=(110.109,-82.55,-1.6) rot=(0.707107,-0.707107,0;3.14159rad)
  shape: bbox 0.8 x 1.6 x 0.8 mm, 28 faces (baked)
FEATURE [Part::Feature] Shape063  label="C11_C_0603_1608Metric_5FA7BA7A"
  Placement = pos=(58.674,-100.089,-1.6) rot=(0.707107,0.707107,0;3.14159rad)
  shape: bbox 0.8 x 1.6 x 0.8 mm, 28 faces (baked)
FEATURE [Part::Feature] Shape069  label="C5_C_0805_2012Metric_5FA8FE6E"
  Placement = pos=(118.364,-70.104,-1.6) rot=(0.707107,0.707107,0;3.14159rad)
  shape: bbox 1.25 x 2 x 1.25 mm, 28 faces (baked)
FEATURE [Part::Feature] Shape060  label="C14_C_0805_2012Metric_5FA7BADA"
  Placement = pos=(54.102,-100.264,-1.6) rot=(0.707107,-0.707107,0;3.14159rad)
  shape: bbox 1.25 x 2 x 1.25 mm, 28 faces (baked)
FEATURE [Part::Feature] Shape057  label="C17_C_0603_1608Metric_5FA7D2EE"
  Placement = pos=(63.754,-100.089,-1.6) rot=(0.707107,0.707107,0;3.14159rad)
  shape: bbox 0.8 x 1.6 x 0.8 mm, 28 faces (baked)
FEATURE [Part::Feature] Shape065  label="C9_CP_Elec_8x105_5FA7E577"
  Placement = pos=(119.38,-102.743,0) rot=(0,0,1;1.5708rad)
  shape: bbox 10.92 x 10.73 x 10.5 mm, 41 faces (baked)
FEATURE [Part::Feature] Shape051  label="C23_C_0603_1608Metric_5FA8C9CC"
  Placement = pos=(121.666,-69.85,-1.6) rot=(0.707107,0.707107,0;3.14159rad)
  shape: bbox 0.8 x 1.6 x 0.8 mm, 28 faces (baked)
FEATURE [Part::Feature] Shape047  label="D3_TO_252_2_5FA7BB7D"
  Placement = pos=(41.864,-92.483,-1.6) rot=(0.707107,0.707107,0;3.14159rad)
  shape: bbox 6.5 x 9.9 x 2.32 mm, 80 faces (baked)
FEATURE [Part::Feature] Shape024  label="R3_R_0603_1608Metric_5FA65EBC"
  Placement = pos=(102.362,-69.85,-1.6) rot=(0.707107,0.707107,0;3.14159rad)
  shape: bbox 0.8 x 1.6 x 0.45 mm, 26 faces (baked)
FEATURE [Part::Feature] Shape045  label="D5_TO_252_2_5FA7B9BB"
  Placement = pos=(70.858,-92.483,-1.6) rot=(0.707107,0.707107,0;3.14159rad)
  shape: bbox 6.5 x 9.9 x 2.32 mm, 80 faces (baked)
FEATURE [Part::Feature] Shape071  label="C2_C_0603_1608Metric_5FA6594B"
  Placement = pos=(103.886,-69.85,-1.6) rot=(0.707107,0.707107,0;3.14159rad)
  shape: bbox 0.8 x 1.6 x 0.8 mm, 28 faces (baked)
FEATURE [Part::Feature] Shape070  label="C4_CP_Elec_18x22_5FA6599B"
  Placement = pos=(95.404,-79.864,0) rot=(0,0,1;1.5708rad)
  shape: bbox 24.31 x 24.3 x 22 mm, 41 faces (baked)
FEATURE [Part::Feature] Shape022  label="R5_R_0603_1608Metric_5FA65EDE"
  Placement = pos=(105.41,-69.85,-1.6) rot=(0.707107,0.707107,0;3.14159rad)
  shape: bbox 0.8 x 1.6 x 0.45 mm, 26 faces (baked)
FEATURE [Part::Feature] Shape033  label="J6_TerminalBlock_1x02_P2_54mm_Horizontal_5FA65DCD[2]"
  Placement = pos=(105.156,-118.618,0) rot=(0,0,1;0rad)
  shape: bbox 5.08 x 6.5 x 12 mm, 313 faces, 5 solids (baked)
FEATURE [Part::Feature] Shape026  label="R1_R_0603_1608Metric_5FA8CE55"
  Placement = pos=(100.838,-69.85,-1.6) rot=(0.707107,0.707107,0;3.14159rad)
  shape: bbox 0.8 x 1.6 x 0.45 mm, 26 faces (baked)
FEATURE [Part::Feature] Shape050  label="C24_C_0603_1608Metric_5FA65B4B"
  Placement = pos=(114.681,-82.55,-1.6) rot=(0.707107,0.707107,0;3.14159rad)
  shape: bbox 0.8 x 1.6 x 0.8 mm, 28 faces (baked)
FEATURE [Part::Feature] Shape043  label="D7_TO_252_2_5FA7BA24"
  Placement = pos=(48.958,-92.483,-1.6) rot=(0.707107,0.707107,0;3.14159rad)
  shape: bbox 6.5 x 9.9 x 2.32 mm, 80 faces (baked)
FEATURE [App::Part] Bot_132a
  Group = -> [Shape001,Shape003,Shape004,Shape007,Shape008,Shape009,Shape014,Shape015,Shape017,Shape019,Shape020,Shape021,Shape022,Shape023,Shape024,Shape025,Shape026,Shape042,Shape043,Shape044,Shape045,Shape046,Shape047,Shape048,Shape049,Shape050,Shape051,Shape054,Shape055,Shape056,Shape057,Shape058,Shape059,Shape060,Shape062,Shape063,Shape064,Shape066,Shape067,Shape068,Shape069,Shape071,Shape072]
  Origin = -> Origin007
FEATURE [Part::Feature] Pcb_132a
  shape: bbox 109 x 64.52 x 1.6 mm, 54 faces (baked)
FEATURE [App::Part] Board_Geoms_132a
  Group = -> [Local_CS_132a,Pcb_132a,PCB_Sketch_132a]
  Origin = -> Origin004
FEATURE [Part::Feature] Shape029  label="J10_TerminalBlock_1x02_P2_54mm_Horizontal_5FA65E55[2]"
  Placement = pos=(129.794,-61.722,0) rot=(0,0,1;3.14159rad)
  shape: bbox 5.08 x 6.5 x 12 mm, 313 faces, 5 solids (baked)
FEATURE [Part::Feature] Shape030  label="J9_TerminalBlock_1x02_P2_54mm_Horizontal_5FA65E35[2]"
  Placement = pos=(115.062,-61.722,0) rot=(0,0,1;3.14159rad)
  shape: bbox 5.08 x 6.5 x 12 mm, 313 faces, 5 solids (baked)
FEATURE [Part::Feature] Shape028  label="Q1_TO-126-3_Vertical_5FA65E6F"
  Placement = pos=(129.413,-94.869,0) rot=(0,0,-1;1.5708rad)
  shape: bbox 3.25 x 8 x 23.75 mm, 66 faces (baked)
FEATURE [App::Part] Top_132a
  Group = -> [Shape,Shape002,Shape005,Shape006,Shape010,Shape011,Shape012,Shape013,Shape016,Shape018,Shape027,Shape028,Shape029,Shape030,Shape031,Shape032,Shape033,Shape034,Shape035,Shape036,Shape037,Shape038,Shape039,Shape040,Shape041,Shape052,Shape053,Shape061,Shape065,Shape070]
  Origin = -> Origin006
FEATURE [App::Part] Step_Models_132a
  Group = -> [Top_132a,Bot_132a]
  Origin = -> Origin003
FEATURE [App::Part] Board_132a  label="op-amp_reverb_driver"
  Group = -> [Board_Geoms_132a,Step_Models_132a]
  Origin = -> Origin005
  Placement = pos=(187.38,-66.5,-9) rot=(0,0,1;3.14159rad)
